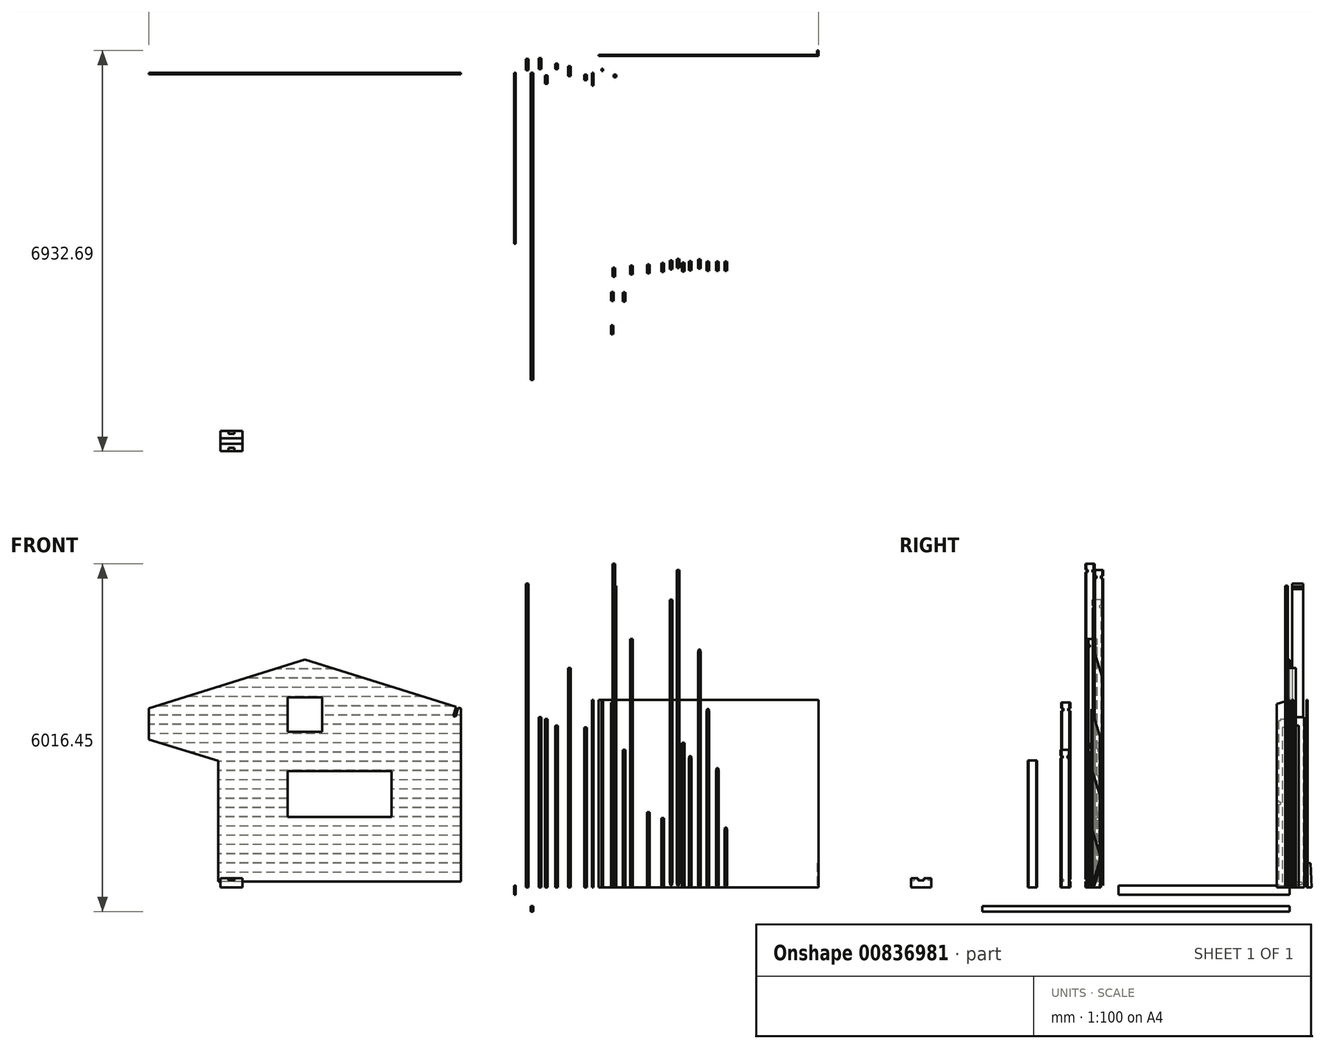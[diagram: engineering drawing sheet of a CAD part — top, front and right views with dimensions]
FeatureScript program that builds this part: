
annotation { "Feature Type Name" : "Feature", "Feature Type Description" : "" }
export const myFeature = defineFeature(function(context is Context, id is Id, definition is map)
    precondition{}
    {
        {
            var Q0;
            Q0=qCreatedBy(makeId("Top.planeOp"),FACE);
            var sketch = newSketch(context, id + "F0", { "sketchPlane" : qUnion([Q0])});
            skLineSegment(sketch, "E0.bottom", {"start": v(-174.56, 238.66) * mm, "end": v(-129.56, 238.66) * mm});
            skLineSegment(sketch, "E0.top", {"start": v(-174.56, 43.66) * mm, "end": v(-129.56, 43.66) * mm});
            skLineSegment(sketch, "E0.left", {"start": v(-174.56, 238.66) * mm, "end": v(-174.56, 43.66) * mm});
            skLineSegment(sketch, "E0.right", {"start": v(-129.56, 238.66) * mm, "end": v(-129.56, 43.66) * mm});
            skSolve(sketch);
        }
        {
            var Q0;
            Q0=makeQuery(id+"F0.imprint","IMPRINT",FACE,{"disambiguationData":[TD([[makeQuery(id+"F0.imprint","IMPRINT",EDGE,{"derivedFrom":sQuery(id+"F0.wireOp",EDGE,"E0.bottom")}),-1.0]])]});
            extrude(context, id + "F1", {"entities" : qUnion([Q0]), "depth" : 5255 * mm, "offsetDistance" : 25 * mm});
        }
        {
            var Q0;
            Q0=qCreatedBy(makeId("Top.planeOp"),FACE);
            var sketch = newSketch(context, id + "F2", { "sketchPlane" : qUnion([Q0])});
            skLineSegment(sketch, "E1.bottom", {"start": v(49.35, 255.3) * mm, "end": v(94.35, 255.3) * mm});
            skLineSegment(sketch, "E1.top", {"start": v(49.35, 60.3) * mm, "end": v(94.35, 60.3) * mm});
            skLineSegment(sketch, "E1.left", {"start": v(49.35, 255.3) * mm, "end": v(49.35, 60.3) * mm});
            skLineSegment(sketch, "E1.right", {"start": v(94.35, 255.3) * mm, "end": v(94.35, 60.3) * mm});
            skSolve(sketch);
        }
        {
            var Q0;
            Q0=makeQuery(id+"F2.imprint","IMPRINT",FACE,{"disambiguationData":[TD([[makeQuery(id+"F2.imprint","IMPRINT",EDGE,{"derivedFrom":sQuery(id+"F2.wireOp",EDGE,"E1.bottom")}),-1.0]])]});
            extrude(context, id + "F3", {"entities" : qUnion([Q0]), "depth" : 2945 * mm, "offsetDistance" : 25 * mm});
        }
        {
            var Q0;
            Q0=qCreatedBy(makeId("Top.planeOp"),FACE);
            var sketch = newSketch(context, id + "F4", { "sketchPlane" : qUnion([Q0])});
            skLineSegment(sketch, "E2.bottom", {"start": v(202.86, -191.83) * mm, "end": v(157.86, -191.83) * mm});
            skLineSegment(sketch, "E2.top", {"start": v(202.86, -46.83) * mm, "end": v(157.86, -46.83) * mm});
            skLineSegment(sketch, "E2.left", {"start": v(202.86, -191.83) * mm, "end": v(202.86, -46.83) * mm});
            skLineSegment(sketch, "E2.right", {"start": v(157.86, -191.83) * mm, "end": v(157.86, -46.83) * mm});
            skSolve(sketch);
        }
        {
            var Q0;
            Q0=makeQuery(id+"F4.imprint","IMPRINT",FACE,{"disambiguationData":[TD([[makeQuery(id+"F4.imprint","IMPRINT",EDGE,{"derivedFrom":sQuery(id+"F4.wireOp",EDGE,"E2.bottom")}),-1.0]])]});
            extrude(context, id + "F5", {"entities" : qUnion([Q0]), "depth" : 2914 * mm, "offsetDistance" : 25 * mm});
        }
        {
            var Q0;
            Q0=qCreatedBy(makeId("Front.planeOp"),FACE);
            var sketch = newSketch(context, id + "F6", { "sketchPlane" : qUnion([Q0])});
            skLineSegment(sketch, "E3", {"start": v(-1295, 99.93) * mm, "end": v(-6695, 99.93) * mm});
            skLineSegment(sketch, "E4", {"start": v(-6695, 99.93) * mm, "end": v(-6695, 3099.93) * mm});
            skLineSegment(sketch, "E5", {"start": v(-6695, 3099.93) * mm, "end": v(-3995, 3940.89) * mm});
            skLineSegment(sketch, "E6", {"start": v(-1295, 99.93) * mm, "end": v(-1295, 3099.93) * mm});
            skLineSegment(sketch, "E7", {"start": v(-1295, 3099.93) * mm, "end": v(-3995, 3940.89) * mm});
            skLineSegment(sketch, "E8.bottom", {"start": v(-1381.97, 3127.02) * mm, "end": v(-1339, 3113.63) * mm});
            skLineSegment(sketch, "E8.top", {"start": v(-1432.53, 2964.7) * mm, "end": v(-1389.56, 2951.33) * mm});
            skLineSegment(sketch, "E8.left", {"start": v(-1381.97, 3127.02) * mm, "end": v(-1432.53, 2964.7) * mm});
            skLineSegment(sketch, "E8.right", {"start": v(-1339, 3113.63) * mm, "end": v(-1389.56, 2951.33) * mm});
            skSolve(sketch);
        }
        {
            var Q0;
            Q0=makeQuery(id+"F6.imprint","IMPRINT",FACE,{"disambiguationData":[TD([[makeQuery(id+"F6.imprint","IMPRINT",EDGE,{"derivedFrom":sQuery(id+"F6.wireOp",EDGE,"E3")}),-1.0]])]});
            extrude(context, id + "F7", {"entities" : qUnion([Q0]), "depth" : 25 * mm, "offsetDistance" : 25 * mm});
        }
        {
            var Q0;
            Q0=makeQuery(id+"F7.opExtrude","SWEPT_FACE",FACE,{"disambiguationData":[OSD([sQuery(id+"F6.wireOp",EDGE,"E4")])]});
            var sketch = newSketch(context, id + "F8", { "sketchPlane" : qUnion([Q0])});
            skLineSegment(sketch, "E9.bottom", {"start": v(0, 262.93) * mm, "end": v(3, 262.93) * mm});
            skLineSegment(sketch, "E9.top", {"start": v(0, 259.93) * mm, "end": v(3, 259.93) * mm});
            skLineSegment(sketch, "E9.left", {"start": v(0, 262.93) * mm, "end": v(0, 259.93) * mm});
            skLineSegment(sketch, "E9.right", {"start": v(3, 262.93) * mm, "end": v(3, 259.93) * mm});
            skLineSegment(sketch, "E10.0.1.0", {"start": v(0, 419.93) * mm, "end": v(3, 419.93) * mm});
            skLineSegment(sketch, "E10.0.1.1", {"start": v(3, 422.93) * mm, "end": v(3, 419.93) * mm});
            skLineSegment(sketch, "E10.0.1.2", {"start": v(0, 422.93) * mm, "end": v(0, 419.93) * mm});
            skLineSegment(sketch, "E10.0.1.3", {"start": v(0, 422.93) * mm, "end": v(3, 422.93) * mm});
            skLineSegment(sketch, "E10.0.2.0", {"start": v(0, 579.93) * mm, "end": v(3, 579.93) * mm});
            skLineSegment(sketch, "E10.0.2.1", {"start": v(3, 582.93) * mm, "end": v(3, 579.93) * mm});
            skLineSegment(sketch, "E10.0.2.2", {"start": v(0, 582.93) * mm, "end": v(0, 579.93) * mm});
            skLineSegment(sketch, "E10.0.2.3", {"start": v(0, 582.93) * mm, "end": v(3, 582.93) * mm});
            skLineSegment(sketch, "E10.0.3.0", {"start": v(0, 739.93) * mm, "end": v(3, 739.93) * mm});
            skLineSegment(sketch, "E10.0.3.1", {"start": v(3, 742.93) * mm, "end": v(3, 739.93) * mm});
            skLineSegment(sketch, "E10.0.3.2", {"start": v(0, 742.93) * mm, "end": v(0, 739.93) * mm});
            skLineSegment(sketch, "E10.0.3.3", {"start": v(0, 742.93) * mm, "end": v(3, 742.93) * mm});
            skLineSegment(sketch, "E10.0.4.0", {"start": v(0, 899.93) * mm, "end": v(3, 899.93) * mm});
            skLineSegment(sketch, "E10.0.4.1", {"start": v(3, 902.93) * mm, "end": v(3, 899.93) * mm});
            skLineSegment(sketch, "E10.0.4.2", {"start": v(0, 902.93) * mm, "end": v(0, 899.93) * mm});
            skLineSegment(sketch, "E10.0.4.3", {"start": v(0, 902.93) * mm, "end": v(3, 902.93) * mm});
            skLineSegment(sketch, "E10.0.5.0", {"start": v(0, 1059.93) * mm, "end": v(3, 1059.93) * mm});
            skLineSegment(sketch, "E10.0.5.1", {"start": v(3, 1062.93) * mm, "end": v(3, 1059.93) * mm});
            skLineSegment(sketch, "E10.0.5.2", {"start": v(0, 1062.93) * mm, "end": v(0, 1059.93) * mm});
            skLineSegment(sketch, "E10.0.5.3", {"start": v(0, 1062.93) * mm, "end": v(3, 1062.93) * mm});
            skLineSegment(sketch, "E10.0.6.0", {"start": v(0, 1219.93) * mm, "end": v(3, 1219.93) * mm});
            skLineSegment(sketch, "E10.0.6.1", {"start": v(3, 1222.93) * mm, "end": v(3, 1219.93) * mm});
            skLineSegment(sketch, "E10.0.6.2", {"start": v(0, 1222.93) * mm, "end": v(0, 1219.93) * mm});
            skLineSegment(sketch, "E10.0.6.3", {"start": v(0, 1222.93) * mm, "end": v(3, 1222.93) * mm});
            skLineSegment(sketch, "E10.0.7.0", {"start": v(0, 1379.93) * mm, "end": v(3, 1379.93) * mm});
            skLineSegment(sketch, "E10.0.7.1", {"start": v(3, 1382.93) * mm, "end": v(3, 1379.93) * mm});
            skLineSegment(sketch, "E10.0.7.2", {"start": v(0, 1382.93) * mm, "end": v(0, 1379.93) * mm});
            skLineSegment(sketch, "E10.0.7.3", {"start": v(0, 1382.93) * mm, "end": v(3, 1382.93) * mm});
            skLineSegment(sketch, "E10.0.8.0", {"start": v(0, 1539.93) * mm, "end": v(3, 1539.93) * mm});
            skLineSegment(sketch, "E10.0.8.1", {"start": v(3, 1542.93) * mm, "end": v(3, 1539.93) * mm});
            skLineSegment(sketch, "E10.0.8.2", {"start": v(0, 1542.93) * mm, "end": v(0, 1539.93) * mm});
            skLineSegment(sketch, "E10.0.8.3", {"start": v(0, 1542.93) * mm, "end": v(3, 1542.93) * mm});
            skLineSegment(sketch, "E10.0.9.0", {"start": v(0, 1699.93) * mm, "end": v(3, 1699.93) * mm});
            skLineSegment(sketch, "E10.0.9.1", {"start": v(3, 1702.93) * mm, "end": v(3, 1699.93) * mm});
            skLineSegment(sketch, "E10.0.9.2", {"start": v(0, 1702.93) * mm, "end": v(0, 1699.93) * mm});
            skLineSegment(sketch, "E10.0.9.3", {"start": v(0, 1702.93) * mm, "end": v(3, 1702.93) * mm});
            skLineSegment(sketch, "E10.0.10.0", {"start": v(0, 1859.93) * mm, "end": v(3, 1859.93) * mm});
            skLineSegment(sketch, "E10.0.10.1", {"start": v(3, 1862.93) * mm, "end": v(3, 1859.93) * mm});
            skLineSegment(sketch, "E10.0.10.2", {"start": v(0, 1862.93) * mm, "end": v(0, 1859.93) * mm});
            skLineSegment(sketch, "E10.0.10.3", {"start": v(0, 1862.93) * mm, "end": v(3, 1862.93) * mm});
            skLineSegment(sketch, "E10.0.11.0", {"start": v(0, 2019.93) * mm, "end": v(3, 2019.93) * mm});
            skLineSegment(sketch, "E10.0.11.1", {"start": v(3, 2022.93) * mm, "end": v(3, 2019.93) * mm});
            skLineSegment(sketch, "E10.0.11.2", {"start": v(0, 2022.93) * mm, "end": v(0, 2019.93) * mm});
            skLineSegment(sketch, "E10.0.11.3", {"start": v(0, 2022.93) * mm, "end": v(3, 2022.93) * mm});
            skLineSegment(sketch, "E10.direction1", {"start": v(0, 259.93) * mm, "end": v(25, 259.93) * mm, "construction": true});
            skLineSegment(sketch, "E10.direction2", {"start": v(0, 259.93) * mm, "end": v(0, 419.93) * mm, "construction": true});
            skLineSegment(sketch, "E11.0.0.12", {"start": v(0, 2179.93) * mm, "end": v(3, 2179.93) * mm});
            skLineSegment(sketch, "E11.3.0.12", {"start": v(3, 2182.93) * mm, "end": v(3, 2179.93) * mm});
            skLineSegment(sketch, "E11.6.0.12", {"start": v(0, 2182.93) * mm, "end": v(0, 2179.93) * mm});
            skLineSegment(sketch, "E11.9.0.12", {"start": v(0, 2182.93) * mm, "end": v(3, 2182.93) * mm});
            skLineSegment(sketch, "E11.0.0.13", {"start": v(0, 2339.93) * mm, "end": v(3, 2339.93) * mm});
            skLineSegment(sketch, "E11.3.0.13", {"start": v(3, 2342.93) * mm, "end": v(3, 2339.93) * mm});
            skLineSegment(sketch, "E11.6.0.13", {"start": v(0, 2342.93) * mm, "end": v(0, 2339.93) * mm});
            skLineSegment(sketch, "E11.9.0.13", {"start": v(0, 2342.93) * mm, "end": v(3, 2342.93) * mm});
            skLineSegment(sketch, "E11.0.0.14", {"start": v(0, 2499.93) * mm, "end": v(3, 2499.93) * mm});
            skLineSegment(sketch, "E11.3.0.14", {"start": v(3, 2502.93) * mm, "end": v(3, 2499.93) * mm});
            skLineSegment(sketch, "E11.6.0.14", {"start": v(0, 2502.93) * mm, "end": v(0, 2499.93) * mm});
            skLineSegment(sketch, "E11.9.0.14", {"start": v(0, 2502.93) * mm, "end": v(3, 2502.93) * mm});
            skLineSegment(sketch, "E11.0.0.15", {"start": v(0, 2659.93) * mm, "end": v(3, 2659.93) * mm});
            skLineSegment(sketch, "E11.3.0.15", {"start": v(3, 2662.93) * mm, "end": v(3, 2659.93) * mm});
            skLineSegment(sketch, "E11.6.0.15", {"start": v(0, 2662.93) * mm, "end": v(0, 2659.93) * mm});
            skLineSegment(sketch, "E11.9.0.15", {"start": v(0, 2662.93) * mm, "end": v(3, 2662.93) * mm});
            skLineSegment(sketch, "E11.0.0.16", {"start": v(0, 2819.93) * mm, "end": v(3, 2819.93) * mm});
            skLineSegment(sketch, "E11.3.0.16", {"start": v(3, 2822.93) * mm, "end": v(3, 2819.93) * mm});
            skLineSegment(sketch, "E11.6.0.16", {"start": v(0, 2822.93) * mm, "end": v(0, 2819.93) * mm});
            skLineSegment(sketch, "E11.9.0.16", {"start": v(0, 2822.93) * mm, "end": v(3, 2822.93) * mm});
            skLineSegment(sketch, "E11.0.0.17", {"start": v(0, 2979.93) * mm, "end": v(3, 2979.93) * mm});
            skLineSegment(sketch, "E11.3.0.17", {"start": v(3, 2982.93) * mm, "end": v(3, 2979.93) * mm});
            skLineSegment(sketch, "E11.6.0.17", {"start": v(0, 2982.93) * mm, "end": v(0, 2979.93) * mm});
            skLineSegment(sketch, "E11.9.0.17", {"start": v(0, 2982.93) * mm, "end": v(3, 2982.93) * mm});
            skLineSegment(sketch, "E11.0.0.18", {"start": v(0, 3139.93) * mm, "end": v(3, 3139.93) * mm});
            skLineSegment(sketch, "E11.3.0.18", {"start": v(3, 3142.93) * mm, "end": v(3, 3139.93) * mm});
            skLineSegment(sketch, "E11.6.0.18", {"start": v(0, 3142.93) * mm, "end": v(0, 3139.93) * mm});
            skLineSegment(sketch, "E11.9.0.18", {"start": v(0, 3142.93) * mm, "end": v(3, 3142.93) * mm});
            skLineSegment(sketch, "E11.0.0.19", {"start": v(0, 3299.93) * mm, "end": v(3, 3299.93) * mm});
            skLineSegment(sketch, "E11.3.0.19", {"start": v(3, 3302.93) * mm, "end": v(3, 3299.93) * mm});
            skLineSegment(sketch, "E11.6.0.19", {"start": v(0, 3302.93) * mm, "end": v(0, 3299.93) * mm});
            skLineSegment(sketch, "E11.9.0.19", {"start": v(0, 3302.93) * mm, "end": v(3, 3302.93) * mm});
            skLineSegment(sketch, "E12.0.0.20", {"start": v(0, 3459.93) * mm, "end": v(3, 3459.93) * mm});
            skLineSegment(sketch, "E12.3.0.20", {"start": v(3, 3462.93) * mm, "end": v(3, 3459.93) * mm});
            skLineSegment(sketch, "E12.6.0.20", {"start": v(0, 3462.93) * mm, "end": v(0, 3459.93) * mm});
            skLineSegment(sketch, "E12.9.0.20", {"start": v(0, 3462.93) * mm, "end": v(3, 3462.93) * mm});
            skLineSegment(sketch, "E12.0.0.21", {"start": v(0, 3619.93) * mm, "end": v(3, 3619.93) * mm});
            skLineSegment(sketch, "E12.3.0.21", {"start": v(3, 3622.93) * mm, "end": v(3, 3619.93) * mm});
            skLineSegment(sketch, "E12.6.0.21", {"start": v(0, 3622.93) * mm, "end": v(0, 3619.93) * mm});
            skLineSegment(sketch, "E12.9.0.21", {"start": v(0, 3622.93) * mm, "end": v(3, 3622.93) * mm});
            skLineSegment(sketch, "E12.0.0.22", {"start": v(0, 3779.93) * mm, "end": v(3, 3779.93) * mm});
            skLineSegment(sketch, "E12.3.0.22", {"start": v(3, 3782.93) * mm, "end": v(3, 3779.93) * mm});
            skLineSegment(sketch, "E12.6.0.22", {"start": v(0, 3782.93) * mm, "end": v(0, 3779.93) * mm});
            skLineSegment(sketch, "E12.9.0.22", {"start": v(0, 3782.93) * mm, "end": v(3, 3782.93) * mm});
            skLineSegment(sketch, "E12.0.0.23", {"start": v(0, 3939.93) * mm, "end": v(3, 3939.93) * mm});
            skLineSegment(sketch, "E12.3.0.23", {"start": v(3, 3942.93) * mm, "end": v(3, 3939.93) * mm});
            skLineSegment(sketch, "E12.6.0.23", {"start": v(0, 3942.93) * mm, "end": v(0, 3939.93) * mm});
            skLineSegment(sketch, "E12.9.0.23", {"start": v(0, 3942.93) * mm, "end": v(3, 3942.93) * mm});
            skLineSegment(sketch, "E12.0.0.24", {"start": v(0, 4099.93) * mm, "end": v(3, 4099.93) * mm});
            skLineSegment(sketch, "E12.3.0.24", {"start": v(3, 4102.93) * mm, "end": v(3, 4099.93) * mm});
            skLineSegment(sketch, "E12.6.0.24", {"start": v(0, 4102.93) * mm, "end": v(0, 4099.93) * mm});
            skLineSegment(sketch, "E12.9.0.24", {"start": v(0, 4102.93) * mm, "end": v(3, 4102.93) * mm});
            skSolve(sketch);
        }
        {
            var Q0;
            Q0=makeQuery(id+"F8.imprint","IMPRINT",FACE,{"disambiguationData":[TD([[makeQuery(id+"F8.imprint","IMPRINT",EDGE,{"derivedFrom":sQuery(id+"F8.wireOp",EDGE,"E9.bottom")}),-1.0]])]});
            var Q1;
            Q1=makeQuery(id+"F8.imprint","IMPRINT",FACE,{"disambiguationData":[TD([[makeQuery(id+"F8.imprint","IMPRINT",EDGE,{"derivedFrom":sQuery(id+"F8.wireOp",EDGE,"E10.0.1.0")}),1.0]])]});
            var Q2;
            Q2=makeQuery(id+"F8.imprint","IMPRINT",FACE,{"disambiguationData":[TD([[makeQuery(id+"F8.imprint","IMPRINT",EDGE,{"derivedFrom":sQuery(id+"F8.wireOp",EDGE,"E10.0.3.0")}),1.0]])]});
            var Q3;
            Q3=makeQuery(id+"F8.imprint","IMPRINT",FACE,{"disambiguationData":[TD([[makeQuery(id+"F8.imprint","IMPRINT",EDGE,{"derivedFrom":sQuery(id+"F8.wireOp",EDGE,"E10.0.4.0")}),1.0]])]});
            var Q4;
            Q4=makeQuery(id+"F8.imprint","IMPRINT",FACE,{"disambiguationData":[TD([[makeQuery(id+"F8.imprint","IMPRINT",EDGE,{"derivedFrom":sQuery(id+"F8.wireOp",EDGE,"E10.0.5.0")}),1.0]])]});
            var Q5;
            Q5=makeQuery(id+"F8.imprint","IMPRINT",FACE,{"disambiguationData":[TD([[makeQuery(id+"F8.imprint","IMPRINT",EDGE,{"derivedFrom":sQuery(id+"F8.wireOp",EDGE,"E10.0.6.0")}),1.0]])]});
            var Q6;
            Q6=makeQuery(id+"F8.imprint","IMPRINT",FACE,{"disambiguationData":[TD([[makeQuery(id+"F8.imprint","IMPRINT",EDGE,{"derivedFrom":sQuery(id+"F8.wireOp",EDGE,"E10.0.7.0")}),1.0]])]});
            var Q7;
            Q7=makeQuery(id+"F8.imprint","IMPRINT",FACE,{"disambiguationData":[TD([[makeQuery(id+"F8.imprint","IMPRINT",EDGE,{"derivedFrom":sQuery(id+"F8.wireOp",EDGE,"E10.0.8.0")}),1.0]])]});
            var Q8;
            Q8=makeQuery(id+"F8.imprint","IMPRINT",FACE,{"disambiguationData":[TD([[makeQuery(id+"F8.imprint","IMPRINT",EDGE,{"derivedFrom":sQuery(id+"F8.wireOp",EDGE,"E10.0.9.0")}),1.0]])]});
            var Q9;
            Q9=makeQuery(id+"F8.imprint","IMPRINT",FACE,{"disambiguationData":[TD([[makeQuery(id+"F8.imprint","IMPRINT",EDGE,{"derivedFrom":sQuery(id+"F8.wireOp",EDGE,"E10.0.10.0")}),1.0]])]});
            var Q10;
            Q10=makeQuery(id+"F8.imprint","IMPRINT",FACE,{"disambiguationData":[TD([[makeQuery(id+"F8.imprint","IMPRINT",EDGE,{"derivedFrom":sQuery(id+"F8.wireOp",EDGE,"E10.0.11.0")}),1.0]])]});
            var Q11;
            Q11=makeQuery(id+"F8.imprint","IMPRINT",FACE,{"disambiguationData":[TD([[makeQuery(id+"F8.imprint","IMPRINT",EDGE,{"derivedFrom":sQuery(id+"F8.wireOp",EDGE,"E10.0.2.0")}),1.0]])]});
            var Q12;
            Q12=makeQuery(id+"F8.imprint","IMPRINT",FACE,{"disambiguationData":[TD([[makeQuery(id+"F8.imprint","IMPRINT",EDGE,{"derivedFrom":sQuery(id+"F8.wireOp",EDGE,"E11.0.0.12")}),1.0]])]});
            var Q13;
            Q13=makeQuery(id+"F8.imprint","IMPRINT",FACE,{"disambiguationData":[TD([[makeQuery(id+"F8.imprint","IMPRINT",EDGE,{"derivedFrom":sQuery(id+"F8.wireOp",EDGE,"E11.0.0.13")}),1.0]])]});
            var Q14;
            Q14=makeQuery(id+"F8.imprint","IMPRINT",FACE,{"disambiguationData":[TD([[makeQuery(id+"F8.imprint","IMPRINT",EDGE,{"derivedFrom":sQuery(id+"F8.wireOp",EDGE,"E11.0.0.14")}),1.0]])]});
            var Q15;
            Q15=makeQuery(id+"F8.imprint","IMPRINT",FACE,{"disambiguationData":[TD([[makeQuery(id+"F8.imprint","IMPRINT",EDGE,{"derivedFrom":sQuery(id+"F8.wireOp",EDGE,"E11.0.0.15")}),1.0]])]});
            var Q16;
            Q16=makeQuery(id+"F8.imprint","IMPRINT",FACE,{"disambiguationData":[TD([[makeQuery(id+"F8.imprint","IMPRINT",EDGE,{"derivedFrom":sQuery(id+"F8.wireOp",EDGE,"E11.0.0.16")}),1.0]])]});
            var Q17;
            Q17=makeQuery(id+"F8.imprint","IMPRINT",FACE,{"disambiguationData":[TD([[makeQuery(id+"F8.imprint","IMPRINT",EDGE,{"derivedFrom":sQuery(id+"F8.wireOp",EDGE,"E11.0.0.17")}),1.0]])]});
            var Q18;
            Q18=makeQuery(id+"F8.imprint","IMPRINT",FACE,{"disambiguationData":[TD([[makeQuery(id+"F8.imprint","IMPRINT",EDGE,{"derivedFrom":sQuery(id+"F8.wireOp",EDGE,"E11.0.0.18")}),1.0]])]});
            var Q19;
            Q19=makeQuery(id+"F8.imprint","IMPRINT",FACE,{"disambiguationData":[TD([[makeQuery(id+"F8.imprint","IMPRINT",EDGE,{"derivedFrom":sQuery(id+"F8.wireOp",EDGE,"E11.0.0.19")}),1.0]])]});
            var Q20;
            Q20=makeQuery(id+"F8.imprint","IMPRINT",FACE,{"disambiguationData":[TD([[makeQuery(id+"F8.imprint","IMPRINT",EDGE,{"derivedFrom":sQuery(id+"F8.wireOp",EDGE,"E12.0.0.20")}),1.0]])]});
            var Q21;
            Q21=makeQuery(id+"F8.imprint","IMPRINT",FACE,{"disambiguationData":[TD([[makeQuery(id+"F8.imprint","IMPRINT",EDGE,{"derivedFrom":sQuery(id+"F8.wireOp",EDGE,"E12.0.0.21")}),1.0]])]});
            var Q22;
            Q22=makeQuery(id+"F8.imprint","IMPRINT",FACE,{"disambiguationData":[TD([[makeQuery(id+"F8.imprint","IMPRINT",EDGE,{"derivedFrom":sQuery(id+"F8.wireOp",EDGE,"E12.0.0.22")}),1.0]])]});
            var Q23;
            Q23=makeQuery(id+"F8.imprint","IMPRINT",FACE,{"disambiguationData":[TD([[makeQuery(id+"F8.imprint","IMPRINT",EDGE,{"derivedFrom":sQuery(id+"F8.wireOp",EDGE,"E12.0.0.23")}),1.0]])]});
            var Q24;
            Q24=makeQuery(id+"F8.imprint","IMPRINT",FACE,{"disambiguationData":[TD([[makeQuery(id+"F8.imprint","IMPRINT",EDGE,{"derivedFrom":sQuery(id+"F8.wireOp",EDGE,"E12.0.0.24")}),1.0]])]});
            extrude(context, id + "F9", {"entities" : qUnion([Q0, Q1, Q2, Q3, Q4, Q5, Q6, Q7, Q8, Q9, Q10, Q11, Q12, Q13, Q14, Q15, Q16, Q17, Q18, Q19, Q20, Q21, Q22, Q23, Q24]), "operationType" : NewBodyOperationType.REMOVE, "oppositeDirection" : true, "depth" : 5555 * mm, "offsetDistance" : 25 * mm});
        }
        {
            var Q0;
            Q0=qCreatedBy(makeId("Top.planeOp"),FACE);
            var sketch = newSketch(context, id + "F10", { "sketchPlane" : qUnion([Q0])});
            skLineSegment(sketch, "E13.bottom", {"start": v(336.12, 157.04) * mm, "end": v(381.12, 157.04) * mm});
            skLineSegment(sketch, "E13.top", {"start": v(336.12, 62.04) * mm, "end": v(381.12, 62.04) * mm});
            skLineSegment(sketch, "E13.left", {"start": v(336.12, 157.04) * mm, "end": v(336.12, 62.04) * mm});
            skLineSegment(sketch, "E13.right", {"start": v(381.12, 157.04) * mm, "end": v(381.12, 62.04) * mm});
            skSolve(sketch);
        }
        {
            var Q0;
            Q0=makeQuery(id+"F10.imprint","IMPRINT",FACE,{"disambiguationData":[TD([[makeQuery(id+"F10.imprint","IMPRINT",EDGE,{"derivedFrom":sQuery(id+"F10.wireOp",EDGE,"E13.bottom")}),-1.0]])]});
            extrude(context, id + "F11", {"entities" : qUnion([Q0]), "depth" : 2800 * mm, "offsetDistance" : 25 * mm});
        }
        {
            var Q0;
            Q0=qCreatedBy(makeId("Top.planeOp"),FACE);
            var sketch = newSketch(context, id + "F12", { "sketchPlane" : qUnion([Q0])});
            skLineSegment(sketch, "E14.bottom", {"start": v(558.27, 111.52) * mm, "end": v(603.27, 111.52) * mm});
            skLineSegment(sketch, "E14.top", {"start": v(558.27, -58.48) * mm, "end": v(603.27, -58.48) * mm});
            skLineSegment(sketch, "E14.left", {"start": v(558.27, 111.52) * mm, "end": v(558.27, -58.48) * mm});
            skLineSegment(sketch, "E14.right", {"start": v(603.27, 111.52) * mm, "end": v(603.27, -58.48) * mm});
            skSolve(sketch);
        }
        {
            var Q0;
            Q0=makeQuery(id+"F12.imprint","IMPRINT",FACE,{"disambiguationData":[TD([[makeQuery(id+"F12.imprint","IMPRINT",EDGE,{"derivedFrom":sQuery(id+"F12.wireOp",EDGE,"E14.bottom")}),-1.0]])]});
            extrude(context, id + "F13", {"entities" : qUnion([Q0]), "depth" : 3800 * mm, "offsetDistance" : 25 * mm});
        }
        {
            var Q0;
            Q0=qCreatedBy(makeId("Top.planeOp"),FACE);
            var sketch = newSketch(context, id + "F14", { "sketchPlane" : qUnion([Q0])});
            skLineSegment(sketch, "E15.bottom", {"start": v(838.72, -32.1) * mm, "end": v(883.72, -32.1) * mm});
            skLineSegment(sketch, "E15.top", {"start": v(838.72, -127.1) * mm, "end": v(883.72, -127.1) * mm});
            skLineSegment(sketch, "E15.left", {"start": v(838.72, -32.1) * mm, "end": v(838.72, -127.1) * mm});
            skLineSegment(sketch, "E15.right", {"start": v(883.72, -32.1) * mm, "end": v(883.72, -127.1) * mm});
            skSolve(sketch);
        }
        {
            var Q0;
            Q0=makeQuery(id+"F14.imprint","IMPRINT",FACE,{"disambiguationData":[TD([[makeQuery(id+"F14.imprint","IMPRINT",EDGE,{"derivedFrom":sQuery(id+"F14.wireOp",EDGE,"E15.bottom")}),-1.0]])]});
            extrude(context, id + "F15", {"entities" : qUnion([Q0]), "depth" : 2768 * mm, "offsetDistance" : 25 * mm});
        }
        {
            var Q0;
            Q0=qCreatedBy(makeId("Top.planeOp"),FACE);
            var sketch = newSketch(context, id + "F16", { "sketchPlane" : qUnion([Q0])});
            skLineSegment(sketch, "E16.bottom", {"start": v(971.19, 0) * mm, "end": v(993.19, 0) * mm});
            skLineSegment(sketch, "E16.top", {"start": v(971.19, -220) * mm, "end": v(993.19, -220) * mm});
            skLineSegment(sketch, "E16.left", {"start": v(971.19, 0) * mm, "end": v(971.19, -220) * mm});
            skLineSegment(sketch, "E16.right", {"start": v(993.19, 0) * mm, "end": v(993.19, -220) * mm});
            skSolve(sketch);
        }
        {
            var Q0;
            Q0=makeQuery(id+"F16.imprint","IMPRINT",FACE,{"disambiguationData":[TD([[makeQuery(id+"F16.imprint","IMPRINT",EDGE,{"derivedFrom":sQuery(id+"F16.wireOp",EDGE,"E16.bottom")}),-1.0]])]});
            extrude(context, id + "F17", {"entities" : qUnion([Q0]), "depth" : 3333 * mm, "offsetDistance" : 25 * mm});
        }
        {
            var Q0;
            Q0=makeQuery(id+"F17.opExtrude","SWEPT_FACE",FACE,{"disambiguationData":[OSD([sQuery(id+"F16.wireOp",EDGE,"E16.right")])]});
            var sketch = newSketch(context, id + "F18", { "sketchPlane" : qUnion([Q0])});
            skLineSegment(sketch, "E17", {"start": v(0, 3333) * mm, "end": v(-220, 3333) * mm});
            skLineSegment(sketch, "E18", {"start": v(-220, 3333) * mm, "end": v(-220, 3264.48) * mm});
            skLineSegment(sketch, "E19", {"start": v(-220, 3264.48) * mm, "end": v(0, 3333) * mm});
            skLineSegment(sketch, "E20", {"start": v(0, 3333) * mm, "end": v(0, 3245.66) * mm});
            skLineSegment(sketch, "E21", {"start": v(0, 3245.66) * mm, "end": v(-220, 3177.14) * mm});
            skLineSegment(sketch, "E22", {"start": v(-220, 3177.14) * mm, "end": v(-220, 3264.48) * mm});
            skSolve(sketch);
        }
        {
            var Q0;
            Q0=makeQuery(id+"F18.imprint","IMPRINT",FACE,{"disambiguationData":[TD([[makeQuery(id+"F18.imprint","IMPRINT",EDGE,{"derivedFrom":sQuery(id+"F18.wireOp",EDGE,"E17")}),1.0]])]});
            var Q1;
            Q1=makeQuery(id+"F18.imprint","IMPRINT",FACE,{"disambiguationData":[TD([[makeQuery(id+"F18.imprint","IMPRINT",EDGE,{"derivedFrom":sQuery(id+"F18.wireOp",EDGE,"E19")}),-1.0]])]});
            extrude(context, id + "F19", {"entities" : qUnion([Q0, Q1]), "operationType" : NewBodyOperationType.REMOVE, "oppositeDirection" : true, "depth" : 25 * mm, "offsetDistance" : 25 * mm});
        }
        {
            var Q0;
            Q0=qCreatedBy(makeId("Top.planeOp"),FACE);
            var sketch = newSketch(context, id + "F20", { "sketchPlane" : qUnion([Q0])});
            skLineSegment(sketch, "E23.bottom", {"start": v(1086.41, 291.46) * mm, "end": v(4886.41, 291.46) * mm});
            skLineSegment(sketch, "E23.top", {"start": v(1086.41, 310.46) * mm, "end": v(4886.41, 310.46) * mm});
            skLineSegment(sketch, "E23.left", {"start": v(1086.41, 291.46) * mm, "end": v(1086.41, 310.46) * mm});
            skLineSegment(sketch, "E23.right", {"start": v(4886.41, 291.46) * mm, "end": v(4886.41, 310.46) * mm});
            skSolve(sketch);
        }
        {
            var Q0;
            Q0=makeQuery(id+"F20.imprint","IMPRINT",FACE,{"disambiguationData":[TD([[makeQuery(id+"F20.imprint","IMPRINT",EDGE,{"derivedFrom":sQuery(id+"F20.wireOp",EDGE,"E23.bottom")}),1.0]])]});
            extrude(context, id + "F21", {"entities" : qUnion([Q0]), "depth" : 3245 * mm, "offsetDistance" : 25 * mm});
        }
        {
            var Q0;
            Q0=qCreatedBy(makeId("Top.planeOp"),FACE);
            var sketch = newSketch(context, id + "F22", { "sketchPlane" : qUnion([Q0])});
            skLineSegment(sketch, "E24.bottom", {"start": v(1133.72, 68.45) * mm, "end": v(1158.72, 68.45) * mm});
            skLineSegment(sketch, "E24.top", {"start": v(1133.72, 32.45) * mm, "end": v(1158.72, 32.45) * mm});
            skLineSegment(sketch, "E24.left", {"start": v(1133.72, 68.45) * mm, "end": v(1133.72, 32.45) * mm});
            skLineSegment(sketch, "E24.right", {"start": v(1158.72, 68.45) * mm, "end": v(1158.72, 32.45) * mm});
            skSolve(sketch);
        }
        {
            var Q0;
            Q0=makeQuery(id+"F22.imprint","IMPRINT",FACE,{"disambiguationData":[TD([[makeQuery(id+"F22.imprint","IMPRINT",EDGE,{"derivedFrom":sQuery(id+"F22.wireOp",EDGE,"E24.bottom")}),-1.0]])]});
            extrude(context, id + "F23", {"entities" : qUnion([Q0]), "depth" : 3245 * mm, "offsetDistance" : 25 * mm});
        }
        {
            var Q0;
            Q0=makeQuery(id+"F21.opExtrude","SWEPT_FACE",FACE,{"disambiguationData":[OSD([sQuery(id+"F20.wireOp",EDGE,"E23.right")])]});
            var sketch = newSketch(context, id + "F24", { "sketchPlane" : qUnion([Q0])});
            skLineSegment(sketch, "E25", {"start": v(360.46, 419.26) * mm, "end": v(385.46, 0) * mm});
            skLineSegment(sketch, "E26", {"start": v(385.46, 0) * mm, "end": v(310.46, 0) * mm});
            skLineSegment(sketch, "E27", {"start": v(310.46, 0) * mm, "end": v(310.46, 419.26) * mm});
            skLineSegment(sketch, "E28", {"start": v(310.46, 419.26) * mm, "end": v(360.46, 419.26) * mm});
            skSolve(sketch);
        }
        {
            var Q0;
            Q0=makeQuery(id+"F24.imprint","IMPRINT",FACE,{"disambiguationData":[TD([[makeQuery(id+"F24.imprint","IMPRINT",EDGE,{"derivedFrom":sQuery(id+"F24.wireOp",EDGE,"E25")}),-1.0]])]});
            extrude(context, id + "F25", {"entities" : qUnion([Q0]), "oppositeDirection" : true, "depth" : 25 * mm, "offsetDistance" : 25 * mm});
        }
        {
            var Q0;
            Q0=qCreatedBy(makeId("Top.planeOp"),FACE);
            var sketch = newSketch(context, id + "F26", { "sketchPlane" : qUnion([Q0])});
            skLineSegment(sketch, "E29.bottom", {"start": v(1343.97, -31.78) * mm, "end": v(1388.97, -31.78) * mm});
            skLineSegment(sketch, "E29.top", {"start": v(1343.97, -76.78) * mm, "end": v(1388.97, -76.78) * mm});
            skLineSegment(sketch, "E29.left", {"start": v(1343.97, -31.78) * mm, "end": v(1343.97, -76.78) * mm});
            skLineSegment(sketch, "E29.right", {"start": v(1388.97, -31.78) * mm, "end": v(1388.97, -76.78) * mm});
            skSolve(sketch);
        }
        {
            var Q0;
            Q0=makeQuery(id+"F26.imprint","IMPRINT",FACE,{"disambiguationData":[TD([[makeQuery(id+"F26.imprint","IMPRINT",EDGE,{"derivedFrom":sQuery(id+"F26.wireOp",EDGE,"E29.bottom")}),-1.0]])]});
            extrude(context, id + "F27", {"entities" : qUnion([Q0]), "depth" : 5222 * mm, "offsetDistance" : 25 * mm});
        }
        {
            var Q0;
            Q0=qCreatedBy(makeId("Front.planeOp"),FACE);
            var sketch = newSketch(context, id + "F28", { "sketchPlane" : qUnion([Q0])});
            skLineSegment(sketch, "E30.bottom", {"start": v(-375.27, 33.01) * mm, "end": v(-358.27, 33.01) * mm});
            skLineSegment(sketch, "E30.top", {"start": v(-375.27, -126.99) * mm, "end": v(-358.27, -126.99) * mm});
            skLineSegment(sketch, "E30.left", {"start": v(-375.27, 33.01) * mm, "end": v(-375.27, -126.99) * mm});
            skLineSegment(sketch, "E30.right", {"start": v(-353.27, 28.01) * mm, "end": v(-353.27, -121.99) * mm});
            skPoint(sketch, "E31.visualSharp", {"position": v(-353.27, 33.01) * mm});
            skArc(sketch, "E31.filletArc", {"start": v(-353.27, 28.01) * mm, "mid": v(-354.73, 31.55) * mm, "end": v(-358.27, 33.01) * mm});
            skPoint(sketch, "E32.visualSharp", {"position": v(-353.27, -126.99) * mm});
            skArc(sketch, "E32.filletArc", {"start": v(-358.27, -126.99) * mm, "mid": v(-354.73, -125.52) * mm, "end": v(-353.27, -121.99) * mm});
            skSolve(sketch);
        }
        {
            var Q0;
            Q0=makeQuery(id+"F28.imprint","IMPRINT",FACE,{"disambiguationData":[TD([[makeQuery(id+"F28.imprint","IMPRINT",EDGE,{"derivedFrom":sQuery(id+"F28.wireOp",EDGE,"E30.bottom")}),-1.0]])]});
            extrude(context, id + "F29", {"entities" : qUnion([Q0]), "depth" : 2956 * mm, "offsetDistance" : 25 * mm});
        }
        {
            var Q0;
            {var subQ0=sQuery(id+"F6.wireOp",EDGE,"E7");var subQ1=sQuery(id+"F6.wireOp",EDGE,"E6");var subQ2=sQuery(id+"F6.wireOp",EDGE,"E8.right");var subQ4=sQuery(id+"F6.wireOp",EDGE,"E5");var subQ5=sQuery(id+"F6.wireOp",EDGE,"E4");var subQ6=sQuery(id+"F6.wireOp",EDGE,"E8.left");var subQ7=sQuery(id+"F6.wireOp",EDGE,"E8.top");Q0=makeQuery(id+"F9.boolean.opBoolean","SPLIT",FACE,{"disambiguationData":[TD([makeQuery(id+"F7.opExtrude","SWEPT_FACE",FACE,{"disambiguationData":[OSD([subQ4])]})])],"derivedFrom":makeQuery(id+"F7.opExtrude","CAP_FACE",FACE,{"disambiguationData":[OSD([sQuery(id+"F6.wireOp",EDGE,"E3"),subQ5,subQ4,subQ1,subQ0,subQ7,subQ6,subQ2])],"isStart":true})});}
            var sketch = newSketch(context, id + "F30", { "sketchPlane" : qUnion([Q0])});
            skLineSegment(sketch, "E33.bottom", {"start": v(4295, 2009.93) * mm, "end": v(2495, 2009.93) * mm});
            skLineSegment(sketch, "E33.top", {"start": v(4295, 1219.93) * mm, "end": v(2495, 1219.93) * mm});
            skLineSegment(sketch, "E33.left", {"start": v(4295, 2009.93) * mm, "end": v(4295, 1219.93) * mm});
            skLineSegment(sketch, "E33.right", {"start": v(2495, 2009.93) * mm, "end": v(2495, 1219.93) * mm});
            skLineSegment(sketch, "E34.bottom", {"start": v(3695, 3289.93) * mm, "end": v(4295, 3289.93) * mm});
            skLineSegment(sketch, "E34.top", {"start": v(3695, 2689.93) * mm, "end": v(4295, 2689.93) * mm});
            skLineSegment(sketch, "E34.left", {"start": v(3695, 3289.93) * mm, "end": v(3695, 2689.93) * mm});
            skLineSegment(sketch, "E34.right", {"start": v(4295, 3289.93) * mm, "end": v(4295, 2689.93) * mm});
            skLineSegment(sketch, "E35.bottom", {"start": v(3065, 2009.93) * mm, "end": v(3110, 2009.93) * mm});
            skLineSegment(sketch, "E35.top", {"start": v(3065, 1219.93) * mm, "end": v(3110, 1219.93) * mm});
            skLineSegment(sketch, "E35.left", {"start": v(3065, 2009.93) * mm, "end": v(3065, 1219.93) * mm});
            skLineSegment(sketch, "E35.right", {"start": v(3110, 2009.93) * mm, "end": v(3110, 1219.93) * mm});
            skLineSegment(sketch, "E36.bottom", {"start": v(3680, 2009.93) * mm, "end": v(3725, 2009.93) * mm});
            skLineSegment(sketch, "E36.top", {"start": v(3680, 1219.93) * mm, "end": v(3725, 1219.93) * mm});
            skLineSegment(sketch, "E36.left", {"start": v(3680, 2009.93) * mm, "end": v(3680, 1219.93) * mm});
            skLineSegment(sketch, "E36.right", {"start": v(3725, 2009.93) * mm, "end": v(3725, 1219.93) * mm});
            skLineSegment(sketch, "E37", {"start": v(5495, 99.93) * mm, "end": v(5495, 2187.93) * mm});
            skLineSegment(sketch, "E38", {"start": v(5495, 2187.93) * mm, "end": v(6695, 2561.69) * mm});
            skLineSegment(sketch, "E39", {"start": v(6695, 2561.69) * mm, "end": v(6695, 99.93) * mm});
            skLineSegment(sketch, "E40", {"start": v(6695, 99.93) * mm, "end": v(5495, 99.93) * mm});
            skSolve(sketch);
        }
        {
            var Q0;
            Q0=makeQuery(id+"F30.imprint","IMPRINT",FACE,{"disambiguationData":[TD([[makeQuery(id+"F30.imprint","IMPRINT",EDGE,{"derivedFrom":sQuery(id+"F30.wireOp",EDGE,"E33.bottom")}),1.0]])]});
            var Q1;
            Q1=makeQuery(id+"F30.imprint","IMPRINT",FACE,{"disambiguationData":[TD([[makeQuery(id+"F30.imprint","IMPRINT",EDGE,{"derivedFrom":sQuery(id+"F30.wireOp",EDGE,"E34.bottom")}),-1.0]])]});
            var Q2;
            {var subQ0=sQuery(id+"F30.wireOp",EDGE,"E38");Q2=makeQuery(id+"F30.imprint","IMPRINT",FACE,{"disambiguationData":[TD([[makeQuery(id+"F30.imprint","IMPRINT",EDGE,{"derivedFrom":subQ0}),-1.0]])]});}
            var Q3;
            {var subQ0=sQuery(id+"F30.wireOp",EDGE,"E40");Q3=makeQuery(id+"F30.imprint","IMPRINT",FACE,{"disambiguationData":[TD([[makeQuery(id+"F30.imprint","IMPRINT",EDGE,{"derivedFrom":subQ0}),-1.0]])]});}
            var Q4;
            {var subQ0=sQuery(id+"F30.wireOp",EDGE,"E34.top");Q4=makeQuery(id+"F30.imprint","IMPRINT",FACE,{"disambiguationData":[TD([[makeQuery(id+"F30.imprint","IMPRINT",EDGE,{"derivedFrom":subQ0}),1.0]])]});}
            extrude(context, id + "F31", {"entities" : qUnion([Q0, Q1, Q2, Q3, Q4]), "operationType" : NewBodyOperationType.REMOVE, "oppositeDirection" : true, "depth" : 25 * mm, "offsetDistance" : 25 * mm});
        }
        {
            var Q0;
            Q0=qCreatedBy(makeId("Front.planeOp"),FACE);
            var sketch = newSketch(context, id + "F32", { "sketchPlane" : qUnion([Q0])});
            skLineSegment(sketch, "E41.bottom", {"start": v(-92.86, -321.45) * mm, "end": v(-47.86, -321.45) * mm});
            skLineSegment(sketch, "E41.top", {"start": v(-92.86, -416.45) * mm, "end": v(-47.86, -416.45) * mm});
            skLineSegment(sketch, "E41.left", {"start": v(-92.86, -321.45) * mm, "end": v(-92.86, -416.45) * mm});
            skLineSegment(sketch, "E41.right", {"start": v(-47.86, -321.45) * mm, "end": v(-47.86, -416.45) * mm});
            skSolve(sketch);
        }
        {
            var Q0;
            Q0=makeQuery(id+"F32.imprint","IMPRINT",FACE,{"disambiguationData":[TD([[makeQuery(id+"F32.imprint","IMPRINT",EDGE,{"derivedFrom":sQuery(id+"F32.wireOp",EDGE,"E41.bottom")}),-1.0]])]});
            extrude(context, id + "F33", {"entities" : qUnion([Q0]), "depth" : 5312 * mm, "offsetDistance" : 25 * mm});
        }
        {
            var Q0;
            Q0=qCreatedBy(makeId("Top.planeOp"),FACE);
            var sketch = newSketch(context, id + "F34", { "sketchPlane" : qUnion([Q0])});
            skLineSegment(sketch, "E42.bottom", {"start": v(-8675.04, -814.37) * mm, "end": v(-3275.04, -814.37) * mm});
            skLineSegment(sketch, "E42.top", {"start": v(-8675.04, -3814.37) * mm, "end": v(-4475.04, -3814.37) * mm});
            skLineSegment(sketch, "E42.left", {"start": v(-8675.04, -814.37) * mm, "end": v(-8675.04, -3814.37) * mm});
            skLineSegment(sketch, "E42.right", {"start": v(-3275.04, -814.37) * mm, "end": v(-3275.04, -2961.37) * mm});
            skLineSegment(sketch, "E43.0", {"start": v(-8528.04, -961.37) * mm, "end": v(-8528.04, -3667.37) * mm});
            skLineSegment(sketch, "E43.1", {"start": v(-8528.04, -961.37) * mm, "end": v(-3422.04, -961.37) * mm});
            skLineSegment(sketch, "E43.2", {"start": v(-3422.04, -961.37) * mm, "end": v(-3422.04, -2961.37) * mm});
            skLineSegment(sketch, "E43.3", {"start": v(-8528.04, -3667.37) * mm, "end": v(-4475.04, -3667.37) * mm});
            skLineSegment(sketch, "E44.bottom", {"start": v(-4475.04, -961.37) * mm, "end": v(-4410.04, -961.37) * mm});
            skLineSegment(sketch, "E44.top", {"start": v(-4475.04, -2961.37) * mm, "end": v(-4410.04, -2961.37) * mm});
            skLineSegment(sketch, "E44.left", {"start": v(-4475.04, -961.37) * mm, "end": v(-4475.04, -2961.37) * mm});
            skLineSegment(sketch, "E44.right", {"start": v(-4410.04, -961.37) * mm, "end": v(-4410.04, -2961.37) * mm});
            skLineSegment(sketch, "E45.bottom", {"start": v(-7310.52, -961.37) * mm, "end": v(-6510.52, -961.37) * mm});
            skLineSegment(sketch, "E45.top", {"start": v(-7310.52, -2961.37) * mm, "end": v(-6510.52, -2961.37) * mm});
            skLineSegment(sketch, "E45.left", {"start": v(-7310.52, -961.37) * mm, "end": v(-7310.52, -2961.37) * mm});
            skLineSegment(sketch, "E45.right", {"start": v(-6510.52, -961.37) * mm, "end": v(-6510.52, -2961.37) * mm});
            skLineSegment(sketch, "E46.bottom", {"start": v(-6510.52, -961.37) * mm, "end": v(-5710.52, -961.37) * mm});
            skLineSegment(sketch, "E46.top", {"start": v(-6510.52, -2961.37) * mm, "end": v(-5710.52, -2961.37) * mm});
            skLineSegment(sketch, "E46.right", {"start": v(-5710.52, -961.37) * mm, "end": v(-5710.52, -2961.37) * mm});
            skLineSegment(sketch, "E47.bottom", {"start": v(-4475.04, -961.37) * mm, "end": v(-5075.04, -961.37) * mm});
            skLineSegment(sketch, "E47.top", {"start": v(-4475.04, -2161.37) * mm, "end": v(-5075.04, -2161.37) * mm});
            skLineSegment(sketch, "E47.left", {"start": v(-4475.04, -961.37) * mm, "end": v(-4475.04, -2161.37) * mm});
            skLineSegment(sketch, "E47.right", {"start": v(-5075.04, -961.37) * mm, "end": v(-5075.04, -2161.37) * mm});
            skLineSegment(sketch, "E48.bottom", {"start": v(-4850.11, -3016.34) * mm, "end": v(-4437.46, -3642.61) * mm});
            skLineSegment(sketch, "E48.top", {"start": v(-4887.7, -3041.1) * mm, "end": v(-4475.04, -3667.37) * mm});
            skLineSegment(sketch, "E48.left", {"start": v(-4850.11, -3016.34) * mm, "end": v(-4887.7, -3041.1) * mm});
            skLineSegment(sketch, "E48.right", {"start": v(-4437.46, -3642.61) * mm, "end": v(-4475.04, -3667.37) * mm});
            skLineSegment(sketch, "E49.bottom", {"start": v(-4208.6, -3107.36) * mm, "end": v(-4216.82, -3063.11) * mm});
            skLineSegment(sketch, "E49.top", {"start": v(-3422.04, -2961.37) * mm, "end": v(-3430.25, -2917.13) * mm});
            skLineSegment(sketch, "E49.left", {"start": v(-4208.6, -3107.36) * mm, "end": v(-3422.04, -2961.37) * mm});
            skLineSegment(sketch, "E49.right", {"start": v(-4216.82, -3063.11) * mm, "end": v(-3430.25, -2917.13) * mm});
            skLineSegment(sketch, "E50", {"start": v(-3422.04, -2961.37) * mm, "end": v(-3275.04, -2961.37) * mm});
            skLineSegment(sketch, "E51", {"start": v(-4475.04, -3667.37) * mm, "end": v(-4475.04, -3814.37) * mm});
            skLineSegment(sketch, "E52", {"start": v(-3275.04, -2961.37) * mm, "end": v(-575.04, -2961.37) * mm});
            skLineSegment(sketch, "E53", {"start": v(-4475.04, -3814.37) * mm, "end": v(-4475.04, -5414.37) * mm});
            skLineSegment(sketch, "E54", {"start": v(-575.04, -2961.37) * mm, "end": v(-575.04, -5414.37) * mm});
            skLineSegment(sketch, "E55", {"start": v(-4475.04, -5414.37) * mm, "end": v(-575.04, -5414.37) * mm});
            skLineSegment(sketch, "E56.bottom", {"start": v(-4127.44, -5414.37) * mm, "end": v(-3395.08, -5576.08) * mm});
            skLineSegment(sketch, "E56.top", {"start": v(-4137.14, -5458.31) * mm, "end": v(-3404.78, -5620.02) * mm});
            skLineSegment(sketch, "E56.left", {"start": v(-4127.44, -5414.37) * mm, "end": v(-4137.14, -5458.31) * mm});
            skLineSegment(sketch, "E56.right", {"start": v(-3395.08, -5576.08) * mm, "end": v(-3404.78, -5620.02) * mm});
            skLineSegment(sketch, "E57.bottom", {"start": v(-1521.76, -5414.37) * mm, "end": v(-971.76, -5414.37) * mm});
            skLineSegment(sketch, "E57.top", {"start": v(-1521.76, -5458.37) * mm, "end": v(-971.76, -5458.37) * mm});
            skLineSegment(sketch, "E57.left", {"start": v(-1521.76, -5414.37) * mm, "end": v(-1521.76, -5458.37) * mm});
            skLineSegment(sketch, "E57.right", {"start": v(-971.76, -5414.37) * mm, "end": v(-971.76, -5458.37) * mm});
            skLineSegment(sketch, "E58.bottom", {"start": v(-1686.57, -5414.37) * mm, "end": v(-2236.57, -5414.37) * mm});
            skLineSegment(sketch, "E58.top", {"start": v(-1686.57, -5458.37) * mm, "end": v(-2236.57, -5458.37) * mm});
            skLineSegment(sketch, "E58.left", {"start": v(-1686.57, -5414.37) * mm, "end": v(-1686.57, -5458.37) * mm});
            skLineSegment(sketch, "E58.right", {"start": v(-2236.57, -5414.37) * mm, "end": v(-2236.57, -5458.37) * mm});
            skLineSegment(sketch, "E59.bottom", {"start": v(-637.78, -3041.1) * mm, "end": v(-2637.78, -3041.1) * mm});
            skLineSegment(sketch, "E59.top", {"start": v(-637.78, -3841.1) * mm, "end": v(-2637.78, -3841.1) * mm});
            skLineSegment(sketch, "E59.left", {"start": v(-637.78, -3041.1) * mm, "end": v(-637.78, -3841.1) * mm});
            skLineSegment(sketch, "E59.right", {"start": v(-2637.78, -3041.1) * mm, "end": v(-2637.78, -3841.1) * mm});
            skLineSegment(sketch, "E60.bottom", {"start": v(-4064.91, -1092.75) * mm, "end": v(-3723.93, -1092.75) * mm});
            skLineSegment(sketch, "E60.top", {"start": v(-4064.91, -1580.48) * mm, "end": v(-3723.93, -1580.48) * mm});
            skLineSegment(sketch, "E60.left", {"start": v(-4119.91, -1147.75) * mm, "end": v(-4119.91, -1525.48) * mm});
            skLineSegment(sketch, "E60.right", {"start": v(-3668.93, -1147.75) * mm, "end": v(-3668.93, -1525.48) * mm});
            skLineSegment(sketch, "E61.bottom", {"start": v(-4334.92, -1969.22) * mm, "end": v(-4088.16, -1969.22) * mm});
            skLineSegment(sketch, "E61.top", {"start": v(-4334.92, -2436.43) * mm, "end": v(-4088.16, -2436.43) * mm});
            skLineSegment(sketch, "E61.left", {"start": v(-4334.92, -1969.22) * mm, "end": v(-4334.92, -2436.43) * mm});
            skLineSegment(sketch, "E61.right", {"start": v(-4000.16, -2057.22) * mm, "end": v(-4000.16, -2348.43) * mm});
            skPoint(sketch, "E62.visualSharp", {"position": v(-3668.93, -1092.75) * mm});
            skArc(sketch, "E62.filletArc", {"start": v(-3668.93, -1147.75) * mm, "mid": v(-3685.04, -1108.86) * mm, "end": v(-3723.93, -1092.75) * mm});
            skPoint(sketch, "E63.visualSharp", {"position": v(-3668.93, -1580.48) * mm});
            skArc(sketch, "E63.filletArc", {"start": v(-3723.93, -1580.48) * mm, "mid": v(-3685.04, -1564.37) * mm, "end": v(-3668.93, -1525.48) * mm});
            skPoint(sketch, "E64.visualSharp", {"position": v(-4119.91, -1580.48) * mm});
            skArc(sketch, "E64.filletArc", {"start": v(-4119.91, -1525.48) * mm, "mid": v(-4103.8, -1564.37) * mm, "end": v(-4064.91, -1580.48) * mm});
            skPoint(sketch, "E65.visualSharp", {"position": v(-4119.91, -1092.75) * mm});
            skArc(sketch, "E65.filletArc", {"start": v(-4064.91, -1092.75) * mm, "mid": v(-4103.8, -1108.86) * mm, "end": v(-4119.91, -1147.75) * mm});
            skPoint(sketch, "E66.visualSharp", {"position": v(-4000.16, -1969.22) * mm});
            skArc(sketch, "E66.filletArc", {"start": v(-4000.16, -2057.22) * mm, "mid": v(-4025.94, -1995) * mm, "end": v(-4088.16, -1969.22) * mm});
            skPoint(sketch, "E67.visualSharp", {"position": v(-4000.16, -2436.43) * mm});
            skArc(sketch, "E67.filletArc", {"start": v(-4088.16, -2436.43) * mm, "mid": v(-4025.94, -2410.66) * mm, "end": v(-4000.16, -2348.43) * mm});
            skCircle(sketch, "E68", {"center": v(-3889.65, -1382.96) * mm, "radius": 128.9 * mm});
            skLineSegment(sketch, "E69.bottom", {"start": v(-7366.12, -4505.07) * mm, "end": v(-6255.12, -4505.07) * mm});
            skLineSegment(sketch, "E69.top", {"start": v(-7366.12, -4548.07) * mm, "end": v(-6255.12, -4548.07) * mm});
            skLineSegment(sketch, "E69.left", {"start": v(-7366.12, -4505.07) * mm, "end": v(-7366.12, -4548.07) * mm});
            skLineSegment(sketch, "E69.right", {"start": v(-6255.12, -4505.07) * mm, "end": v(-6255.12, -4548.07) * mm});
            skLineSegment(sketch, "E70.bottom", {"start": v(-7266.12, -4405.07) * mm, "end": v(-7223.12, -4405.07) * mm});
            skLineSegment(sketch, "E70.top", {"start": v(-7266.12, -5516.07) * mm, "end": v(-7223.12, -5516.07) * mm});
            skLineSegment(sketch, "E70.left", {"start": v(-7266.12, -4405.07) * mm, "end": v(-7266.12, -5516.07) * mm});
            skLineSegment(sketch, "E70.right", {"start": v(-7223.12, -4405.07) * mm, "end": v(-7223.12, -5516.07) * mm});
            skLineSegment(sketch, "E71", {"start": v(-7223.12, -4505.07) * mm, "end": v(-7230.12, -4512.07) * mm});
            skLineSegment(sketch, "E72", {"start": v(-7266.12, -4505.07) * mm, "end": v(-7259.12, -4512.07) * mm});
            skLineSegment(sketch, "E73.bottom", {"start": v(-7259.12, -4512.07) * mm, "end": v(-7230.12, -4512.07) * mm, "construction": true});
            skLineSegment(sketch, "E73.top", {"start": v(-7259.12, -4541.07) * mm, "end": v(-7230.12, -4541.07) * mm, "construction": true});
            skLineSegment(sketch, "E73.left", {"start": v(-7259.12, -4512.07) * mm, "end": v(-7259.12, -4541.07) * mm});
            skLineSegment(sketch, "E73.right", {"start": v(-7230.12, -4512.07) * mm, "end": v(-7230.12, -4541.07) * mm});
            skLineSegment(sketch, "E74.trimOffspring", {"start": v(-7230.12, -4541.07) * mm, "end": v(-7223.12, -4548.07) * mm});
            skLineSegment(sketch, "E75.trimOffspring", {"start": v(-7259.12, -4541.07) * mm, "end": v(-7266.12, -4548.07) * mm});
            skSolve(sketch);
        }
        {
            var Q0;
            {var subQ8=sQuery(id+"F34.wireOp",EDGE,"E43.0");Q0=makeQuery(id+"F34.imprint","IMPRINT",FACE,{"disambiguationData":[TD([[makeQuery(id+"F34.imprint","IMPRINT",EDGE,{"derivedFrom":subQ8}),1.0]])]});}
            var sketch = newSketch(context, id + "F35", { "sketchPlane" : qUnion([Q0])});
            skLineSegment(sketch, "E76.bottom", {"start": v(1332.47, -3371.57) * mm, "end": v(1363.47, -3371.57) * mm});
            skLineSegment(sketch, "E76.top", {"start": v(1332.47, -3531.57) * mm, "end": v(1340.55, -3531.57) * mm});
            skLineSegment(sketch, "E76.left", {"start": v(1326.47, -3387.57) * mm, "end": v(1326.47, -3515.57) * mm});
            skLineSegment(sketch, "E76.right", {"start": v(1369.47, -3387.57) * mm, "end": v(1369.47, -3515.57) * mm});
            skLineSegment(sketch, "E77.bottom", {"start": v(1341.72, -3371.57) * mm, "end": v(1354.22, -3371.57) * mm});
            skLineSegment(sketch, "E77.top", {"start": v(1343.63, -3361.07) * mm, "end": v(1352.31, -3361.07) * mm});
            skLineSegment(sketch, "E77.left", {"start": v(1341.72, -3371.57) * mm, "end": v(1342.64, -3361.98) * mm});
            skLineSegment(sketch, "E77.right", {"start": v(1354.22, -3371.57) * mm, "end": v(1353.31, -3361.98) * mm});
            skLineSegment(sketch, "E78.top", {"start": v(1343.4, -3519.57) * mm, "end": v(1352.55, -3519.57) * mm});
            skLineSegment(sketch, "E78.left", {"start": v(1341.55, -3530.66) * mm, "end": v(1342.4, -3520.5) * mm});
            skLineSegment(sketch, "E78.right", {"start": v(1354.4, -3530.66) * mm, "end": v(1353.55, -3520.5) * mm});
            skLineSegment(sketch, "E79", {"start": v(1332.47, -3371.57) * mm, "end": v(1326.47, -3387.57) * mm});
            skLineSegment(sketch, "E80", {"start": v(1363.47, -3371.57) * mm, "end": v(1369.47, -3387.57) * mm});
            skLineSegment(sketch, "E81.trimOffspring", {"start": v(1355.4, -3531.57) * mm, "end": v(1363.47, -3531.57) * mm});
            skLineSegment(sketch, "E82", {"start": v(1326.47, -3515.57) * mm, "end": v(1332.47, -3531.57) * mm});
            skLineSegment(sketch, "E83", {"start": v(1369.47, -3515.57) * mm, "end": v(1363.47, -3531.57) * mm});
            skPoint(sketch, "E84.visualSharp", {"position": v(1342.72, -3361.07) * mm});
            skArc(sketch, "E84.filletArc", {"start": v(1343.63, -3361.07) * mm, "mid": v(1342.96, -3361.33) * mm, "end": v(1342.64, -3361.98) * mm});
            skPoint(sketch, "E85.visualSharp", {"position": v(1353.22, -3361.07) * mm});
            skArc(sketch, "E85.filletArc", {"start": v(1353.31, -3361.98) * mm, "mid": v(1352.99, -3361.33) * mm, "end": v(1352.31, -3361.07) * mm});
            skPoint(sketch, "E86.visualSharp", {"position": v(1342.47, -3519.57) * mm});
            skArc(sketch, "E86.filletArc", {"start": v(1343.4, -3519.57) * mm, "mid": v(1342.72, -3519.84) * mm, "end": v(1342.4, -3520.5) * mm});
            skPoint(sketch, "E87.visualSharp", {"position": v(1353.47, -3519.57) * mm});
            skArc(sketch, "E87.filletArc", {"start": v(1353.55, -3520.5) * mm, "mid": v(1353.23, -3519.84) * mm, "end": v(1352.55, -3519.57) * mm});
            skPoint(sketch, "E88.visualSharp", {"position": v(1341.47, -3531.57) * mm});
            skArc(sketch, "E88.filletArc", {"start": v(1340.55, -3531.57) * mm, "mid": v(1341.23, -3531.3) * mm, "end": v(1341.55, -3530.66) * mm});
            skPoint(sketch, "E89.visualSharp", {"position": v(1354.47, -3531.57) * mm});
            skArc(sketch, "E89.filletArc", {"start": v(1354.4, -3530.66) * mm, "mid": v(1354.72, -3531.3) * mm, "end": v(1355.4, -3531.57) * mm});
            skSolve(sketch);
        }
        {
            var Q0;
            Q0=makeQuery(id+"F35.imprint","IMPRINT",FACE,{"disambiguationData":[TD([[makeQuery(id+"F35.imprint","IMPRINT",EDGE,{"derivedFrom":sQuery(id+"F35.wireOp",EDGE,"E76.top")}),1.0]])]});
            var Q1;
            Q1=makeQuery(id+"F35.imprint","IMPRINT",FACE,{"disambiguationData":[TD([[makeQuery(id+"F35.imprint","IMPRINT",EDGE,{"derivedFrom":sQuery(id+"F35.wireOp",EDGE,"E77.bottom")}),1.0]])]});
            extrude(context, id + "F36", {"entities" : qUnion([Q0, Q1]), "depth" : 5600 * mm, "offsetDistance" : 25 * mm});
        }
        {
            var Q0;
            Q0=makeQuery(id+"F36.opExtrude","SWEPT_FACE",FACE,{"disambiguationData":[OSD([sQuery(id+"F35.wireOp",EDGE,"E76.right")])]});
            var sketch = newSketch(context, id + "F37", { "sketchPlane" : qUnion([Q0])});
            skLineSegment(sketch, "E90.bottom", {"start": v(-3356.57, 5500) * mm, "end": v(-3411.57, 5500) * mm});
            skLineSegment(sketch, "E90.top", {"start": v(-3356.57, 5457) * mm, "end": v(-3411.57, 5457) * mm});
            skLineSegment(sketch, "E90.left", {"start": v(-3356.57, 5500) * mm, "end": v(-3356.57, 5457) * mm});
            skLineSegment(sketch, "E90.right", {"start": v(-3411.57, 5500) * mm, "end": v(-3411.57, 5457) * mm});
            skLineSegment(sketch, "E91.bottom", {"start": v(-3491.57, 5500) * mm, "end": v(-3541.57, 5500) * mm});
            skLineSegment(sketch, "E91.top", {"start": v(-3491.57, 5457) * mm, "end": v(-3541.57, 5457) * mm});
            skLineSegment(sketch, "E91.left", {"start": v(-3491.57, 5500) * mm, "end": v(-3491.57, 5457) * mm});
            skLineSegment(sketch, "E91.right", {"start": v(-3541.57, 5500) * mm, "end": v(-3541.57, 5457) * mm});
            skLineSegment(sketch, "E92.0.1.0", {"start": v(-3356.57, 143) * mm, "end": v(-3411.57, 143) * mm});
            skLineSegment(sketch, "E92.0.1.1", {"start": v(-3491.57, 143) * mm, "end": v(-3541.57, 143) * mm});
            skLineSegment(sketch, "E92.0.1.2", {"start": v(-3356.57, 143) * mm, "end": v(-3356.57, 100) * mm});
            skLineSegment(sketch, "E92.0.1.3", {"start": v(-3491.57, 100) * mm, "end": v(-3541.57, 100) * mm});
            skLineSegment(sketch, "E92.0.1.4", {"start": v(-3491.57, 143) * mm, "end": v(-3491.57, 100) * mm});
            skLineSegment(sketch, "E92.0.1.5", {"start": v(-3356.57, 100) * mm, "end": v(-3411.57, 100) * mm});
            skLineSegment(sketch, "E92.0.1.6", {"start": v(-3541.57, 143) * mm, "end": v(-3541.57, 100) * mm});
            skLineSegment(sketch, "E92.0.1.7", {"start": v(-3411.57, 143) * mm, "end": v(-3411.57, 100) * mm});
            skLineSegment(sketch, "E92.direction1", {"start": v(-3541.57, 5457) * mm, "end": v(-3516.57, 5457) * mm, "construction": true});
            skLineSegment(sketch, "E92.direction2", {"start": v(-3541.57, 5457) * mm, "end": v(-3541.57, 100) * mm, "construction": true});
            skSolve(sketch);
        }
        {
            var Q0;
            {var subQ0=sQuery(id+"F37.wireOp",EDGE,"E91.right");Q0=makeQuery(id+"F37.imprint","IMPRINT",FACE,{"disambiguationData":[TD([[makeQuery(id+"F37.imprint","IMPRINT",EDGE,{"derivedFrom":subQ0}),1.0]])]});}
            var Q1;
            {var subQ0=sQuery(id+"F37.wireOp",EDGE,"E91.left");Q1=makeQuery(id+"F37.imprint","IMPRINT",FACE,{"disambiguationData":[TD([[makeQuery(id+"F37.imprint","IMPRINT",EDGE,{"derivedFrom":subQ0}),-1.0]])]});}
            var Q2;
            {var subQ0=sQuery(id+"F37.wireOp",EDGE,"E90.right");Q2=makeQuery(id+"F37.imprint","IMPRINT",FACE,{"disambiguationData":[TD([[makeQuery(id+"F37.imprint","IMPRINT",EDGE,{"derivedFrom":subQ0}),1.0]])]});}
            var Q3;
            {var subQ0=sQuery(id+"F37.wireOp",EDGE,"E90.left");Q3=makeQuery(id+"F37.imprint","IMPRINT",FACE,{"disambiguationData":[TD([[makeQuery(id+"F37.imprint","IMPRINT",EDGE,{"derivedFrom":subQ0}),-1.0]])]});}
            var Q4;
            {var subQ0=sQuery(id+"F37.wireOp",EDGE,"E92.0.1.4");Q4=makeQuery(id+"F37.imprint","IMPRINT",FACE,{"disambiguationData":[TD([[makeQuery(id+"F37.imprint","IMPRINT",EDGE,{"derivedFrom":subQ0}),-1.0]])]});}
            var Q5;
            {var subQ0=sQuery(id+"F37.wireOp",EDGE,"E92.0.1.6");Q5=makeQuery(id+"F37.imprint","IMPRINT",FACE,{"disambiguationData":[TD([[makeQuery(id+"F37.imprint","IMPRINT",EDGE,{"derivedFrom":subQ0}),1.0]])]});}
            var Q6;
            {var subQ0=sQuery(id+"F37.wireOp",EDGE,"E92.0.1.7");Q6=makeQuery(id+"F37.imprint","IMPRINT",FACE,{"disambiguationData":[TD([[makeQuery(id+"F37.imprint","IMPRINT",EDGE,{"derivedFrom":subQ0}),1.0]])]});}
            var Q7;
            {var subQ0=sQuery(id+"F37.wireOp",EDGE,"E92.0.1.2");Q7=makeQuery(id+"F37.imprint","IMPRINT",FACE,{"disambiguationData":[TD([[makeQuery(id+"F37.imprint","IMPRINT",EDGE,{"derivedFrom":subQ0}),-1.0]])]});}
            extrude(context, id + "F38", {"entities" : qUnion([Q0, Q1, Q2, Q3, Q4, Q5, Q6, Q7]), "operationType" : NewBodyOperationType.REMOVE, "oppositeDirection" : true, "depth" : 55 * mm, "offsetDistance" : 25 * mm});
        }
        {
            var Q0;
            {var subQ8=sQuery(id+"F34.wireOp",EDGE,"E43.0");Q0=makeQuery(id+"F34.imprint","IMPRINT",FACE,{"disambiguationData":[TD([[makeQuery(id+"F34.imprint","IMPRINT",EDGE,{"derivedFrom":subQ8}),1.0]])]});}
            var sketch = newSketch(context, id + "F39", { "sketchPlane" : qUnion([Q0])});
            skLineSegment(sketch, "E93.bottom", {"start": v(1305.13, -3790.55) * mm, "end": v(1336.13, -3790.55) * mm});
            skLineSegment(sketch, "E93.top", {"start": v(1305.13, -3950.55) * mm, "end": v(1313.2, -3950.55) * mm});
            skLineSegment(sketch, "E93.left", {"start": v(1299.13, -3806.55) * mm, "end": v(1299.13, -3934.55) * mm});
            skLineSegment(sketch, "E93.right", {"start": v(1342.13, -3806.55) * mm, "end": v(1342.13, -3934.55) * mm});
            skLineSegment(sketch, "E94.bottom", {"start": v(1314.38, -3790.55) * mm, "end": v(1326.88, -3790.55) * mm});
            skLineSegment(sketch, "E94.top", {"start": v(1316.29, -3780.05) * mm, "end": v(1324.97, -3780.05) * mm});
            skLineSegment(sketch, "E94.left", {"start": v(1314.38, -3790.55) * mm, "end": v(1315.3, -3780.95) * mm});
            skLineSegment(sketch, "E94.right", {"start": v(1326.88, -3790.55) * mm, "end": v(1325.96, -3780.95) * mm});
            skLineSegment(sketch, "E95.top", {"start": v(1316.05, -3938.55) * mm, "end": v(1325.2, -3938.55) * mm});
            skLineSegment(sketch, "E95.left", {"start": v(1314.2, -3949.63) * mm, "end": v(1315.05, -3939.47) * mm});
            skLineSegment(sketch, "E95.right", {"start": v(1327.05, -3949.63) * mm, "end": v(1326.2, -3939.47) * mm});
            skLineSegment(sketch, "E96", {"start": v(1305.13, -3790.55) * mm, "end": v(1299.13, -3806.55) * mm});
            skLineSegment(sketch, "E97", {"start": v(1336.13, -3790.55) * mm, "end": v(1342.13, -3806.55) * mm});
            skLineSegment(sketch, "E98.trimOffspring", {"start": v(1328.05, -3950.55) * mm, "end": v(1336.13, -3950.55) * mm});
            skLineSegment(sketch, "E99", {"start": v(1299.13, -3934.55) * mm, "end": v(1305.13, -3950.55) * mm});
            skLineSegment(sketch, "E100", {"start": v(1342.13, -3934.55) * mm, "end": v(1336.13, -3950.55) * mm});
            skPoint(sketch, "E101.visualSharp", {"position": v(1315.38, -3780.05) * mm});
            skArc(sketch, "E101.filletArc", {"start": v(1316.29, -3780.05) * mm, "mid": v(1315.62, -3780.3) * mm, "end": v(1315.3, -3780.95) * mm});
            skPoint(sketch, "E102.visualSharp", {"position": v(1325.88, -3780.05) * mm});
            skArc(sketch, "E102.filletArc", {"start": v(1325.96, -3780.95) * mm, "mid": v(1325.64, -3780.3) * mm, "end": v(1324.97, -3780.05) * mm});
            skPoint(sketch, "E103.visualSharp", {"position": v(1315.13, -3938.55) * mm});
            skArc(sketch, "E103.filletArc", {"start": v(1316.05, -3938.55) * mm, "mid": v(1315.37, -3938.81) * mm, "end": v(1315.05, -3939.47) * mm});
            skPoint(sketch, "E104.visualSharp", {"position": v(1326.13, -3938.55) * mm});
            skArc(sketch, "E104.filletArc", {"start": v(1326.2, -3939.47) * mm, "mid": v(1325.89, -3938.81) * mm, "end": v(1325.2, -3938.55) * mm});
            skPoint(sketch, "E105.visualSharp", {"position": v(1314.13, -3950.55) * mm});
            skArc(sketch, "E105.filletArc", {"start": v(1313.2, -3950.55) * mm, "mid": v(1313.89, -3950.28) * mm, "end": v(1314.2, -3949.63) * mm});
            skPoint(sketch, "E106.visualSharp", {"position": v(1327.13, -3950.55) * mm});
            skArc(sketch, "E106.filletArc", {"start": v(1327.05, -3949.63) * mm, "mid": v(1327.37, -3950.28) * mm, "end": v(1328.05, -3950.55) * mm});
            skSolve(sketch);
        }
        {
            var Q0;
            Q0=makeQuery(id+"F39.imprint","IMPRINT",FACE,{"disambiguationData":[TD([[makeQuery(id+"F39.imprint","IMPRINT",EDGE,{"derivedFrom":sQuery(id+"F39.wireOp",EDGE,"E93.top")}),1.0]])]});
            var Q1;
            Q1=makeQuery(id+"F39.imprint","IMPRINT",FACE,{"disambiguationData":[TD([[makeQuery(id+"F39.imprint","IMPRINT",EDGE,{"derivedFrom":sQuery(id+"F39.wireOp",EDGE,"E94.bottom")}),1.0]])]});
            extrude(context, id + "F40", {"entities" : qUnion([Q0, Q1]), "depth" : 3200 * mm, "offsetDistance" : 25 * mm});
        }
        {
            var Q0;
            Q0=makeQuery(id+"F40.opExtrude","SWEPT_FACE",FACE,{"disambiguationData":[OSD([sQuery(id+"F39.wireOp",EDGE,"E93.right")])]});
            var sketch = newSketch(context, id + "F41", { "sketchPlane" : qUnion([Q0])});
            skLineSegment(sketch, "E107.bottom", {"start": v(-3775.55, 3100) * mm, "end": v(-3830.55, 3100) * mm});
            skLineSegment(sketch, "E107.top", {"start": v(-3775.55, 3057) * mm, "end": v(-3830.55, 3057) * mm});
            skLineSegment(sketch, "E107.left", {"start": v(-3775.55, 3100) * mm, "end": v(-3775.55, 3057) * mm});
            skLineSegment(sketch, "E107.right", {"start": v(-3830.55, 3100) * mm, "end": v(-3830.55, 3057) * mm});
            skLineSegment(sketch, "E108.bottom", {"start": v(-3910.55, 3100) * mm, "end": v(-3965.55, 3100) * mm});
            skLineSegment(sketch, "E108.top", {"start": v(-3910.55, 3057) * mm, "end": v(-3965.55, 3057) * mm});
            skLineSegment(sketch, "E108.left", {"start": v(-3910.55, 3100) * mm, "end": v(-3910.55, 3057) * mm});
            skLineSegment(sketch, "E108.right", {"start": v(-3965.55, 3100) * mm, "end": v(-3965.55, 3057) * mm});
            skLineSegment(sketch, "E109.0.1.0", {"start": v(-3910.55, 143) * mm, "end": v(-3965.55, 143) * mm});
            skLineSegment(sketch, "E109.0.1.1", {"start": v(-3775.55, 100) * mm, "end": v(-3830.55, 100) * mm});
            skLineSegment(sketch, "E109.0.1.2", {"start": v(-3775.55, 143) * mm, "end": v(-3830.55, 143) * mm});
            skLineSegment(sketch, "E109.0.1.3", {"start": v(-3910.55, 100) * mm, "end": v(-3965.55, 100) * mm});
            skLineSegment(sketch, "E109.0.1.4", {"start": v(-3775.55, 143) * mm, "end": v(-3775.55, 100) * mm});
            skLineSegment(sketch, "E109.0.1.5", {"start": v(-3965.55, 143) * mm, "end": v(-3965.55, 100) * mm});
            skLineSegment(sketch, "E109.0.1.6", {"start": v(-3910.55, 143) * mm, "end": v(-3910.55, 100) * mm});
            skLineSegment(sketch, "E109.0.1.7", {"start": v(-3830.55, 143) * mm, "end": v(-3830.55, 100) * mm});
            skLineSegment(sketch, "E109.direction1", {"start": v(-3965.55, 3057) * mm, "end": v(-3940.55, 3057) * mm, "construction": true});
            skLineSegment(sketch, "E109.direction2", {"start": v(-3965.55, 3057) * mm, "end": v(-3965.55, 100) * mm, "construction": true});
            skSolve(sketch);
        }
        {
            var Q0;
            {var subQ0=sQuery(id+"F41.wireOp",EDGE,"E107.left");Q0=makeQuery(id+"F41.imprint","IMPRINT",FACE,{"disambiguationData":[TD([[makeQuery(id+"F41.imprint","IMPRINT",EDGE,{"derivedFrom":subQ0}),-1.0]])]});}
            var Q1;
            {var subQ0=sQuery(id+"F41.wireOp",EDGE,"E107.right");Q1=makeQuery(id+"F41.imprint","IMPRINT",FACE,{"disambiguationData":[TD([[makeQuery(id+"F41.imprint","IMPRINT",EDGE,{"derivedFrom":subQ0}),1.0]])]});}
            var Q2;
            {var subQ0=sQuery(id+"F41.wireOp",EDGE,"E108.left");Q2=makeQuery(id+"F41.imprint","IMPRINT",FACE,{"disambiguationData":[TD([[makeQuery(id+"F41.imprint","IMPRINT",EDGE,{"derivedFrom":subQ0}),-1.0]])]});}
            var Q3;
            {var subQ0=sQuery(id+"F41.wireOp",EDGE,"E108.right");Q3=makeQuery(id+"F41.imprint","IMPRINT",FACE,{"disambiguationData":[TD([[makeQuery(id+"F41.imprint","IMPRINT",EDGE,{"derivedFrom":subQ0}),1.0]])]});}
            var Q4;
            {var subQ0=sQuery(id+"F41.wireOp",EDGE,"E109.0.1.4");Q4=makeQuery(id+"F41.imprint","IMPRINT",FACE,{"disambiguationData":[TD([[makeQuery(id+"F41.imprint","IMPRINT",EDGE,{"derivedFrom":subQ0}),-1.0]])]});}
            var Q5;
            {var subQ0=sQuery(id+"F41.wireOp",EDGE,"E109.0.1.7");Q5=makeQuery(id+"F41.imprint","IMPRINT",FACE,{"disambiguationData":[TD([[makeQuery(id+"F41.imprint","IMPRINT",EDGE,{"derivedFrom":subQ0}),1.0]])]});}
            var Q6;
            {var subQ0=sQuery(id+"F41.wireOp",EDGE,"E109.0.1.5");Q6=makeQuery(id+"F41.imprint","IMPRINT",FACE,{"disambiguationData":[TD([[makeQuery(id+"F41.imprint","IMPRINT",EDGE,{"derivedFrom":subQ0}),1.0]])]});}
            var Q7;
            {var subQ0=sQuery(id+"F41.wireOp",EDGE,"E109.0.1.6");Q7=makeQuery(id+"F41.imprint","IMPRINT",FACE,{"disambiguationData":[TD([[makeQuery(id+"F41.imprint","IMPRINT",EDGE,{"derivedFrom":subQ0}),-1.0]])]});}
            extrude(context, id + "F42", {"entities" : qUnion([Q0, Q1, Q2, Q3, Q4, Q5, Q6, Q7]), "operationType" : NewBodyOperationType.REMOVE, "oppositeDirection" : true, "depth" : 55 * mm, "offsetDistance" : 25 * mm});
        }
        {
            var Q0;
            {var subQ8=sQuery(id+"F34.wireOp",EDGE,"E43.0");Q0=makeQuery(id+"F34.imprint","IMPRINT",FACE,{"disambiguationData":[TD([[makeQuery(id+"F34.imprint","IMPRINT",EDGE,{"derivedFrom":subQ8}),1.0]])]});}
            var sketch = newSketch(context, id + "F43", { "sketchPlane" : qUnion([Q0])});
            skLineSegment(sketch, "E110.bottom", {"start": v(1638.86, -3331.42) * mm, "end": v(1669.86, -3331.42) * mm});
            skLineSegment(sketch, "E110.top", {"start": v(1638.86, -3491.42) * mm, "end": v(1646.94, -3491.42) * mm});
            skLineSegment(sketch, "E110.left", {"start": v(1632.86, -3347.42) * mm, "end": v(1632.86, -3475.42) * mm});
            skLineSegment(sketch, "E110.right", {"start": v(1675.86, -3347.42) * mm, "end": v(1675.86, -3475.42) * mm});
            skLineSegment(sketch, "E111.bottom", {"start": v(1648.11, -3331.42) * mm, "end": v(1660.61, -3331.42) * mm});
            skLineSegment(sketch, "E111.top", {"start": v(1650.02, -3320.92) * mm, "end": v(1658.7, -3320.92) * mm});
            skLineSegment(sketch, "E111.left", {"start": v(1648.11, -3331.42) * mm, "end": v(1649.03, -3321.82) * mm});
            skLineSegment(sketch, "E111.right", {"start": v(1660.61, -3331.42) * mm, "end": v(1659.7, -3321.82) * mm});
            skLineSegment(sketch, "E112.top", {"start": v(1649.78, -3479.42) * mm, "end": v(1658.94, -3479.42) * mm});
            skLineSegment(sketch, "E112.left", {"start": v(1647.94, -3490.5) * mm, "end": v(1648.79, -3480.33) * mm});
            skLineSegment(sketch, "E112.right", {"start": v(1660.79, -3490.5) * mm, "end": v(1659.94, -3480.33) * mm});
            skLineSegment(sketch, "E113", {"start": v(1638.86, -3331.42) * mm, "end": v(1632.86, -3347.42) * mm});
            skLineSegment(sketch, "E114", {"start": v(1669.86, -3331.42) * mm, "end": v(1675.86, -3347.42) * mm});
            skLineSegment(sketch, "E115.trimOffspring", {"start": v(1661.78, -3491.42) * mm, "end": v(1669.86, -3491.42) * mm});
            skLineSegment(sketch, "E116", {"start": v(1632.86, -3475.42) * mm, "end": v(1638.86, -3491.42) * mm});
            skLineSegment(sketch, "E117", {"start": v(1675.86, -3475.42) * mm, "end": v(1669.86, -3491.42) * mm});
            skPoint(sketch, "E118.visualSharp", {"position": v(1649.11, -3320.92) * mm});
            skArc(sketch, "E118.filletArc", {"start": v(1650.02, -3320.92) * mm, "mid": v(1649.35, -3321.18) * mm, "end": v(1649.03, -3321.82) * mm});
            skPoint(sketch, "E119.visualSharp", {"position": v(1659.61, -3320.92) * mm});
            skArc(sketch, "E119.filletArc", {"start": v(1659.7, -3321.82) * mm, "mid": v(1659.38, -3321.18) * mm, "end": v(1658.7, -3320.92) * mm});
            skPoint(sketch, "E120.visualSharp", {"position": v(1648.86, -3479.42) * mm});
            skArc(sketch, "E120.filletArc", {"start": v(1649.78, -3479.42) * mm, "mid": v(1649.1, -3479.68) * mm, "end": v(1648.79, -3480.33) * mm});
            skPoint(sketch, "E121.visualSharp", {"position": v(1659.86, -3479.42) * mm});
            skArc(sketch, "E121.filletArc", {"start": v(1659.94, -3480.33) * mm, "mid": v(1659.62, -3479.68) * mm, "end": v(1658.94, -3479.42) * mm});
            skPoint(sketch, "E122.visualSharp", {"position": v(1647.86, -3491.42) * mm});
            skArc(sketch, "E122.filletArc", {"start": v(1646.94, -3491.42) * mm, "mid": v(1647.62, -3491.15) * mm, "end": v(1647.94, -3490.5) * mm});
            skPoint(sketch, "E123.visualSharp", {"position": v(1660.86, -3491.42) * mm});
            skArc(sketch, "E123.filletArc", {"start": v(1660.79, -3490.5) * mm, "mid": v(1661.1, -3491.15) * mm, "end": v(1661.78, -3491.42) * mm});
            skSolve(sketch);
        }
        {
            var Q0;
            Q0=makeQuery(id+"F43.imprint","IMPRINT",FACE,{"disambiguationData":[TD([[makeQuery(id+"F43.imprint","IMPRINT",EDGE,{"derivedFrom":sQuery(id+"F43.wireOp",EDGE,"E110.top")}),1.0]])]});
            var Q1;
            Q1=makeQuery(id+"F43.imprint","IMPRINT",FACE,{"disambiguationData":[TD([[makeQuery(id+"F43.imprint","IMPRINT",EDGE,{"derivedFrom":sQuery(id+"F43.wireOp",EDGE,"E111.bottom")}),1.0]])]});
            extrude(context, id + "F44", {"entities" : qUnion([Q0, Q1]), "depth" : 4300 * mm, "offsetDistance" : 25 * mm});
        }
        {
            var Q0;
            Q0=makeQuery(id+"F44.opExtrude","SWEPT_FACE",FACE,{"disambiguationData":[OSD([sQuery(id+"F43.wireOp",EDGE,"E110.right")])]});
            var sketch = newSketch(context, id + "F45", { "sketchPlane" : qUnion([Q0])});
            skLineSegment(sketch, "E124.bottom", {"start": v(-3316.42, 4200) * mm, "end": v(-3371.42, 4200) * mm});
            skLineSegment(sketch, "E124.top", {"start": v(-3316.42, 4157) * mm, "end": v(-3371.42, 4157) * mm});
            skLineSegment(sketch, "E124.left", {"start": v(-3316.42, 4200) * mm, "end": v(-3316.42, 4157) * mm});
            skLineSegment(sketch, "E124.right", {"start": v(-3371.42, 4200) * mm, "end": v(-3371.42, 4157) * mm});
            skLineSegment(sketch, "E125.bottom", {"start": v(-3451.42, 4200) * mm, "end": v(-3506.42, 4200) * mm});
            skLineSegment(sketch, "E125.top", {"start": v(-3451.42, 4157) * mm, "end": v(-3506.42, 4157) * mm});
            skLineSegment(sketch, "E125.left", {"start": v(-3451.42, 4200) * mm, "end": v(-3451.42, 4157) * mm});
            skLineSegment(sketch, "E125.right", {"start": v(-3506.42, 4200) * mm, "end": v(-3506.42, 4157) * mm});
            skSolve(sketch);
        }
        {
            var Q0;
            {var subQ0=sQuery(id+"F45.wireOp",EDGE,"E124.left");Q0=makeQuery(id+"F45.imprint","IMPRINT",FACE,{"disambiguationData":[TD([[makeQuery(id+"F45.imprint","IMPRINT",EDGE,{"derivedFrom":subQ0}),-1.0]])]});}
            var Q1;
            {var subQ0=sQuery(id+"F45.wireOp",EDGE,"E124.right");Q1=makeQuery(id+"F45.imprint","IMPRINT",FACE,{"disambiguationData":[TD([[makeQuery(id+"F45.imprint","IMPRINT",EDGE,{"derivedFrom":subQ0}),1.0]])]});}
            var Q2;
            {var subQ0=sQuery(id+"F45.wireOp",EDGE,"E125.left");Q2=makeQuery(id+"F45.imprint","IMPRINT",FACE,{"disambiguationData":[TD([[makeQuery(id+"F45.imprint","IMPRINT",EDGE,{"derivedFrom":subQ0}),-1.0]])]});}
            var Q3;
            {var subQ0=sQuery(id+"F45.wireOp",EDGE,"E125.right");Q3=makeQuery(id+"F45.imprint","IMPRINT",FACE,{"disambiguationData":[TD([[makeQuery(id+"F45.imprint","IMPRINT",EDGE,{"derivedFrom":subQ0}),1.0]])]});}
            extrude(context, id + "F46", {"entities" : qUnion([Q0, Q1, Q2, Q3]), "operationType" : NewBodyOperationType.REMOVE, "oppositeDirection" : true, "depth" : 55 * mm, "offsetDistance" : 25 * mm});
        }
        {
            var Q0;
            {var subQ8=sQuery(id+"F34.wireOp",EDGE,"E43.0");Q0=makeQuery(id+"F34.imprint","IMPRINT",FACE,{"disambiguationData":[TD([[makeQuery(id+"F34.imprint","IMPRINT",EDGE,{"derivedFrom":subQ8}),1.0]])]});}
            var Q1;
            {var subQ8=sQuery(id+"F34.wireOp",EDGE,"E43.0");Q1=makeQuery(id+"F34.imprint","IMPRINT",FACE,{"disambiguationData":[TD([[makeQuery(id+"F34.imprint","IMPRINT",EDGE,{"derivedFrom":subQ8}),1.0]])]});}
            var sketch = newSketch(context, id + "F47", { "sketchPlane" : qUnion([Q0, Q1])});
            skLineSegment(sketch, "E126.bottom", {"start": v(1928.31, -3313.54) * mm, "end": v(1959.31, -3313.54) * mm});
            skLineSegment(sketch, "E126.top", {"start": v(1928.31, -3473.54) * mm, "end": v(1936.4, -3473.54) * mm});
            skLineSegment(sketch, "E126.left", {"start": v(1922.31, -3329.54) * mm, "end": v(1922.31, -3457.54) * mm});
            skLineSegment(sketch, "E126.right", {"start": v(1965.31, -3329.54) * mm, "end": v(1965.31, -3457.54) * mm});
            skLineSegment(sketch, "E127.bottom", {"start": v(1937.56, -3313.54) * mm, "end": v(1950.06, -3313.54) * mm});
            skLineSegment(sketch, "E127.top", {"start": v(1939.47, -3303.04) * mm, "end": v(1948.15, -3303.04) * mm});
            skLineSegment(sketch, "E127.left", {"start": v(1937.56, -3313.54) * mm, "end": v(1938.47, -3303.94) * mm});
            skLineSegment(sketch, "E127.right", {"start": v(1950.06, -3313.54) * mm, "end": v(1949.15, -3303.94) * mm});
            skLineSegment(sketch, "E128.top", {"start": v(1939.23, -3461.54) * mm, "end": v(1948.4, -3461.54) * mm});
            skLineSegment(sketch, "E128.left", {"start": v(1937.39, -3472.62) * mm, "end": v(1938.23, -3462.45) * mm});
            skLineSegment(sketch, "E128.right", {"start": v(1950.23, -3472.62) * mm, "end": v(1949.39, -3462.45) * mm});
            skLineSegment(sketch, "E129", {"start": v(1928.31, -3313.54) * mm, "end": v(1922.31, -3329.54) * mm});
            skLineSegment(sketch, "E130", {"start": v(1959.31, -3313.54) * mm, "end": v(1965.31, -3329.54) * mm});
            skLineSegment(sketch, "E131.trimOffspring", {"start": v(1951.23, -3473.54) * mm, "end": v(1959.31, -3473.54) * mm});
            skLineSegment(sketch, "E132", {"start": v(1922.31, -3457.54) * mm, "end": v(1928.31, -3473.54) * mm});
            skLineSegment(sketch, "E133", {"start": v(1965.31, -3457.54) * mm, "end": v(1959.31, -3473.54) * mm});
            skPoint(sketch, "E134.visualSharp", {"position": v(1938.56, -3303.04) * mm});
            skArc(sketch, "E134.filletArc", {"start": v(1939.47, -3303.04) * mm, "mid": v(1938.8, -3303.3) * mm, "end": v(1938.47, -3303.94) * mm});
            skPoint(sketch, "E135.visualSharp", {"position": v(1949.06, -3303.04) * mm});
            skArc(sketch, "E135.filletArc", {"start": v(1949.15, -3303.94) * mm, "mid": v(1948.82, -3303.3) * mm, "end": v(1948.15, -3303.04) * mm});
            skPoint(sketch, "E136.visualSharp", {"position": v(1938.31, -3461.54) * mm});
            skArc(sketch, "E136.filletArc", {"start": v(1939.23, -3461.54) * mm, "mid": v(1938.55, -3461.8) * mm, "end": v(1938.23, -3462.45) * mm});
            skPoint(sketch, "E137.visualSharp", {"position": v(1949.31, -3461.54) * mm});
            skArc(sketch, "E137.filletArc", {"start": v(1949.39, -3462.45) * mm, "mid": v(1949.07, -3461.8) * mm, "end": v(1948.4, -3461.54) * mm});
            skPoint(sketch, "E138.visualSharp", {"position": v(1937.31, -3473.54) * mm});
            skArc(sketch, "E138.filletArc", {"start": v(1936.4, -3473.54) * mm, "mid": v(1937.07, -3473.27) * mm, "end": v(1937.39, -3472.62) * mm});
            skPoint(sketch, "E139.visualSharp", {"position": v(1950.31, -3473.54) * mm});
            skArc(sketch, "E139.filletArc", {"start": v(1950.23, -3472.62) * mm, "mid": v(1950.55, -3473.27) * mm, "end": v(1951.23, -3473.54) * mm});
            skSolve(sketch);
        }
        {
            var Q0;
            Q0=makeQuery(id+"F47.imprint","IMPRINT",FACE,{"disambiguationData":[TD([[makeQuery(id+"F47.imprint","IMPRINT",EDGE,{"derivedFrom":sQuery(id+"F47.wireOp",EDGE,"E126.top")}),1.0]])]});
            var Q1;
            Q1=makeQuery(id+"F47.imprint","IMPRINT",FACE,{"disambiguationData":[TD([[makeQuery(id+"F47.imprint","IMPRINT",EDGE,{"derivedFrom":sQuery(id+"F47.wireOp",EDGE,"E127.bottom")}),1.0]])]});
            extrude(context, id + "F48", {"entities" : qUnion([Q0, Q1]), "depth" : 1300 * mm, "offsetDistance" : 25 * mm});
        }
        {
            var Q0;
            Q0=makeQuery(id+"F48.opExtrude","SWEPT_FACE",FACE,{"disambiguationData":[OSD([sQuery(id+"F47.wireOp",EDGE,"E126.right")])]});
            var sketch = newSketch(context, id + "F49", { "sketchPlane" : qUnion([Q0])});
            skLineSegment(sketch, "E140.bottom", {"start": v(-3298.54, 1200) * mm, "end": v(-3353.54, 1200) * mm});
            skLineSegment(sketch, "E140.top", {"start": v(-3298.54, 1157) * mm, "end": v(-3353.54, 1157) * mm});
            skLineSegment(sketch, "E140.left", {"start": v(-3298.54, 1200) * mm, "end": v(-3298.54, 1157) * mm});
            skLineSegment(sketch, "E140.right", {"start": v(-3353.54, 1200) * mm, "end": v(-3353.54, 1157) * mm});
            skLineSegment(sketch, "E141.bottom", {"start": v(-3433.54, 1200) * mm, "end": v(-3488.54, 1200) * mm});
            skLineSegment(sketch, "E141.top", {"start": v(-3433.54, 1157) * mm, "end": v(-3488.54, 1157) * mm});
            skLineSegment(sketch, "E141.left", {"start": v(-3433.54, 1200) * mm, "end": v(-3433.54, 1157) * mm});
            skLineSegment(sketch, "E141.right", {"start": v(-3488.54, 1200) * mm, "end": v(-3488.54, 1157) * mm});
            skSolve(sketch);
        }
        {
            var Q0;
            {var subQ0=sQuery(id+"F49.wireOp",EDGE,"E140.left");Q0=makeQuery(id+"F49.imprint","IMPRINT",FACE,{"disambiguationData":[TD([[makeQuery(id+"F49.imprint","IMPRINT",EDGE,{"derivedFrom":subQ0}),-1.0]])]});}
            var Q1;
            {var subQ0=sQuery(id+"F49.wireOp",EDGE,"E140.right");Q1=makeQuery(id+"F49.imprint","IMPRINT",FACE,{"disambiguationData":[TD([[makeQuery(id+"F49.imprint","IMPRINT",EDGE,{"derivedFrom":subQ0}),1.0]])]});}
            var Q2;
            {var subQ0=sQuery(id+"F49.wireOp",EDGE,"E141.left");Q2=makeQuery(id+"F49.imprint","IMPRINT",FACE,{"disambiguationData":[TD([[makeQuery(id+"F49.imprint","IMPRINT",EDGE,{"derivedFrom":subQ0}),-1.0]])]});}
            var Q3;
            {var subQ0=sQuery(id+"F49.wireOp",EDGE,"E141.right");Q3=makeQuery(id+"F49.imprint","IMPRINT",FACE,{"disambiguationData":[TD([[makeQuery(id+"F49.imprint","IMPRINT",EDGE,{"derivedFrom":subQ0}),1.0]])]});}
            extrude(context, id + "F50", {"entities" : qUnion([Q0, Q1, Q2, Q3]), "operationType" : NewBodyOperationType.REMOVE, "oppositeDirection" : true, "depth" : 55 * mm, "offsetDistance" : 25 * mm});
        }
        {
            var Q0;
            {var subQ8=sQuery(id+"F34.wireOp",EDGE,"E43.0");Q0=makeQuery(id+"F34.imprint","IMPRINT",FACE,{"disambiguationData":[TD([[makeQuery(id+"F34.imprint","IMPRINT",EDGE,{"derivedFrom":subQ8}),1.0]])]});}
            var sketch = newSketch(context, id + "F51", { "sketchPlane" : qUnion([Q0])});
            skLineSegment(sketch, "E142.bottom", {"start": v(2178.28, -3287.77) * mm, "end": v(2209.28, -3287.77) * mm});
            skLineSegment(sketch, "E142.top", {"start": v(2178.28, -3447.77) * mm, "end": v(2186.36, -3447.77) * mm});
            skLineSegment(sketch, "E142.left", {"start": v(2172.28, -3303.77) * mm, "end": v(2172.28, -3431.77) * mm});
            skLineSegment(sketch, "E142.right", {"start": v(2215.28, -3303.77) * mm, "end": v(2215.28, -3431.77) * mm});
            skLineSegment(sketch, "E143.bottom", {"start": v(2187.53, -3287.77) * mm, "end": v(2200.03, -3287.77) * mm});
            skLineSegment(sketch, "E143.top", {"start": v(2189.44, -3277.27) * mm, "end": v(2198.12, -3277.27) * mm});
            skLineSegment(sketch, "E143.left", {"start": v(2187.53, -3287.77) * mm, "end": v(2188.44, -3278.17) * mm});
            skLineSegment(sketch, "E143.right", {"start": v(2200.03, -3287.77) * mm, "end": v(2199.11, -3278.17) * mm});
            skLineSegment(sketch, "E144.top", {"start": v(2189.2, -3435.77) * mm, "end": v(2198.36, -3435.77) * mm});
            skLineSegment(sketch, "E144.left", {"start": v(2187.35, -3446.85) * mm, "end": v(2188.2, -3436.69) * mm});
            skLineSegment(sketch, "E144.right", {"start": v(2200.2, -3446.85) * mm, "end": v(2199.35, -3436.69) * mm});
            skLineSegment(sketch, "E145", {"start": v(2178.28, -3287.77) * mm, "end": v(2172.28, -3303.77) * mm});
            skLineSegment(sketch, "E146", {"start": v(2209.28, -3287.77) * mm, "end": v(2215.28, -3303.77) * mm});
            skLineSegment(sketch, "E147.trimOffspring", {"start": v(2201.2, -3447.77) * mm, "end": v(2209.28, -3447.77) * mm});
            skLineSegment(sketch, "E148", {"start": v(2172.28, -3431.77) * mm, "end": v(2178.28, -3447.77) * mm});
            skLineSegment(sketch, "E149", {"start": v(2215.28, -3431.77) * mm, "end": v(2209.28, -3447.77) * mm});
            skPoint(sketch, "E150.visualSharp", {"position": v(2188.53, -3277.27) * mm});
            skArc(sketch, "E150.filletArc", {"start": v(2189.44, -3277.27) * mm, "mid": v(2188.76, -3277.53) * mm, "end": v(2188.44, -3278.17) * mm});
            skPoint(sketch, "E151.visualSharp", {"position": v(2199.03, -3277.27) * mm});
            skArc(sketch, "E151.filletArc", {"start": v(2199.11, -3278.17) * mm, "mid": v(2198.8, -3277.53) * mm, "end": v(2198.12, -3277.27) * mm});
            skPoint(sketch, "E152.visualSharp", {"position": v(2188.28, -3435.77) * mm});
            skArc(sketch, "E152.filletArc", {"start": v(2189.2, -3435.77) * mm, "mid": v(2188.52, -3436.03) * mm, "end": v(2188.2, -3436.69) * mm});
            skPoint(sketch, "E153.visualSharp", {"position": v(2199.28, -3435.77) * mm});
            skArc(sketch, "E153.filletArc", {"start": v(2199.35, -3436.69) * mm, "mid": v(2199.03, -3436.03) * mm, "end": v(2198.36, -3435.77) * mm});
            skPoint(sketch, "E154.visualSharp", {"position": v(2187.28, -3447.77) * mm});
            skArc(sketch, "E154.filletArc", {"start": v(2186.36, -3447.77) * mm, "mid": v(2187.03, -3447.5) * mm, "end": v(2187.35, -3446.85) * mm});
            skPoint(sketch, "E155.visualSharp", {"position": v(2200.28, -3447.77) * mm});
            skArc(sketch, "E155.filletArc", {"start": v(2200.2, -3446.85) * mm, "mid": v(2200.52, -3447.5) * mm, "end": v(2201.2, -3447.77) * mm});
            skSolve(sketch);
        }
        {
            var Q0;
            Q0=makeQuery(id+"F51.imprint","IMPRINT",FACE,{"disambiguationData":[TD([[makeQuery(id+"F51.imprint","IMPRINT",EDGE,{"derivedFrom":sQuery(id+"F51.wireOp",EDGE,"E142.top")}),1.0]])]});
            var Q1;
            Q1=makeQuery(id+"F51.imprint","IMPRINT",FACE,{"disambiguationData":[TD([[makeQuery(id+"F51.imprint","IMPRINT",EDGE,{"derivedFrom":sQuery(id+"F51.wireOp",EDGE,"E143.bottom")}),1.0]])]});
            extrude(context, id + "F52", {"entities" : qUnion([Q0, Q1]), "depth" : 1200 * mm, "offsetDistance" : 25 * mm});
        }
        {
            var Q0;
            {var subQ8=sQuery(id+"F34.wireOp",EDGE,"E43.0");Q0=makeQuery(id+"F34.imprint","IMPRINT",FACE,{"disambiguationData":[TD([[makeQuery(id+"F34.imprint","IMPRINT",EDGE,{"derivedFrom":subQ8}),1.0]])]});}
            var sketch = newSketch(context, id + "F53", { "sketchPlane" : qUnion([Q0])});
            skLineSegment(sketch, "E156.bottom", {"start": v(2320.67, -3244.57) * mm, "end": v(2351.67, -3244.57) * mm});
            skLineSegment(sketch, "E156.top", {"start": v(2320.67, -3404.57) * mm, "end": v(2328.75, -3404.57) * mm});
            skLineSegment(sketch, "E156.left", {"start": v(2314.67, -3260.57) * mm, "end": v(2314.67, -3388.57) * mm});
            skLineSegment(sketch, "E156.right", {"start": v(2357.67, -3260.57) * mm, "end": v(2357.67, -3388.57) * mm});
            skLineSegment(sketch, "E157.bottom", {"start": v(2329.92, -3244.57) * mm, "end": v(2342.42, -3244.57) * mm});
            skLineSegment(sketch, "E157.top", {"start": v(2331.82, -3234.07) * mm, "end": v(2340.5, -3234.07) * mm});
            skLineSegment(sketch, "E157.left", {"start": v(2329.92, -3244.57) * mm, "end": v(2330.83, -3234.97) * mm});
            skLineSegment(sketch, "E157.right", {"start": v(2342.42, -3244.57) * mm, "end": v(2341.5, -3234.97) * mm});
            skLineSegment(sketch, "E158.top", {"start": v(2331.59, -3392.57) * mm, "end": v(2340.75, -3392.57) * mm});
            skLineSegment(sketch, "E158.left", {"start": v(2329.74, -3403.65) * mm, "end": v(2330.59, -3393.48) * mm});
            skLineSegment(sketch, "E158.right", {"start": v(2342.59, -3403.65) * mm, "end": v(2341.74, -3393.48) * mm});
            skLineSegment(sketch, "E159", {"start": v(2320.67, -3244.57) * mm, "end": v(2314.67, -3260.57) * mm});
            skLineSegment(sketch, "E160", {"start": v(2351.67, -3244.57) * mm, "end": v(2357.67, -3260.57) * mm});
            skLineSegment(sketch, "E161.trimOffspring", {"start": v(2343.59, -3404.57) * mm, "end": v(2351.67, -3404.57) * mm});
            skLineSegment(sketch, "E162", {"start": v(2314.67, -3388.57) * mm, "end": v(2320.67, -3404.57) * mm});
            skLineSegment(sketch, "E163", {"start": v(2357.67, -3388.57) * mm, "end": v(2351.67, -3404.57) * mm});
            skPoint(sketch, "E164.visualSharp", {"position": v(2330.92, -3234.07) * mm});
            skArc(sketch, "E164.filletArc", {"start": v(2331.82, -3234.07) * mm, "mid": v(2331.15, -3234.33) * mm, "end": v(2330.83, -3234.97) * mm});
            skPoint(sketch, "E165.visualSharp", {"position": v(2341.42, -3234.07) * mm});
            skArc(sketch, "E165.filletArc", {"start": v(2341.5, -3234.97) * mm, "mid": v(2341.18, -3234.33) * mm, "end": v(2340.5, -3234.07) * mm});
            skPoint(sketch, "E166.visualSharp", {"position": v(2330.67, -3392.57) * mm});
            skArc(sketch, "E166.filletArc", {"start": v(2331.59, -3392.57) * mm, "mid": v(2330.9, -3392.83) * mm, "end": v(2330.59, -3393.48) * mm});
            skPoint(sketch, "E167.visualSharp", {"position": v(2341.67, -3392.57) * mm});
            skArc(sketch, "E167.filletArc", {"start": v(2341.74, -3393.48) * mm, "mid": v(2341.42, -3392.83) * mm, "end": v(2340.75, -3392.57) * mm});
            skPoint(sketch, "E168.visualSharp", {"position": v(2329.67, -3404.57) * mm});
            skArc(sketch, "E168.filletArc", {"start": v(2328.75, -3404.57) * mm, "mid": v(2329.42, -3404.3) * mm, "end": v(2329.74, -3403.65) * mm});
            skPoint(sketch, "E169.visualSharp", {"position": v(2342.67, -3404.57) * mm});
            skArc(sketch, "E169.filletArc", {"start": v(2342.59, -3403.65) * mm, "mid": v(2342.9, -3404.3) * mm, "end": v(2343.59, -3404.57) * mm});
            skSolve(sketch);
        }
        {
            var Q0;
            Q0=makeQuery(id+"F53.imprint","IMPRINT",FACE,{"disambiguationData":[TD([[makeQuery(id+"F53.imprint","IMPRINT",EDGE,{"derivedFrom":sQuery(id+"F53.wireOp",EDGE,"E156.top")}),1.0]])]});
            var Q1;
            Q1=makeQuery(id+"F53.imprint","IMPRINT",FACE,{"disambiguationData":[TD([[makeQuery(id+"F53.imprint","IMPRINT",EDGE,{"derivedFrom":sQuery(id+"F53.wireOp",EDGE,"E157.bottom")}),1.0]])]});
            extrude(context, id + "F54", {"entities" : qUnion([Q0, Q1]), "depth" : 4980 * mm, "offsetDistance" : 25 * mm});
        }
        {
            var Q0;
            Q0=makeQuery(id+"F54.opExtrude","SWEPT_FACE",FACE,{"disambiguationData":[OSD([sQuery(id+"F53.wireOp",EDGE,"E156.right")])]});
            var sketch = newSketch(context, id + "F55", { "sketchPlane" : qUnion([Q0])});
            skLineSegment(sketch, "E170.bottom", {"start": v(-3229.57, 4880) * mm, "end": v(-3284.57, 4880) * mm});
            skLineSegment(sketch, "E170.top", {"start": v(-3229.57, 4837) * mm, "end": v(-3284.57, 4837) * mm});
            skLineSegment(sketch, "E170.left", {"start": v(-3229.57, 4880) * mm, "end": v(-3229.57, 4837) * mm});
            skLineSegment(sketch, "E170.right", {"start": v(-3284.57, 4880) * mm, "end": v(-3284.57, 4837) * mm});
            skLineSegment(sketch, "E171.bottom", {"start": v(-3364.57, 4880) * mm, "end": v(-3419.57, 4880) * mm});
            skLineSegment(sketch, "E171.top", {"start": v(-3364.57, 4837) * mm, "end": v(-3419.57, 4837) * mm});
            skLineSegment(sketch, "E171.left", {"start": v(-3364.57, 4880) * mm, "end": v(-3364.57, 4837) * mm});
            skLineSegment(sketch, "E171.right", {"start": v(-3419.57, 4880) * mm, "end": v(-3419.57, 4837) * mm});
            skLineSegment(sketch, "E172", {"start": v(-3443.86, -302.3) * mm, "end": v(-3443.86, 837.82) * mm});
            skLineSegment(sketch, "E173", {"start": v(-3443.86, 837.82) * mm, "end": v(-3175.09, -240.18) * mm});
            skLineSegment(sketch, "E174", {"start": v(-3175.09, -240.18) * mm, "end": v(-3443.86, -302.3) * mm});
            skSolve(sketch);
        }
        {
            var Q0;
            {var subQ0=sQuery(id+"F55.wireOp",EDGE,"E170.left");Q0=makeQuery(id+"F55.imprint","IMPRINT",FACE,{"disambiguationData":[TD([[makeQuery(id+"F55.imprint","IMPRINT",EDGE,{"derivedFrom":subQ0}),-1.0]])]});}
            var Q1;
            {var subQ0=sQuery(id+"F55.wireOp",EDGE,"E171.left");Q1=makeQuery(id+"F55.imprint","IMPRINT",FACE,{"disambiguationData":[TD([[makeQuery(id+"F55.imprint","IMPRINT",EDGE,{"derivedFrom":subQ0}),-1.0]])]});}
            var Q2;
            {var subQ0=sQuery(id+"F55.wireOp",EDGE,"E171.right");Q2=makeQuery(id+"F55.imprint","IMPRINT",FACE,{"disambiguationData":[TD([[makeQuery(id+"F55.imprint","IMPRINT",EDGE,{"derivedFrom":subQ0}),1.0]])]});}
            var Q3;
            {var subQ0=sQuery(id+"F55.wireOp",EDGE,"E170.right");Q3=makeQuery(id+"F55.imprint","IMPRINT",FACE,{"disambiguationData":[TD([[makeQuery(id+"F55.imprint","IMPRINT",EDGE,{"derivedFrom":subQ0}),1.0]])]});}
            var Q4;
            {var subQ1=sQuery(id+"F53.wireOp",EDGE,"E156.right");var subQ6=makeQuery(id+"F54.opExtrude","CAP_EDGE",EDGE,{"disambiguationData":[OSD([subQ1])],"isStart":true});Q4=makeQuery(id+"F55.imprint","IMPRINT",FACE,{"disambiguationData":[TD([[makeQuery(id+"F55.imprint","IMPRINT",EDGE,{"derivedFrom":subQ6}),-1.0]])]});}
            var Q5;
            {var subQ5=sQuery(id+"F55.wireOp",EDGE,"E172");Q5=makeQuery(id+"F55.imprint","IMPRINT",FACE,{"disambiguationData":[TD([[makeQuery(id+"F55.imprint","IMPRINT",EDGE,{"derivedFrom":subQ5}),-1.0]])]});}
            extrude(context, id + "F56", {"entities" : qUnion([Q0, Q1, Q2, Q3, Q4, Q5]), "operationType" : NewBodyOperationType.REMOVE, "oppositeDirection" : true, "depth" : 55 * mm, "offsetDistance" : 25 * mm});
        }
        {
            var Q0;
            {var subQ8=sQuery(id+"F34.wireOp",EDGE,"E43.0");Q0=makeQuery(id+"F34.imprint","IMPRINT",FACE,{"disambiguationData":[TD([[makeQuery(id+"F34.imprint","IMPRINT",EDGE,{"derivedFrom":subQ8}),1.0]])]});}
            var sketch = newSketch(context, id + "F57", { "sketchPlane" : qUnion([Q0])});
            skLineSegment(sketch, "E175.bottom", {"start": v(2445.65, -3221.33) * mm, "end": v(2476.65, -3221.33) * mm});
            skLineSegment(sketch, "E175.top", {"start": v(2445.65, -3381.33) * mm, "end": v(2453.73, -3381.33) * mm});
            skLineSegment(sketch, "E175.left", {"start": v(2439.65, -3237.33) * mm, "end": v(2439.65, -3365.33) * mm});
            skLineSegment(sketch, "E175.right", {"start": v(2482.65, -3237.33) * mm, "end": v(2482.65, -3365.33) * mm});
            skLineSegment(sketch, "E176.bottom", {"start": v(2454.9, -3221.33) * mm, "end": v(2467.4, -3221.33) * mm});
            skLineSegment(sketch, "E176.top", {"start": v(2456.8, -3210.83) * mm, "end": v(2465.49, -3210.83) * mm});
            skLineSegment(sketch, "E176.left", {"start": v(2454.9, -3221.33) * mm, "end": v(2455.81, -3211.74) * mm});
            skLineSegment(sketch, "E176.right", {"start": v(2467.4, -3221.33) * mm, "end": v(2466.48, -3211.74) * mm});
            skLineSegment(sketch, "E177.top", {"start": v(2456.57, -3369.33) * mm, "end": v(2465.73, -3369.33) * mm});
            skLineSegment(sketch, "E177.left", {"start": v(2454.73, -3380.42) * mm, "end": v(2455.57, -3370.25) * mm});
            skLineSegment(sketch, "E177.right", {"start": v(2467.57, -3380.42) * mm, "end": v(2466.73, -3370.25) * mm});
            skLineSegment(sketch, "E178", {"start": v(2445.65, -3221.33) * mm, "end": v(2439.65, -3237.33) * mm});
            skLineSegment(sketch, "E179", {"start": v(2476.65, -3221.33) * mm, "end": v(2482.65, -3237.33) * mm});
            skLineSegment(sketch, "E180.trimOffspring", {"start": v(2468.57, -3381.33) * mm, "end": v(2476.65, -3381.33) * mm});
            skLineSegment(sketch, "E181", {"start": v(2439.65, -3365.33) * mm, "end": v(2445.65, -3381.33) * mm});
            skLineSegment(sketch, "E182", {"start": v(2482.65, -3365.33) * mm, "end": v(2476.65, -3381.33) * mm});
            skPoint(sketch, "E183.visualSharp", {"position": v(2455.9, -3210.83) * mm});
            skArc(sketch, "E183.filletArc", {"start": v(2456.8, -3210.83) * mm, "mid": v(2456.14, -3211.1) * mm, "end": v(2455.81, -3211.74) * mm});
            skPoint(sketch, "E184.visualSharp", {"position": v(2466.4, -3210.83) * mm});
            skArc(sketch, "E184.filletArc", {"start": v(2466.48, -3211.74) * mm, "mid": v(2466.16, -3211.1) * mm, "end": v(2465.49, -3210.83) * mm});
            skPoint(sketch, "E185.visualSharp", {"position": v(2455.65, -3369.33) * mm});
            skArc(sketch, "E185.filletArc", {"start": v(2456.57, -3369.33) * mm, "mid": v(2455.9, -3369.6) * mm, "end": v(2455.57, -3370.25) * mm});
            skPoint(sketch, "E186.visualSharp", {"position": v(2466.65, -3369.33) * mm});
            skArc(sketch, "E186.filletArc", {"start": v(2466.73, -3370.25) * mm, "mid": v(2466.4, -3369.6) * mm, "end": v(2465.73, -3369.33) * mm});
            skPoint(sketch, "E187.visualSharp", {"position": v(2454.65, -3381.33) * mm});
            skArc(sketch, "E187.filletArc", {"start": v(2453.73, -3381.33) * mm, "mid": v(2454.4, -3381.07) * mm, "end": v(2454.73, -3380.42) * mm});
            skPoint(sketch, "E188.visualSharp", {"position": v(2467.65, -3381.33) * mm});
            skArc(sketch, "E188.filletArc", {"start": v(2467.57, -3380.42) * mm, "mid": v(2467.9, -3381.07) * mm, "end": v(2468.57, -3381.33) * mm});
            skSolve(sketch);
        }
        {
            var Q0;
            Q0=makeQuery(id+"F57.imprint","IMPRINT",FACE,{"disambiguationData":[TD([[makeQuery(id+"F57.imprint","IMPRINT",EDGE,{"derivedFrom":sQuery(id+"F57.wireOp",EDGE,"E175.top")}),1.0]])]});
            var Q1;
            Q1=makeQuery(id+"F57.imprint","IMPRINT",FACE,{"disambiguationData":[TD([[makeQuery(id+"F57.imprint","IMPRINT",EDGE,{"derivedFrom":sQuery(id+"F57.wireOp",EDGE,"E176.bottom")}),1.0]])]});
            extrude(context, id + "F58", {"entities" : qUnion([Q0, Q1]), "depth" : 5493 * mm, "offsetDistance" : 25 * mm});
        }
        {
            var Q0;
            Q0=makeQuery(id+"F58.opExtrude","SWEPT_FACE",FACE,{"disambiguationData":[OSD([sQuery(id+"F57.wireOp",EDGE,"E175.right")])]});
            var sketch = newSketch(context, id + "F59", { "sketchPlane" : qUnion([Q0])});
            skLineSegment(sketch, "E189.bottom", {"start": v(-3206.33, 5393) * mm, "end": v(-3261.33, 5393) * mm});
            skLineSegment(sketch, "E189.top", {"start": v(-3206.33, 5350) * mm, "end": v(-3261.33, 5350) * mm});
            skLineSegment(sketch, "E189.left", {"start": v(-3206.33, 5393) * mm, "end": v(-3206.33, 5350) * mm});
            skLineSegment(sketch, "E189.right", {"start": v(-3261.33, 5393) * mm, "end": v(-3261.33, 5350) * mm});
            skLineSegment(sketch, "E190.bottom", {"start": v(-3341.33, 5393) * mm, "end": v(-3396.33, 5393) * mm});
            skLineSegment(sketch, "E190.top", {"start": v(-3341.33, 5350) * mm, "end": v(-3396.33, 5350) * mm});
            skLineSegment(sketch, "E190.left", {"start": v(-3341.33, 5393) * mm, "end": v(-3341.33, 5350) * mm});
            skLineSegment(sketch, "E190.right", {"start": v(-3396.33, 5393) * mm, "end": v(-3396.33, 5350) * mm});
            skLineSegment(sketch, "E191", {"start": v(-3523.93, -321.6) * mm, "end": v(-3523.93, 1002.33) * mm});
            skLineSegment(sketch, "E192", {"start": v(-3523.93, 1002.33) * mm, "end": v(-3127.82, -269.45) * mm});
            skLineSegment(sketch, "E193", {"start": v(-3127.82, -269.45) * mm, "end": v(-3523.93, -321.6) * mm});
            skSolve(sketch);
        }
        {
            var Q0;
            {var subQ1=sQuery(id+"F57.wireOp",EDGE,"E175.right");var subQ6=makeQuery(id+"F58.opExtrude","CAP_EDGE",EDGE,{"disambiguationData":[OSD([subQ1])],"isStart":true});Q0=makeQuery(id+"F59.imprint","IMPRINT",FACE,{"disambiguationData":[TD([[makeQuery(id+"F59.imprint","IMPRINT",EDGE,{"derivedFrom":subQ6}),-1.0]])]});}
            var Q1;
            {var subQ5=sQuery(id+"F59.wireOp",EDGE,"E191");Q1=makeQuery(id+"F59.imprint","IMPRINT",FACE,{"disambiguationData":[TD([[makeQuery(id+"F59.imprint","IMPRINT",EDGE,{"derivedFrom":subQ5}),-1.0]])]});}
            var Q2;
            {var subQ0=sQuery(id+"F59.wireOp",EDGE,"E189.right");Q2=makeQuery(id+"F59.imprint","IMPRINT",FACE,{"disambiguationData":[TD([[makeQuery(id+"F59.imprint","IMPRINT",EDGE,{"derivedFrom":subQ0}),1.0]])]});}
            var Q3;
            {var subQ0=sQuery(id+"F59.wireOp",EDGE,"E189.left");Q3=makeQuery(id+"F59.imprint","IMPRINT",FACE,{"disambiguationData":[TD([[makeQuery(id+"F59.imprint","IMPRINT",EDGE,{"derivedFrom":subQ0}),-1.0]])]});}
            var Q4;
            {var subQ0=sQuery(id+"F59.wireOp",EDGE,"E190.right");Q4=makeQuery(id+"F59.imprint","IMPRINT",FACE,{"disambiguationData":[TD([[makeQuery(id+"F59.imprint","IMPRINT",EDGE,{"derivedFrom":subQ0}),1.0]])]});}
            var Q5;
            {var subQ0=sQuery(id+"F59.wireOp",EDGE,"E190.left");Q5=makeQuery(id+"F59.imprint","IMPRINT",FACE,{"disambiguationData":[TD([[makeQuery(id+"F59.imprint","IMPRINT",EDGE,{"derivedFrom":subQ0}),-1.0]])]});}
            extrude(context, id + "F60", {"entities" : qUnion([Q0, Q1, Q2, Q3, Q4, Q5]), "operationType" : NewBodyOperationType.REMOVE, "oppositeDirection" : true, "depth" : 55 * mm, "offsetDistance" : 25 * mm});
        }
        {
            var Q0;
            {var subQ8=sQuery(id+"F34.wireOp",EDGE,"E43.0");Q0=makeQuery(id+"F34.imprint","IMPRINT",FACE,{"disambiguationData":[TD([[makeQuery(id+"F34.imprint","IMPRINT",EDGE,{"derivedFrom":subQ8}),1.0]])]});}
            var sketch = newSketch(context, id + "F61", { "sketchPlane" : qUnion([Q0])});
            skLineSegment(sketch, "E194.bottom", {"start": v(2532.61, -3282.05) * mm, "end": v(2563.61, -3282.05) * mm});
            skLineSegment(sketch, "E194.top", {"start": v(2532.61, -3442.05) * mm, "end": v(2540.7, -3442.05) * mm});
            skLineSegment(sketch, "E194.left", {"start": v(2526.61, -3298.05) * mm, "end": v(2526.61, -3426.05) * mm});
            skLineSegment(sketch, "E194.right", {"start": v(2569.61, -3298.05) * mm, "end": v(2569.61, -3426.05) * mm});
            skLineSegment(sketch, "E195.bottom", {"start": v(2541.86, -3282.05) * mm, "end": v(2554.36, -3282.05) * mm});
            skLineSegment(sketch, "E195.top", {"start": v(2543.77, -3271.55) * mm, "end": v(2552.46, -3271.55) * mm});
            skLineSegment(sketch, "E195.left", {"start": v(2541.86, -3282.05) * mm, "end": v(2542.78, -3272.45) * mm});
            skLineSegment(sketch, "E195.right", {"start": v(2554.36, -3282.05) * mm, "end": v(2553.45, -3272.45) * mm});
            skLineSegment(sketch, "E196.top", {"start": v(2543.53, -3430.05) * mm, "end": v(2552.7, -3430.05) * mm});
            skLineSegment(sketch, "E196.left", {"start": v(2541.7, -3441.13) * mm, "end": v(2542.54, -3430.96) * mm});
            skLineSegment(sketch, "E196.right", {"start": v(2554.54, -3441.13) * mm, "end": v(2553.7, -3430.96) * mm});
            skLineSegment(sketch, "E197", {"start": v(2532.61, -3282.05) * mm, "end": v(2526.61, -3298.05) * mm});
            skLineSegment(sketch, "E198", {"start": v(2563.61, -3282.05) * mm, "end": v(2569.61, -3298.05) * mm});
            skLineSegment(sketch, "E199.trimOffspring", {"start": v(2555.53, -3442.05) * mm, "end": v(2563.61, -3442.05) * mm});
            skLineSegment(sketch, "E200", {"start": v(2526.61, -3426.05) * mm, "end": v(2532.61, -3442.05) * mm});
            skLineSegment(sketch, "E201", {"start": v(2569.61, -3426.05) * mm, "end": v(2563.61, -3442.05) * mm});
            skPoint(sketch, "E202.visualSharp", {"position": v(2542.86, -3271.55) * mm});
            skArc(sketch, "E202.filletArc", {"start": v(2543.77, -3271.55) * mm, "mid": v(2543.1, -3271.8) * mm, "end": v(2542.78, -3272.45) * mm});
            skPoint(sketch, "E203.visualSharp", {"position": v(2553.36, -3271.55) * mm});
            skArc(sketch, "E203.filletArc", {"start": v(2553.45, -3272.45) * mm, "mid": v(2553.13, -3271.8) * mm, "end": v(2552.46, -3271.55) * mm});
            skPoint(sketch, "E204.visualSharp", {"position": v(2542.61, -3430.05) * mm});
            skArc(sketch, "E204.filletArc", {"start": v(2543.53, -3430.05) * mm, "mid": v(2542.86, -3430.31) * mm, "end": v(2542.54, -3430.96) * mm});
            skPoint(sketch, "E205.visualSharp", {"position": v(2553.61, -3430.05) * mm});
            skArc(sketch, "E205.filletArc", {"start": v(2553.7, -3430.96) * mm, "mid": v(2553.37, -3430.31) * mm, "end": v(2552.7, -3430.05) * mm});
            skPoint(sketch, "E206.visualSharp", {"position": v(2541.61, -3442.05) * mm});
            skArc(sketch, "E206.filletArc", {"start": v(2540.7, -3442.05) * mm, "mid": v(2541.37, -3441.78) * mm, "end": v(2541.7, -3441.13) * mm});
            skPoint(sketch, "E207.visualSharp", {"position": v(2554.61, -3442.05) * mm});
            skArc(sketch, "E207.filletArc", {"start": v(2554.54, -3441.13) * mm, "mid": v(2554.86, -3441.78) * mm, "end": v(2555.53, -3442.05) * mm});
            skSolve(sketch);
        }
        {
            var Q0;
            Q0=makeQuery(id+"F61.imprint","IMPRINT",FACE,{"disambiguationData":[TD([[makeQuery(id+"F61.imprint","IMPRINT",EDGE,{"derivedFrom":sQuery(id+"F61.wireOp",EDGE,"E194.top")}),1.0]])]});
            var Q1;
            Q1=makeQuery(id+"F61.imprint","IMPRINT",FACE,{"disambiguationData":[TD([[makeQuery(id+"F61.imprint","IMPRINT",EDGE,{"derivedFrom":sQuery(id+"F61.wireOp",EDGE,"E195.bottom")}),1.0]])]});
            extrude(context, id + "F62", {"entities" : qUnion([Q0, Q1]), "depth" : 2500 * mm, "offsetDistance" : 25 * mm});
        }
        {
            var Q0;
            Q0=makeQuery(id+"F62.opExtrude","SWEPT_FACE",FACE,{"disambiguationData":[OSD([sQuery(id+"F61.wireOp",EDGE,"E194.right")])]});
            var sketch = newSketch(context, id + "F63", { "sketchPlane" : qUnion([Q0])});
            skLineSegment(sketch, "E208.bottom", {"start": v(-3267.05, 2400) * mm, "end": v(-3322.05, 2400) * mm});
            skLineSegment(sketch, "E208.top", {"start": v(-3267.05, 2357) * mm, "end": v(-3322.05, 2357) * mm});
            skLineSegment(sketch, "E208.left", {"start": v(-3267.05, 2400) * mm, "end": v(-3267.05, 2357) * mm});
            skLineSegment(sketch, "E208.right", {"start": v(-3322.05, 2400) * mm, "end": v(-3322.05, 2357) * mm});
            skLineSegment(sketch, "E209.bottom", {"start": v(-3402.05, 2400) * mm, "end": v(-3457.05, 2400) * mm});
            skLineSegment(sketch, "E209.top", {"start": v(-3402.05, 2357) * mm, "end": v(-3457.05, 2357) * mm});
            skLineSegment(sketch, "E209.left", {"start": v(-3402.05, 2400) * mm, "end": v(-3402.05, 2357) * mm});
            skLineSegment(sketch, "E209.right", {"start": v(-3457.05, 2400) * mm, "end": v(-3457.05, 2357) * mm});
            skSolve(sketch);
        }
        {
            var Q0;
            {var subQ0=sQuery(id+"F63.wireOp",EDGE,"E208.left");Q0=makeQuery(id+"F63.imprint","IMPRINT",FACE,{"disambiguationData":[TD([[makeQuery(id+"F63.imprint","IMPRINT",EDGE,{"derivedFrom":subQ0}),-1.0]])]});}
            var Q1;
            {var subQ0=sQuery(id+"F63.wireOp",EDGE,"E208.right");Q1=makeQuery(id+"F63.imprint","IMPRINT",FACE,{"disambiguationData":[TD([[makeQuery(id+"F63.imprint","IMPRINT",EDGE,{"derivedFrom":subQ0}),1.0]])]});}
            var Q2;
            {var subQ0=sQuery(id+"F63.wireOp",EDGE,"E209.left");Q2=makeQuery(id+"F63.imprint","IMPRINT",FACE,{"disambiguationData":[TD([[makeQuery(id+"F63.imprint","IMPRINT",EDGE,{"derivedFrom":subQ0}),-1.0]])]});}
            var Q3;
            {var subQ0=sQuery(id+"F63.wireOp",EDGE,"E209.right");Q3=makeQuery(id+"F63.imprint","IMPRINT",FACE,{"disambiguationData":[TD([[makeQuery(id+"F63.imprint","IMPRINT",EDGE,{"derivedFrom":subQ0}),1.0]])]});}
            extrude(context, id + "F64", {"entities" : qUnion([Q0, Q1, Q2, Q3]), "operationType" : NewBodyOperationType.REMOVE, "oppositeDirection" : true, "depth" : 55 * mm, "offsetDistance" : 25 * mm});
        }
        {
            var Q0;
            {var subQ8=sQuery(id+"F34.wireOp",EDGE,"E43.0");Q0=makeQuery(id+"F34.imprint","IMPRINT",FACE,{"disambiguationData":[TD([[makeQuery(id+"F34.imprint","IMPRINT",EDGE,{"derivedFrom":subQ8}),1.0]])]});}
            var sketch = newSketch(context, id + "F65", { "sketchPlane" : qUnion([Q0])});
            skLineSegment(sketch, "E210.bottom", {"start": v(2652.65, -3260.7) * mm, "end": v(2683.65, -3260.7) * mm});
            skLineSegment(sketch, "E210.top", {"start": v(2652.65, -3420.7) * mm, "end": v(2660.73, -3420.7) * mm});
            skLineSegment(sketch, "E210.left", {"start": v(2646.65, -3276.7) * mm, "end": v(2646.65, -3404.7) * mm});
            skLineSegment(sketch, "E210.right", {"start": v(2689.65, -3276.7) * mm, "end": v(2689.65, -3404.7) * mm});
            skLineSegment(sketch, "E211.bottom", {"start": v(2661.9, -3260.7) * mm, "end": v(2674.4, -3260.7) * mm});
            skLineSegment(sketch, "E211.top", {"start": v(2663.81, -3250.2) * mm, "end": v(2672.5, -3250.2) * mm});
            skLineSegment(sketch, "E211.left", {"start": v(2661.9, -3260.7) * mm, "end": v(2662.82, -3251.1) * mm});
            skLineSegment(sketch, "E211.right", {"start": v(2674.4, -3260.7) * mm, "end": v(2673.49, -3251.1) * mm});
            skLineSegment(sketch, "E212.top", {"start": v(2663.57, -3408.7) * mm, "end": v(2672.73, -3408.7) * mm});
            skLineSegment(sketch, "E212.left", {"start": v(2661.73, -3419.78) * mm, "end": v(2662.57, -3409.6) * mm});
            skLineSegment(sketch, "E212.right", {"start": v(2674.57, -3419.78) * mm, "end": v(2673.73, -3409.6) * mm});
            skLineSegment(sketch, "E213", {"start": v(2652.65, -3260.7) * mm, "end": v(2646.65, -3276.7) * mm});
            skLineSegment(sketch, "E214", {"start": v(2683.65, -3260.7) * mm, "end": v(2689.65, -3276.7) * mm});
            skLineSegment(sketch, "E215.trimOffspring", {"start": v(2675.57, -3420.7) * mm, "end": v(2683.65, -3420.7) * mm});
            skLineSegment(sketch, "E216", {"start": v(2646.65, -3404.7) * mm, "end": v(2652.65, -3420.7) * mm});
            skLineSegment(sketch, "E217", {"start": v(2689.65, -3404.7) * mm, "end": v(2683.65, -3420.7) * mm});
            skPoint(sketch, "E218.visualSharp", {"position": v(2662.9, -3250.2) * mm});
            skArc(sketch, "E218.filletArc", {"start": v(2663.81, -3250.2) * mm, "mid": v(2663.14, -3250.45) * mm, "end": v(2662.82, -3251.1) * mm});
            skPoint(sketch, "E219.visualSharp", {"position": v(2673.4, -3250.2) * mm});
            skArc(sketch, "E219.filletArc", {"start": v(2673.49, -3251.1) * mm, "mid": v(2673.16, -3250.45) * mm, "end": v(2672.5, -3250.2) * mm});
            skPoint(sketch, "E220.visualSharp", {"position": v(2662.65, -3408.7) * mm});
            skArc(sketch, "E220.filletArc", {"start": v(2663.57, -3408.7) * mm, "mid": v(2662.9, -3408.96) * mm, "end": v(2662.57, -3409.6) * mm});
            skPoint(sketch, "E221.visualSharp", {"position": v(2673.65, -3408.7) * mm});
            skArc(sketch, "E221.filletArc", {"start": v(2673.73, -3409.6) * mm, "mid": v(2673.4, -3408.96) * mm, "end": v(2672.73, -3408.7) * mm});
            skPoint(sketch, "E222.visualSharp", {"position": v(2661.65, -3420.7) * mm});
            skArc(sketch, "E222.filletArc", {"start": v(2660.73, -3420.7) * mm, "mid": v(2661.4, -3420.43) * mm, "end": v(2661.73, -3419.78) * mm});
            skPoint(sketch, "E223.visualSharp", {"position": v(2674.65, -3420.7) * mm});
            skArc(sketch, "E223.filletArc", {"start": v(2674.57, -3419.78) * mm, "mid": v(2674.9, -3420.43) * mm, "end": v(2675.57, -3420.7) * mm});
            skSolve(sketch);
        }
        {
            var Q0;
            Q0=makeQuery(id+"F65.imprint","IMPRINT",FACE,{"disambiguationData":[TD([[makeQuery(id+"F65.imprint","IMPRINT",EDGE,{"derivedFrom":sQuery(id+"F65.wireOp",EDGE,"E210.top")}),1.0]])]});
            var Q1;
            Q1=makeQuery(id+"F65.imprint","IMPRINT",FACE,{"disambiguationData":[TD([[makeQuery(id+"F65.imprint","IMPRINT",EDGE,{"derivedFrom":sQuery(id+"F65.wireOp",EDGE,"E211.bottom")}),1.0]])]});
            extrude(context, id + "F66", {"entities" : qUnion([Q0, Q1]), "depth" : 2271 * mm, "offsetDistance" : 25 * mm});
        }
        {
            var Q0;
            Q0=makeQuery(id+"F66.opExtrude","SWEPT_FACE",FACE,{"disambiguationData":[OSD([sQuery(id+"F65.wireOp",EDGE,"E210.right")])]});
            var sketch = newSketch(context, id + "F67", { "sketchPlane" : qUnion([Q0])});
            skLineSegment(sketch, "E224", {"start": v(-3474.03, 2442.25) * mm, "end": v(-3184.02, 1511.14) * mm});
            skLineSegment(sketch, "E225", {"start": v(-3184.02, 1511.14) * mm, "end": v(-3184.02, 2457.01) * mm});
            skLineSegment(sketch, "E226", {"start": v(-3184.02, 2457.01) * mm, "end": v(-3474.03, 2442.25) * mm});
            skSolve(sketch);
        }
        {
            var Q0;
            {var subQ1=sQuery(id+"F67.wireOp",EDGE,"E225");Q0=makeQuery(id+"F67.imprint","IMPRINT",FACE,{"disambiguationData":[TD([[makeQuery(id+"F67.imprint","IMPRINT",EDGE,{"derivedFrom":subQ1}),1.0]])]});}
            var Q1;
            {var subQ1=sQuery(id+"F65.wireOp",EDGE,"E210.right");var subQ6=makeQuery(id+"F66.opExtrude","CAP_EDGE",EDGE,{"disambiguationData":[OSD([subQ1])],"isStart":false});Q1=makeQuery(id+"F67.imprint","IMPRINT",FACE,{"disambiguationData":[TD([[makeQuery(id+"F67.imprint","IMPRINT",EDGE,{"derivedFrom":subQ6}),1.0]])]});}
            extrude(context, id + "F68", {"entities" : qUnion([Q0, Q1]), "operationType" : NewBodyOperationType.REMOVE, "oppositeDirection" : true, "depth" : 55 * mm, "offsetDistance" : 25 * mm});
        }
        {
            var Q0;
            {var subQ8=sQuery(id+"F34.wireOp",EDGE,"E43.0");Q0=makeQuery(id+"F34.imprint","IMPRINT",FACE,{"disambiguationData":[TD([[makeQuery(id+"F34.imprint","IMPRINT",EDGE,{"derivedFrom":subQ8}),1.0]])]});}
            var sketch = newSketch(context, id + "F69", { "sketchPlane" : qUnion([Q0])});
            skLineSegment(sketch, "E227.bottom", {"start": v(2812.66, -3228.85) * mm, "end": v(2843.66, -3228.85) * mm});
            skLineSegment(sketch, "E227.top", {"start": v(2812.66, -3388.85) * mm, "end": v(2820.74, -3388.85) * mm});
            skLineSegment(sketch, "E227.left", {"start": v(2806.66, -3244.85) * mm, "end": v(2806.66, -3372.85) * mm});
            skLineSegment(sketch, "E227.right", {"start": v(2849.66, -3244.85) * mm, "end": v(2849.66, -3372.85) * mm});
            skLineSegment(sketch, "E228.bottom", {"start": v(2821.9, -3228.85) * mm, "end": v(2834.4, -3228.85) * mm});
            skLineSegment(sketch, "E228.top", {"start": v(2823.82, -3218.35) * mm, "end": v(2832.5, -3218.35) * mm});
            skLineSegment(sketch, "E228.left", {"start": v(2821.9, -3228.85) * mm, "end": v(2822.82, -3219.26) * mm});
            skLineSegment(sketch, "E228.right", {"start": v(2834.4, -3228.85) * mm, "end": v(2833.5, -3219.26) * mm});
            skLineSegment(sketch, "E229.top", {"start": v(2823.58, -3376.85) * mm, "end": v(2832.74, -3376.85) * mm});
            skLineSegment(sketch, "E229.left", {"start": v(2821.74, -3387.94) * mm, "end": v(2822.58, -3377.77) * mm});
            skLineSegment(sketch, "E229.right", {"start": v(2834.58, -3387.94) * mm, "end": v(2833.74, -3377.77) * mm});
            skLineSegment(sketch, "E230", {"start": v(2812.66, -3228.85) * mm, "end": v(2806.66, -3244.85) * mm});
            skLineSegment(sketch, "E231", {"start": v(2843.66, -3228.85) * mm, "end": v(2849.66, -3244.85) * mm});
            skLineSegment(sketch, "E232.trimOffspring", {"start": v(2835.58, -3388.85) * mm, "end": v(2843.66, -3388.85) * mm});
            skLineSegment(sketch, "E233", {"start": v(2806.66, -3372.85) * mm, "end": v(2812.66, -3388.85) * mm});
            skLineSegment(sketch, "E234", {"start": v(2849.66, -3372.85) * mm, "end": v(2843.66, -3388.85) * mm});
            skPoint(sketch, "E235.visualSharp", {"position": v(2822.9, -3218.35) * mm});
            skArc(sketch, "E235.filletArc", {"start": v(2823.82, -3218.35) * mm, "mid": v(2823.15, -3218.61) * mm, "end": v(2822.82, -3219.26) * mm});
            skPoint(sketch, "E236.visualSharp", {"position": v(2833.4, -3218.35) * mm});
            skArc(sketch, "E236.filletArc", {"start": v(2833.5, -3219.26) * mm, "mid": v(2833.17, -3218.61) * mm, "end": v(2832.5, -3218.35) * mm});
            skPoint(sketch, "E237.visualSharp", {"position": v(2822.66, -3376.85) * mm});
            skArc(sketch, "E237.filletArc", {"start": v(2823.58, -3376.85) * mm, "mid": v(2822.9, -3377.12) * mm, "end": v(2822.58, -3377.77) * mm});
            skPoint(sketch, "E238.visualSharp", {"position": v(2833.66, -3376.85) * mm});
            skArc(sketch, "E238.filletArc", {"start": v(2833.74, -3377.77) * mm, "mid": v(2833.42, -3377.12) * mm, "end": v(2832.74, -3376.85) * mm});
            skPoint(sketch, "E239.visualSharp", {"position": v(2821.66, -3388.85) * mm});
            skArc(sketch, "E239.filletArc", {"start": v(2820.74, -3388.85) * mm, "mid": v(2821.42, -3388.59) * mm, "end": v(2821.74, -3387.94) * mm});
            skPoint(sketch, "E240.visualSharp", {"position": v(2834.66, -3388.85) * mm});
            skArc(sketch, "E240.filletArc", {"start": v(2834.58, -3387.94) * mm, "mid": v(2834.9, -3388.59) * mm, "end": v(2835.58, -3388.85) * mm});
            skSolve(sketch);
        }
        {
            var Q0;
            Q0=makeQuery(id+"F69.imprint","IMPRINT",FACE,{"disambiguationData":[TD([[makeQuery(id+"F69.imprint","IMPRINT",EDGE,{"derivedFrom":sQuery(id+"F69.wireOp",EDGE,"E227.top")}),1.0]])]});
            var Q1;
            Q1=makeQuery(id+"F69.imprint","IMPRINT",FACE,{"disambiguationData":[TD([[makeQuery(id+"F69.imprint","IMPRINT",EDGE,{"derivedFrom":sQuery(id+"F69.wireOp",EDGE,"E228.bottom")}),1.0]])]});
            extrude(context, id + "F70", {"entities" : qUnion([Q0, Q1]), "depth" : 4116 * mm, "offsetDistance" : 25 * mm});
        }
        {
            var Q0;
            Q0=makeQuery(id+"F70.opExtrude","SWEPT_FACE",FACE,{"disambiguationData":[OSD([sQuery(id+"F69.wireOp",EDGE,"E227.right")])]});
            var sketch = newSketch(context, id + "F71", { "sketchPlane" : qUnion([Q0])});
            skLineSegment(sketch, "E241", {"start": v(-3452, 4318.76) * mm, "end": v(-3100.82, 3191.25) * mm});
            skLineSegment(sketch, "E242", {"start": v(-3100.82, 3191.25) * mm, "end": v(-3100.82, 4335.49) * mm});
            skLineSegment(sketch, "E243", {"start": v(-3100.82, 4335.49) * mm, "end": v(-3452, 4318.76) * mm});
            skLineSegment(sketch, "E244", {"start": v(-3448.27, -190.77) * mm, "end": v(-3150.64, 764.82) * mm});
            skLineSegment(sketch, "E245", {"start": v(-3150.64, 764.82) * mm, "end": v(-3150.64, -229.42) * mm});
            skLineSegment(sketch, "E246", {"start": v(-3150.64, -229.42) * mm, "end": v(-3448.27, -190.77) * mm});
            skSolve(sketch);
        }
        {
            var Q0;
            {var subQ1=sQuery(id+"F71.wireOp",EDGE,"E242");Q0=makeQuery(id+"F71.imprint","IMPRINT",FACE,{"disambiguationData":[TD([[makeQuery(id+"F71.imprint","IMPRINT",EDGE,{"derivedFrom":subQ1}),1.0]])]});}
            var Q1;
            {var subQ1=sQuery(id+"F69.wireOp",EDGE,"E227.right");var subQ6=makeQuery(id+"F70.opExtrude","CAP_EDGE",EDGE,{"disambiguationData":[OSD([subQ1])],"isStart":false});Q1=makeQuery(id+"F71.imprint","IMPRINT",FACE,{"disambiguationData":[TD([[makeQuery(id+"F71.imprint","IMPRINT",EDGE,{"derivedFrom":subQ6}),1.0]])]});}
            var Q2;
            {var subQ1=sQuery(id+"F71.wireOp",EDGE,"E245");Q2=makeQuery(id+"F71.imprint","IMPRINT",FACE,{"disambiguationData":[TD([[makeQuery(id+"F71.imprint","IMPRINT",EDGE,{"derivedFrom":subQ1}),-1.0]])]});}
            var Q3;
            {var subQ1=sQuery(id+"F69.wireOp",EDGE,"E227.right");var subQ6=makeQuery(id+"F70.opExtrude","CAP_EDGE",EDGE,{"disambiguationData":[OSD([subQ1])],"isStart":true});Q3=makeQuery(id+"F71.imprint","IMPRINT",FACE,{"disambiguationData":[TD([[makeQuery(id+"F71.imprint","IMPRINT",EDGE,{"derivedFrom":subQ6}),-1.0]])]});}
            extrude(context, id + "F72", {"entities" : qUnion([Q0, Q1, Q2, Q3]), "operationType" : NewBodyOperationType.REMOVE, "oppositeDirection" : true, "depth" : 55 * mm, "offsetDistance" : 25 * mm});
        }
        {
            var Q0;
            {var subQ8=sQuery(id+"F34.wireOp",EDGE,"E43.0");Q0=makeQuery(id+"F34.imprint","IMPRINT",FACE,{"disambiguationData":[TD([[makeQuery(id+"F34.imprint","IMPRINT",EDGE,{"derivedFrom":subQ8}),1.0]])]});}
            var sketch = newSketch(context, id + "F73", { "sketchPlane" : qUnion([Q0])});
            skLineSegment(sketch, "E247.bottom", {"start": v(2956.05, -3266.47) * mm, "end": v(2987.05, -3266.47) * mm});
            skLineSegment(sketch, "E247.top", {"start": v(2956.05, -3426.47) * mm, "end": v(2964.13, -3426.47) * mm});
            skLineSegment(sketch, "E247.left", {"start": v(2950.05, -3282.47) * mm, "end": v(2950.05, -3410.47) * mm});
            skLineSegment(sketch, "E247.right", {"start": v(2993.05, -3282.47) * mm, "end": v(2993.05, -3410.47) * mm});
            skLineSegment(sketch, "E248.bottom", {"start": v(2965.3, -3266.47) * mm, "end": v(2977.8, -3266.47) * mm});
            skLineSegment(sketch, "E248.top", {"start": v(2967.21, -3255.97) * mm, "end": v(2975.9, -3255.97) * mm});
            skLineSegment(sketch, "E248.left", {"start": v(2965.3, -3266.47) * mm, "end": v(2966.22, -3256.88) * mm});
            skLineSegment(sketch, "E248.right", {"start": v(2977.8, -3266.47) * mm, "end": v(2976.9, -3256.88) * mm});
            skLineSegment(sketch, "E249.top", {"start": v(2966.97, -3414.47) * mm, "end": v(2976.13, -3414.47) * mm});
            skLineSegment(sketch, "E249.left", {"start": v(2965.13, -3425.55) * mm, "end": v(2965.98, -3415.39) * mm});
            skLineSegment(sketch, "E249.right", {"start": v(2977.98, -3425.55) * mm, "end": v(2977.13, -3415.39) * mm});
            skLineSegment(sketch, "E250", {"start": v(2956.05, -3266.47) * mm, "end": v(2950.05, -3282.47) * mm});
            skLineSegment(sketch, "E251", {"start": v(2987.05, -3266.47) * mm, "end": v(2993.05, -3282.47) * mm});
            skLineSegment(sketch, "E252.trimOffspring", {"start": v(2978.97, -3426.47) * mm, "end": v(2987.05, -3426.47) * mm});
            skLineSegment(sketch, "E253", {"start": v(2950.05, -3410.47) * mm, "end": v(2956.05, -3426.47) * mm});
            skLineSegment(sketch, "E254", {"start": v(2993.05, -3410.47) * mm, "end": v(2987.05, -3426.47) * mm});
            skPoint(sketch, "E255.visualSharp", {"position": v(2966.3, -3255.97) * mm});
            skArc(sketch, "E255.filletArc", {"start": v(2967.21, -3255.97) * mm, "mid": v(2966.54, -3256.23) * mm, "end": v(2966.22, -3256.88) * mm});
            skPoint(sketch, "E256.visualSharp", {"position": v(2976.8, -3255.97) * mm});
            skArc(sketch, "E256.filletArc", {"start": v(2976.9, -3256.88) * mm, "mid": v(2976.57, -3256.23) * mm, "end": v(2975.9, -3255.97) * mm});
            skPoint(sketch, "E257.visualSharp", {"position": v(2966.05, -3414.47) * mm});
            skArc(sketch, "E257.filletArc", {"start": v(2966.97, -3414.47) * mm, "mid": v(2966.3, -3414.73) * mm, "end": v(2965.98, -3415.39) * mm});
            skPoint(sketch, "E258.visualSharp", {"position": v(2977.05, -3414.47) * mm});
            skArc(sketch, "E258.filletArc", {"start": v(2977.13, -3415.39) * mm, "mid": v(2976.81, -3414.73) * mm, "end": v(2976.13, -3414.47) * mm});
            skPoint(sketch, "E259.visualSharp", {"position": v(2965.05, -3426.47) * mm});
            skArc(sketch, "E259.filletArc", {"start": v(2964.13, -3426.47) * mm, "mid": v(2964.81, -3426.2) * mm, "end": v(2965.13, -3425.55) * mm});
            skPoint(sketch, "E260.visualSharp", {"position": v(2978.05, -3426.47) * mm});
            skArc(sketch, "E260.filletArc", {"start": v(2977.98, -3425.55) * mm, "mid": v(2978.3, -3426.2) * mm, "end": v(2978.97, -3426.47) * mm});
            skSolve(sketch);
        }
        {
            var Q0;
            Q0=makeQuery(id+"F73.imprint","IMPRINT",FACE,{"disambiguationData":[TD([[makeQuery(id+"F73.imprint","IMPRINT",EDGE,{"derivedFrom":sQuery(id+"F73.wireOp",EDGE,"E247.top")}),1.0]])]});
            var Q1;
            Q1=makeQuery(id+"F73.imprint","IMPRINT",FACE,{"disambiguationData":[TD([[makeQuery(id+"F73.imprint","IMPRINT",EDGE,{"derivedFrom":sQuery(id+"F73.wireOp",EDGE,"E248.bottom")}),1.0]])]});
            extrude(context, id + "F74", {"entities" : qUnion([Q0, Q1]), "depth" : 3088 * mm, "offsetDistance" : 25 * mm});
        }
        {
            var Q0;
            Q0=makeQuery(id+"F74.opExtrude","SWEPT_FACE",FACE,{"disambiguationData":[OSD([sQuery(id+"F73.wireOp",EDGE,"E247.right")])]});
            var sketch = newSketch(context, id + "F75", { "sketchPlane" : qUnion([Q0])});
            skLineSegment(sketch, "E261", {"start": v(-3485.66, 3278.04) * mm, "end": v(-3181.1, 2300.22) * mm});
            skLineSegment(sketch, "E262", {"start": v(-3181.1, 2300.22) * mm, "end": v(-3181.1, 3340.12) * mm});
            skLineSegment(sketch, "E263", {"start": v(-3181.1, 3340.12) * mm, "end": v(-3485.66, 3278.04) * mm});
            skLineSegment(sketch, "E264", {"start": v(-3476.02, -159.08) * mm, "end": v(-3213.52, 683.72) * mm});
            skLineSegment(sketch, "E265", {"start": v(-3213.52, 683.72) * mm, "end": v(-3213.52, -163.24) * mm});
            skLineSegment(sketch, "E266", {"start": v(-3213.52, -163.24) * mm, "end": v(-3476.02, -159.08) * mm});
            skSolve(sketch);
        }
        {
            var Q0;
            {var subQ1=sQuery(id+"F75.wireOp",EDGE,"E265");Q0=makeQuery(id+"F75.imprint","IMPRINT",FACE,{"disambiguationData":[TD([[makeQuery(id+"F75.imprint","IMPRINT",EDGE,{"derivedFrom":subQ1}),-1.0]])]});}
            var Q1;
            {var subQ1=sQuery(id+"F73.wireOp",EDGE,"E247.right");var subQ6=makeQuery(id+"F74.opExtrude","CAP_EDGE",EDGE,{"disambiguationData":[OSD([subQ1])],"isStart":true});Q1=makeQuery(id+"F75.imprint","IMPRINT",FACE,{"disambiguationData":[TD([[makeQuery(id+"F75.imprint","IMPRINT",EDGE,{"derivedFrom":subQ6}),-1.0]])]});}
            var Q2;
            {var subQ1=sQuery(id+"F73.wireOp",EDGE,"E247.right");var subQ6=makeQuery(id+"F74.opExtrude","CAP_EDGE",EDGE,{"disambiguationData":[OSD([subQ1])],"isStart":false});Q2=makeQuery(id+"F75.imprint","IMPRINT",FACE,{"disambiguationData":[TD([[makeQuery(id+"F75.imprint","IMPRINT",EDGE,{"derivedFrom":subQ6}),1.0]])]});}
            var Q3;
            {var subQ1=sQuery(id+"F75.wireOp",EDGE,"E262");Q3=makeQuery(id+"F75.imprint","IMPRINT",FACE,{"disambiguationData":[TD([[makeQuery(id+"F75.imprint","IMPRINT",EDGE,{"derivedFrom":subQ1}),1.0]])]});}
            extrude(context, id + "F76", {"entities" : qUnion([Q0, Q1, Q2, Q3]), "operationType" : NewBodyOperationType.REMOVE, "oppositeDirection" : true, "depth" : 55 * mm, "offsetDistance" : 25 * mm});
        }
        {
            var Q0;
            {var subQ8=sQuery(id+"F34.wireOp",EDGE,"E43.0");Q0=makeQuery(id+"F34.imprint","IMPRINT",FACE,{"disambiguationData":[TD([[makeQuery(id+"F34.imprint","IMPRINT",EDGE,{"derivedFrom":subQ8}),1.0]])]});}
            var sketch = newSketch(context, id + "F77", { "sketchPlane" : qUnion([Q0])});
            skLineSegment(sketch, "E267.bottom", {"start": v(3124.27, -3265.87) * mm, "end": v(3155.27, -3265.87) * mm});
            skLineSegment(sketch, "E267.top", {"start": v(3124.27, -3425.87) * mm, "end": v(3132.35, -3425.87) * mm});
            skLineSegment(sketch, "E267.left", {"start": v(3118.27, -3281.87) * mm, "end": v(3118.27, -3409.87) * mm});
            skLineSegment(sketch, "E267.right", {"start": v(3161.27, -3281.87) * mm, "end": v(3161.27, -3409.87) * mm});
            skLineSegment(sketch, "E268.bottom", {"start": v(3133.52, -3265.87) * mm, "end": v(3146.02, -3265.87) * mm});
            skLineSegment(sketch, "E268.top", {"start": v(3135.43, -3255.37) * mm, "end": v(3144.1, -3255.37) * mm});
            skLineSegment(sketch, "E268.left", {"start": v(3133.52, -3265.87) * mm, "end": v(3134.43, -3256.28) * mm});
            skLineSegment(sketch, "E268.right", {"start": v(3146.02, -3265.87) * mm, "end": v(3145.1, -3256.28) * mm});
            skLineSegment(sketch, "E269.top", {"start": v(3135.19, -3413.87) * mm, "end": v(3144.35, -3413.87) * mm});
            skLineSegment(sketch, "E269.left", {"start": v(3133.34, -3424.96) * mm, "end": v(3134.2, -3414.8) * mm});
            skLineSegment(sketch, "E269.right", {"start": v(3146.2, -3424.96) * mm, "end": v(3145.34, -3414.8) * mm});
            skLineSegment(sketch, "E270", {"start": v(3124.27, -3265.87) * mm, "end": v(3118.27, -3281.87) * mm});
            skLineSegment(sketch, "E271", {"start": v(3155.27, -3265.87) * mm, "end": v(3161.27, -3281.87) * mm});
            skLineSegment(sketch, "E272.trimOffspring", {"start": v(3147.19, -3425.87) * mm, "end": v(3155.27, -3425.87) * mm});
            skLineSegment(sketch, "E273", {"start": v(3118.27, -3409.87) * mm, "end": v(3124.27, -3425.87) * mm});
            skLineSegment(sketch, "E274", {"start": v(3161.27, -3409.87) * mm, "end": v(3155.27, -3425.87) * mm});
            skPoint(sketch, "E275.visualSharp", {"position": v(3134.52, -3255.37) * mm});
            skArc(sketch, "E275.filletArc", {"start": v(3135.43, -3255.37) * mm, "mid": v(3134.75, -3255.63) * mm, "end": v(3134.43, -3256.28) * mm});
            skPoint(sketch, "E276.visualSharp", {"position": v(3145.02, -3255.37) * mm});
            skArc(sketch, "E276.filletArc", {"start": v(3145.1, -3256.28) * mm, "mid": v(3144.78, -3255.63) * mm, "end": v(3144.1, -3255.37) * mm});
            skPoint(sketch, "E277.visualSharp", {"position": v(3134.27, -3413.87) * mm});
            skArc(sketch, "E277.filletArc", {"start": v(3135.19, -3413.87) * mm, "mid": v(3134.51, -3414.14) * mm, "end": v(3134.2, -3414.8) * mm});
            skPoint(sketch, "E278.visualSharp", {"position": v(3145.27, -3413.87) * mm});
            skArc(sketch, "E278.filletArc", {"start": v(3145.34, -3414.8) * mm, "mid": v(3145.03, -3414.14) * mm, "end": v(3144.35, -3413.87) * mm});
            skPoint(sketch, "E279.visualSharp", {"position": v(3133.27, -3425.87) * mm});
            skArc(sketch, "E279.filletArc", {"start": v(3132.35, -3425.87) * mm, "mid": v(3133.03, -3425.6) * mm, "end": v(3133.34, -3424.96) * mm});
            skPoint(sketch, "E280.visualSharp", {"position": v(3146.27, -3425.87) * mm});
            skArc(sketch, "E280.filletArc", {"start": v(3146.2, -3424.96) * mm, "mid": v(3146.51, -3425.6) * mm, "end": v(3147.19, -3425.87) * mm});
            skSolve(sketch);
        }
        {
            var Q0;
            Q0=makeQuery(id+"F77.imprint","IMPRINT",FACE,{"disambiguationData":[TD([[makeQuery(id+"F77.imprint","IMPRINT",EDGE,{"derivedFrom":sQuery(id+"F77.wireOp",EDGE,"E267.top")}),1.0]])]});
            var Q1;
            Q1=makeQuery(id+"F77.imprint","IMPRINT",FACE,{"disambiguationData":[TD([[makeQuery(id+"F77.imprint","IMPRINT",EDGE,{"derivedFrom":sQuery(id+"F77.wireOp",EDGE,"E268.bottom")}),1.0]])]});
            extrude(context, id + "F78", {"entities" : qUnion([Q0, Q1]), "depth" : 2061 * mm, "offsetDistance" : 25 * mm});
        }
        {
            var Q0;
            Q0=makeQuery(id+"F78.opExtrude","SWEPT_FACE",FACE,{"disambiguationData":[OSD([sQuery(id+"F77.wireOp",EDGE,"E267.right")])]});
            var sketch = newSketch(context, id + "F79", { "sketchPlane" : qUnion([Q0])});
            skLineSegment(sketch, "E281", {"start": v(-3476.86, 2224.7) * mm, "end": v(-3195.35, 1320.86) * mm});
            skLineSegment(sketch, "E282", {"start": v(-3195.35, 1320.86) * mm, "end": v(-3195.35, 2190.44) * mm});
            skLineSegment(sketch, "E283", {"start": v(-3195.35, 2190.44) * mm, "end": v(-3476.86, 2224.7) * mm});
            skLineSegment(sketch, "E284", {"start": v(-3463.21, -119.88) * mm, "end": v(-3204.08, 712.1) * mm});
            skLineSegment(sketch, "E285", {"start": v(-3204.08, 712.1) * mm, "end": v(-3204.08, -135.3) * mm});
            skLineSegment(sketch, "E286", {"start": v(-3204.08, -135.3) * mm, "end": v(-3463.21, -119.88) * mm});
            skSolve(sketch);
        }
        {
            var Q0;
            {var subQ1=sQuery(id+"F79.wireOp",EDGE,"E285");Q0=makeQuery(id+"F79.imprint","IMPRINT",FACE,{"disambiguationData":[TD([[makeQuery(id+"F79.imprint","IMPRINT",EDGE,{"derivedFrom":subQ1}),-1.0]])]});}
            var Q1;
            {var subQ1=sQuery(id+"F77.wireOp",EDGE,"E267.right");var subQ6=makeQuery(id+"F78.opExtrude","CAP_EDGE",EDGE,{"disambiguationData":[OSD([subQ1])],"isStart":true});Q1=makeQuery(id+"F79.imprint","IMPRINT",FACE,{"disambiguationData":[TD([[makeQuery(id+"F79.imprint","IMPRINT",EDGE,{"derivedFrom":subQ6}),-1.0]])]});}
            var Q2;
            {var subQ1=sQuery(id+"F79.wireOp",EDGE,"E282");Q2=makeQuery(id+"F79.imprint","IMPRINT",FACE,{"disambiguationData":[TD([[makeQuery(id+"F79.imprint","IMPRINT",EDGE,{"derivedFrom":subQ1}),1.0]])]});}
            var Q3;
            {var subQ1=sQuery(id+"F77.wireOp",EDGE,"E267.right");var subQ6=makeQuery(id+"F78.opExtrude","CAP_EDGE",EDGE,{"disambiguationData":[OSD([subQ1])],"isStart":false});Q3=makeQuery(id+"F79.imprint","IMPRINT",FACE,{"disambiguationData":[TD([[makeQuery(id+"F79.imprint","IMPRINT",EDGE,{"derivedFrom":subQ6}),1.0]])]});}
            extrude(context, id + "F80", {"entities" : qUnion([Q0, Q1, Q2, Q3]), "operationType" : NewBodyOperationType.REMOVE, "oppositeDirection" : true, "depth" : 55 * mm, "offsetDistance" : 25 * mm});
        }
        {
            var Q0;
            {var subQ8=sQuery(id+"F34.wireOp",EDGE,"E43.0");Q0=makeQuery(id+"F34.imprint","IMPRINT",FACE,{"disambiguationData":[TD([[makeQuery(id+"F34.imprint","IMPRINT",EDGE,{"derivedFrom":subQ8}),1.0]])]});}
            var sketch = newSketch(context, id + "F81", { "sketchPlane" : qUnion([Q0])});
            skLineSegment(sketch, "E287.bottom", {"start": v(3270.91, -3266.25) * mm, "end": v(3301.91, -3266.25) * mm});
            skLineSegment(sketch, "E287.top", {"start": v(3270.91, -3426.25) * mm, "end": v(3279, -3426.25) * mm});
            skLineSegment(sketch, "E287.left", {"start": v(3264.91, -3282.25) * mm, "end": v(3264.91, -3410.25) * mm});
            skLineSegment(sketch, "E287.right", {"start": v(3307.91, -3282.25) * mm, "end": v(3307.91, -3410.25) * mm});
            skLineSegment(sketch, "E288.bottom", {"start": v(3280.16, -3266.25) * mm, "end": v(3292.66, -3266.25) * mm});
            skLineSegment(sketch, "E288.top", {"start": v(3282.07, -3255.75) * mm, "end": v(3290.75, -3255.75) * mm});
            skLineSegment(sketch, "E288.left", {"start": v(3280.16, -3266.25) * mm, "end": v(3281.08, -3256.65) * mm});
            skLineSegment(sketch, "E288.right", {"start": v(3292.66, -3266.25) * mm, "end": v(3291.75, -3256.65) * mm});
            skLineSegment(sketch, "E289.top", {"start": v(3281.83, -3414.25) * mm, "end": v(3291, -3414.25) * mm});
            skLineSegment(sketch, "E289.left", {"start": v(3279.99, -3425.33) * mm, "end": v(3280.84, -3415.17) * mm});
            skLineSegment(sketch, "E289.right", {"start": v(3292.84, -3425.33) * mm, "end": v(3291.99, -3415.17) * mm});
            skLineSegment(sketch, "E290", {"start": v(3270.91, -3266.25) * mm, "end": v(3264.91, -3282.25) * mm});
            skLineSegment(sketch, "E291", {"start": v(3301.91, -3266.25) * mm, "end": v(3307.91, -3282.25) * mm});
            skLineSegment(sketch, "E292.trimOffspring", {"start": v(3293.83, -3426.25) * mm, "end": v(3301.91, -3426.25) * mm});
            skLineSegment(sketch, "E293", {"start": v(3264.91, -3410.25) * mm, "end": v(3270.91, -3426.25) * mm});
            skLineSegment(sketch, "E294", {"start": v(3307.91, -3410.25) * mm, "end": v(3301.91, -3426.25) * mm});
            skPoint(sketch, "E295.visualSharp", {"position": v(3281.16, -3255.75) * mm});
            skArc(sketch, "E295.filletArc", {"start": v(3282.07, -3255.75) * mm, "mid": v(3281.4, -3256) * mm, "end": v(3281.08, -3256.65) * mm});
            skPoint(sketch, "E296.visualSharp", {"position": v(3291.66, -3255.75) * mm});
            skArc(sketch, "E296.filletArc", {"start": v(3291.75, -3256.65) * mm, "mid": v(3291.43, -3256) * mm, "end": v(3290.75, -3255.75) * mm});
            skPoint(sketch, "E297.visualSharp", {"position": v(3280.91, -3414.25) * mm});
            skArc(sketch, "E297.filletArc", {"start": v(3281.83, -3414.25) * mm, "mid": v(3281.16, -3414.51) * mm, "end": v(3280.84, -3415.17) * mm});
            skPoint(sketch, "E298.visualSharp", {"position": v(3291.91, -3414.25) * mm});
            skArc(sketch, "E298.filletArc", {"start": v(3291.99, -3415.17) * mm, "mid": v(3291.67, -3414.51) * mm, "end": v(3291, -3414.25) * mm});
            skPoint(sketch, "E299.visualSharp", {"position": v(3279.91, -3426.25) * mm});
            skArc(sketch, "E299.filletArc", {"start": v(3279, -3426.25) * mm, "mid": v(3279.67, -3425.99) * mm, "end": v(3279.99, -3425.33) * mm});
            skPoint(sketch, "E300.visualSharp", {"position": v(3292.91, -3426.25) * mm});
            skArc(sketch, "E300.filletArc", {"start": v(3292.84, -3425.33) * mm, "mid": v(3293.16, -3425.99) * mm, "end": v(3293.83, -3426.25) * mm});
            skSolve(sketch);
        }
        {
            var Q0;
            Q0=makeQuery(id+"F81.imprint","IMPRINT",FACE,{"disambiguationData":[TD([[makeQuery(id+"F81.imprint","IMPRINT",EDGE,{"derivedFrom":sQuery(id+"F81.wireOp",EDGE,"E287.top")}),1.0]])]});
            var Q1;
            Q1=makeQuery(id+"F81.imprint","IMPRINT",FACE,{"disambiguationData":[TD([[makeQuery(id+"F81.imprint","IMPRINT",EDGE,{"derivedFrom":sQuery(id+"F81.wireOp",EDGE,"E288.bottom")}),1.0]])]});
            extrude(context, id + "F82", {"entities" : qUnion([Q0, Q1]), "depth" : 1034 * mm, "offsetDistance" : 25 * mm});
        }
        {
            var Q0;
            Q0=makeQuery(id+"F82.opExtrude","SWEPT_FACE",FACE,{"disambiguationData":[OSD([sQuery(id+"F81.wireOp",EDGE,"E287.right")])]});
            var sketch = newSketch(context, id + "F83", { "sketchPlane" : qUnion([Q0])});
            skLineSegment(sketch, "E301", {"start": v(-3461.1, 1145.87) * mm, "end": v(-3265.22, 517) * mm});
            skLineSegment(sketch, "E302", {"start": v(-3265.22, 517) * mm, "end": v(-3265.22, 1192.39) * mm});
            skLineSegment(sketch, "E303", {"start": v(-3265.22, 1192.39) * mm, "end": v(-3461.1, 1145.87) * mm});
            skLineSegment(sketch, "E304", {"start": v(-3265.22, 517) * mm, "end": v(-3472.56, -148.67) * mm});
            skLineSegment(sketch, "E305", {"start": v(-3472.56, -148.67) * mm, "end": v(-3265.22, -148.67) * mm});
            skLineSegment(sketch, "E306", {"start": v(-3265.22, -148.67) * mm, "end": v(-3265.22, 517) * mm});
            skLineSegment(sketch, "E307", {"start": v(-3265.22, 1192.39) * mm, "end": v(-3044.21, 1192.39) * mm});
            skLineSegment(sketch, "E308", {"start": v(-3044.21, 1192.39) * mm, "end": v(-3044.21, -165.35) * mm});
            skLineSegment(sketch, "E309", {"start": v(-3044.21, -165.35) * mm, "end": v(-3265.22, -148.67) * mm});
            skSolve(sketch);
        }
        {
            var Q0;
            {var subQ1=sQuery(id+"F81.wireOp",EDGE,"E287.right");var subQ6=makeQuery(id+"F82.opExtrude","CAP_EDGE",EDGE,{"disambiguationData":[OSD([subQ1])],"isStart":false});Q0=makeQuery(id+"F83.imprint","IMPRINT",FACE,{"disambiguationData":[TD([[makeQuery(id+"F83.imprint","IMPRINT",EDGE,{"derivedFrom":subQ6}),1.0]])]});}
            var Q1;
            {var subQ1=sQuery(id+"F81.wireOp",EDGE,"E287.right");var subQ6=makeQuery(id+"F82.opExtrude","CAP_EDGE",EDGE,{"disambiguationData":[OSD([subQ1])],"isStart":true});Q1=makeQuery(id+"F83.imprint","IMPRINT",FACE,{"disambiguationData":[TD([[makeQuery(id+"F83.imprint","IMPRINT",EDGE,{"derivedFrom":subQ6}),-1.0]])]});}
            var Q2;
            {var subQ1=sQuery(id+"F83.wireOp",EDGE,"E302");Q2=makeQuery(id+"F83.imprint","IMPRINT",FACE,{"disambiguationData":[TD([[makeQuery(id+"F83.imprint","IMPRINT",EDGE,{"derivedFrom":subQ1}),1.0]])]});}
            var Q3;
            {var subQ1=sQuery(id+"F83.wireOp",EDGE,"E305");Q3=makeQuery(id+"F83.imprint","IMPRINT",FACE,{"disambiguationData":[TD([[makeQuery(id+"F83.imprint","IMPRINT",EDGE,{"derivedFrom":subQ1}),1.0]])]});}
            var Q4;
            Q4=makeQuery(id+"F83.imprint","IMPRINT",FACE,{"disambiguationData":[TD([[makeQuery(id+"F83.imprint","IMPRINT",EDGE,{"derivedFrom":sQuery(id+"F83.wireOp",EDGE,"E302")}),-1.0]])]});
            extrude(context, id + "F84", {"entities" : qUnion([Q0, Q1, Q2, Q3, Q4]), "operationType" : NewBodyOperationType.REMOVE, "oppositeDirection" : true, "depth" : 55 * mm, "offsetDistance" : 25 * mm});
        }
        {
            var Q0;
            {var subQ8=sQuery(id+"F34.wireOp",EDGE,"E43.0");Q0=makeQuery(id+"F34.imprint","IMPRINT",FACE,{"disambiguationData":[TD([[makeQuery(id+"F34.imprint","IMPRINT",EDGE,{"derivedFrom":subQ8}),1.0]])]});}
            var sketch = newSketch(context, id + "F85", { "sketchPlane" : qUnion([Q0])});
            skLineSegment(sketch, "E310.bottom", {"start": v(1509.63, -3800.28) * mm, "end": v(1540.63, -3800.28) * mm});
            skLineSegment(sketch, "E310.top", {"start": v(1509.63, -3960.28) * mm, "end": v(1517.7, -3960.28) * mm});
            skLineSegment(sketch, "E310.left", {"start": v(1503.63, -3816.28) * mm, "end": v(1503.63, -3944.28) * mm});
            skLineSegment(sketch, "E310.right", {"start": v(1546.63, -3816.28) * mm, "end": v(1546.63, -3944.28) * mm});
            skLineSegment(sketch, "E311.bottom", {"start": v(1518.88, -3800.28) * mm, "end": v(1531.38, -3800.28) * mm});
            skLineSegment(sketch, "E311.top", {"start": v(1520.79, -3789.78) * mm, "end": v(1529.47, -3789.78) * mm});
            skLineSegment(sketch, "E311.left", {"start": v(1518.88, -3800.28) * mm, "end": v(1519.79, -3790.69) * mm});
            skLineSegment(sketch, "E311.right", {"start": v(1531.38, -3800.28) * mm, "end": v(1530.46, -3790.69) * mm});
            skLineSegment(sketch, "E312.top", {"start": v(1520.55, -3948.28) * mm, "end": v(1529.7, -3948.28) * mm});
            skLineSegment(sketch, "E312.left", {"start": v(1518.7, -3959.37) * mm, "end": v(1519.55, -3949.2) * mm});
            skLineSegment(sketch, "E312.right", {"start": v(1531.55, -3959.37) * mm, "end": v(1530.7, -3949.2) * mm});
            skLineSegment(sketch, "E313", {"start": v(1509.63, -3800.28) * mm, "end": v(1503.63, -3816.28) * mm});
            skLineSegment(sketch, "E314", {"start": v(1540.63, -3800.28) * mm, "end": v(1546.63, -3816.28) * mm});
            skLineSegment(sketch, "E315.trimOffspring", {"start": v(1532.55, -3960.28) * mm, "end": v(1540.63, -3960.28) * mm});
            skLineSegment(sketch, "E316", {"start": v(1503.63, -3944.28) * mm, "end": v(1509.63, -3960.28) * mm});
            skLineSegment(sketch, "E317", {"start": v(1546.63, -3944.28) * mm, "end": v(1540.63, -3960.28) * mm});
            skPoint(sketch, "E318.visualSharp", {"position": v(1519.88, -3789.78) * mm});
            skArc(sketch, "E318.filletArc", {"start": v(1520.79, -3789.78) * mm, "mid": v(1520.11, -3790.04) * mm, "end": v(1519.79, -3790.69) * mm});
            skPoint(sketch, "E319.visualSharp", {"position": v(1530.38, -3789.78) * mm});
            skArc(sketch, "E319.filletArc", {"start": v(1530.46, -3790.69) * mm, "mid": v(1530.14, -3790.04) * mm, "end": v(1529.47, -3789.78) * mm});
            skPoint(sketch, "E320.visualSharp", {"position": v(1519.63, -3948.28) * mm});
            skArc(sketch, "E320.filletArc", {"start": v(1520.55, -3948.28) * mm, "mid": v(1519.87, -3948.55) * mm, "end": v(1519.55, -3949.2) * mm});
            skPoint(sketch, "E321.visualSharp", {"position": v(1530.63, -3948.28) * mm});
            skArc(sketch, "E321.filletArc", {"start": v(1530.7, -3949.2) * mm, "mid": v(1530.38, -3948.55) * mm, "end": v(1529.7, -3948.28) * mm});
            skPoint(sketch, "E322.visualSharp", {"position": v(1518.63, -3960.28) * mm});
            skArc(sketch, "E322.filletArc", {"start": v(1517.7, -3960.28) * mm, "mid": v(1518.38, -3960.02) * mm, "end": v(1518.7, -3959.37) * mm});
            skPoint(sketch, "E323.visualSharp", {"position": v(1531.63, -3960.28) * mm});
            skArc(sketch, "E323.filletArc", {"start": v(1531.55, -3959.37) * mm, "mid": v(1531.87, -3960.02) * mm, "end": v(1532.55, -3960.28) * mm});
            skSolve(sketch);
        }
        {
            var Q0;
            Q0=makeQuery(id+"F85.imprint","IMPRINT",FACE,{"disambiguationData":[TD([[makeQuery(id+"F85.imprint","IMPRINT",EDGE,{"derivedFrom":sQuery(id+"F85.wireOp",EDGE,"E310.top")}),1.0]])]});
            var Q1;
            Q1=makeQuery(id+"F85.imprint","IMPRINT",FACE,{"disambiguationData":[TD([[makeQuery(id+"F85.imprint","IMPRINT",EDGE,{"derivedFrom":sQuery(id+"F85.wireOp",EDGE,"E311.bottom")}),1.0]])]});
            extrude(context, id + "F86", {"entities" : qUnion([Q0, Q1]), "depth" : 2380 * mm, "offsetDistance" : 25 * mm});
        }
        {
            var Q0;
            Q0=makeQuery(id+"F86.opExtrude","SWEPT_FACE",FACE,{"disambiguationData":[OSD([sQuery(id+"F85.wireOp",EDGE,"E310.right")])]});
            var sketch = newSketch(context, id + "F87", { "sketchPlane" : qUnion([Q0])});
            skLineSegment(sketch, "E324.bottom", {"start": v(-3785.28, 2280) * mm, "end": v(-3840.28, 2280) * mm});
            skLineSegment(sketch, "E324.top", {"start": v(-3785.28, 2237) * mm, "end": v(-3840.28, 2237) * mm});
            skLineSegment(sketch, "E324.left", {"start": v(-3785.28, 2280) * mm, "end": v(-3785.28, 2237) * mm});
            skLineSegment(sketch, "E324.right", {"start": v(-3840.28, 2280) * mm, "end": v(-3840.28, 2237) * mm});
            skLineSegment(sketch, "E325.bottom", {"start": v(-3920.28, 2280) * mm, "end": v(-3975.28, 2280) * mm});
            skLineSegment(sketch, "E325.top", {"start": v(-3920.28, 2237) * mm, "end": v(-3975.28, 2237) * mm});
            skLineSegment(sketch, "E325.left", {"start": v(-3920.28, 2280) * mm, "end": v(-3920.28, 2237) * mm});
            skLineSegment(sketch, "E325.right", {"start": v(-3975.28, 2280) * mm, "end": v(-3975.28, 2237) * mm});
            skSolve(sketch);
        }
        {
            var Q0;
            {var subQ0=sQuery(id+"F87.wireOp",EDGE,"E324.left");Q0=makeQuery(id+"F87.imprint","IMPRINT",FACE,{"disambiguationData":[TD([[makeQuery(id+"F87.imprint","IMPRINT",EDGE,{"derivedFrom":subQ0}),-1.0]])]});}
            var Q1;
            {var subQ0=sQuery(id+"F87.wireOp",EDGE,"E324.right");Q1=makeQuery(id+"F87.imprint","IMPRINT",FACE,{"disambiguationData":[TD([[makeQuery(id+"F87.imprint","IMPRINT",EDGE,{"derivedFrom":subQ0}),1.0]])]});}
            var Q2;
            {var subQ0=sQuery(id+"F87.wireOp",EDGE,"E325.left");Q2=makeQuery(id+"F87.imprint","IMPRINT",FACE,{"disambiguationData":[TD([[makeQuery(id+"F87.imprint","IMPRINT",EDGE,{"derivedFrom":subQ0}),-1.0]])]});}
            var Q3;
            {var subQ0=sQuery(id+"F87.wireOp",EDGE,"E325.right");Q3=makeQuery(id+"F87.imprint","IMPRINT",FACE,{"disambiguationData":[TD([[makeQuery(id+"F87.imprint","IMPRINT",EDGE,{"derivedFrom":subQ0}),1.0]])]});}
            extrude(context, id + "F88", {"entities" : qUnion([Q0, Q1, Q2, Q3]), "operationType" : NewBodyOperationType.REMOVE, "oppositeDirection" : true, "depth" : 55 * mm, "offsetDistance" : 25 * mm});
        }
        {
            var Q0;
            {var subQ8=sQuery(id+"F34.wireOp",EDGE,"E43.0");Q0=makeQuery(id+"F34.imprint","IMPRINT",FACE,{"disambiguationData":[TD([[makeQuery(id+"F34.imprint","IMPRINT",EDGE,{"derivedFrom":subQ8}),1.0]])]});}
            var sketch = newSketch(context, id + "F89", { "sketchPlane" : qUnion([Q0])});
            skLineSegment(sketch, "E326.bottom", {"start": v(1303.18, -4366.94) * mm, "end": v(1334.18, -4366.94) * mm});
            skLineSegment(sketch, "E326.top", {"start": v(1303.18, -4526.94) * mm, "end": v(1311.26, -4526.94) * mm});
            skLineSegment(sketch, "E326.left", {"start": v(1297.18, -4382.94) * mm, "end": v(1297.18, -4510.94) * mm});
            skLineSegment(sketch, "E326.right", {"start": v(1340.18, -4382.94) * mm, "end": v(1340.18, -4510.94) * mm});
            skLineSegment(sketch, "E327.bottom", {"start": v(1312.43, -4366.94) * mm, "end": v(1324.93, -4366.94) * mm});
            skLineSegment(sketch, "E327.top", {"start": v(1314.34, -4356.44) * mm, "end": v(1323.02, -4356.44) * mm});
            skLineSegment(sketch, "E327.left", {"start": v(1312.43, -4366.94) * mm, "end": v(1313.34, -4357.34) * mm});
            skLineSegment(sketch, "E327.right", {"start": v(1324.93, -4366.94) * mm, "end": v(1324.02, -4357.34) * mm});
            skLineSegment(sketch, "E328.top", {"start": v(1314.1, -4514.94) * mm, "end": v(1323.26, -4514.94) * mm});
            skLineSegment(sketch, "E328.left", {"start": v(1312.26, -4526.02) * mm, "end": v(1313.1, -4515.85) * mm});
            skLineSegment(sketch, "E328.right", {"start": v(1325.1, -4526.02) * mm, "end": v(1324.26, -4515.85) * mm});
            skLineSegment(sketch, "E329", {"start": v(1303.18, -4366.94) * mm, "end": v(1297.18, -4382.94) * mm});
            skLineSegment(sketch, "E330", {"start": v(1334.18, -4366.94) * mm, "end": v(1340.18, -4382.94) * mm});
            skLineSegment(sketch, "E331.trimOffspring", {"start": v(1326.1, -4526.94) * mm, "end": v(1334.18, -4526.94) * mm});
            skLineSegment(sketch, "E332", {"start": v(1297.18, -4510.94) * mm, "end": v(1303.18, -4526.94) * mm});
            skLineSegment(sketch, "E333", {"start": v(1340.18, -4510.94) * mm, "end": v(1334.18, -4526.94) * mm});
            skPoint(sketch, "E334.visualSharp", {"position": v(1313.43, -4356.44) * mm});
            skArc(sketch, "E334.filletArc", {"start": v(1314.34, -4356.44) * mm, "mid": v(1313.67, -4356.7) * mm, "end": v(1313.34, -4357.34) * mm});
            skPoint(sketch, "E335.visualSharp", {"position": v(1323.93, -4356.44) * mm});
            skArc(sketch, "E335.filletArc", {"start": v(1324.02, -4357.34) * mm, "mid": v(1323.7, -4356.7) * mm, "end": v(1323.02, -4356.44) * mm});
            skPoint(sketch, "E336.visualSharp", {"position": v(1313.18, -4514.94) * mm});
            skArc(sketch, "E336.filletArc", {"start": v(1314.1, -4514.94) * mm, "mid": v(1313.42, -4515.2) * mm, "end": v(1313.1, -4515.85) * mm});
            skPoint(sketch, "E337.visualSharp", {"position": v(1324.18, -4514.94) * mm});
            skArc(sketch, "E337.filletArc", {"start": v(1324.26, -4515.85) * mm, "mid": v(1323.94, -4515.2) * mm, "end": v(1323.26, -4514.94) * mm});
            skPoint(sketch, "E338.visualSharp", {"position": v(1312.18, -4526.94) * mm});
            skArc(sketch, "E338.filletArc", {"start": v(1311.26, -4526.94) * mm, "mid": v(1311.94, -4526.67) * mm, "end": v(1312.26, -4526.02) * mm});
            skPoint(sketch, "E339.visualSharp", {"position": v(1325.18, -4526.94) * mm});
            skArc(sketch, "E339.filletArc", {"start": v(1325.1, -4526.02) * mm, "mid": v(1325.42, -4526.67) * mm, "end": v(1326.1, -4526.94) * mm});
            skSolve(sketch);
        }
        {
            var Q0;
            Q0=makeQuery(id+"F89.imprint","IMPRINT",FACE,{"disambiguationData":[TD([[makeQuery(id+"F89.imprint","IMPRINT",EDGE,{"derivedFrom":sQuery(id+"F89.wireOp",EDGE,"E326.top")}),1.0]])]});
            var Q1;
            Q1=makeQuery(id+"F89.imprint","IMPRINT",FACE,{"disambiguationData":[TD([[makeQuery(id+"F89.imprint","IMPRINT",EDGE,{"derivedFrom":sQuery(id+"F89.wireOp",EDGE,"E327.bottom")}),1.0]])]});
            extrude(context, id + "F90", {"entities" : qUnion([Q0, Q1]), "depth" : 2200 * mm, "offsetDistance" : 25 * mm});
        }
        {
            var Q0;
            Q0=makeQuery(id+"F5.opExtrude","SWEPT_FACE",FACE,{"disambiguationData":[OSD([sQuery(id+"F4.wireOp",EDGE,"E2.left")])]});
            var sketch = newSketch(context, id + "F91", { "sketchPlane" : qUnion([Q0])});
            skLineSegment(sketch, "E340.bottom", {"start": v(-154.83, 2914) * mm, "end": v(-371.08, 2914) * mm});
            skLineSegment(sketch, "E340.top", {"start": v(-154.83, 2885.5) * mm, "end": v(-371.08, 2885.5) * mm});
            skLineSegment(sketch, "E340.left", {"start": v(-154.83, 2914) * mm, "end": v(-154.83, 2885.5) * mm});
            skLineSegment(sketch, "E340.right", {"start": v(-371.08, 2914) * mm, "end": v(-371.08, 2885.5) * mm});
            skLineSegment(sketch, "E341.bottom", {"start": v(-268.88, 1479.5) * mm, "end": v(-154.83, 1479.5) * mm});
            skLineSegment(sketch, "E341.top", {"start": v(-268.88, 1434.5) * mm, "end": v(-154.83, 1434.5) * mm});
            skLineSegment(sketch, "E341.left", {"start": v(-268.88, 1479.5) * mm, "end": v(-268.88, 1434.5) * mm});
            skLineSegment(sketch, "E341.right", {"start": v(-154.83, 1479.5) * mm, "end": v(-154.83, 1434.5) * mm});
            skLineSegment(sketch, "E342.bottom", {"start": v(-154.83, 0) * mm, "end": v(-284.42, 0) * mm});
            skLineSegment(sketch, "E342.top", {"start": v(-154.83, 28.5) * mm, "end": v(-284.42, 28.5) * mm});
            skLineSegment(sketch, "E342.left", {"start": v(-154.83, 0) * mm, "end": v(-154.83, 28.5) * mm});
            skLineSegment(sketch, "E342.right", {"start": v(-284.42, 0) * mm, "end": v(-284.42, 28.5) * mm});
            skSolve(sketch);
        }
        {
            var Q0;
            {var subQ4=sQuery(id+"F91.wireOp",EDGE,"E340.left");Q0=makeQuery(id+"F91.imprint","IMPRINT",FACE,{"disambiguationData":[TD([[makeQuery(id+"F91.imprint","IMPRINT",EDGE,{"derivedFrom":subQ4}),-1.0]])]});}
            var Q1;
            {var subQ0=sQuery(id+"F91.wireOp",EDGE,"E341.right");Q1=makeQuery(id+"F91.imprint","IMPRINT",FACE,{"disambiguationData":[TD([[makeQuery(id+"F91.imprint","IMPRINT",EDGE,{"derivedFrom":subQ0}),-1.0]])]});}
            var Q2;
            {var subQ4=sQuery(id+"F91.wireOp",EDGE,"E342.left");Q2=makeQuery(id+"F91.imprint","IMPRINT",FACE,{"disambiguationData":[TD([[makeQuery(id+"F91.imprint","IMPRINT",EDGE,{"derivedFrom":subQ4}),1.0]])]});}
            extrude(context, id + "F92", {"entities" : qUnion([Q0, Q1, Q2]), "operationType" : NewBodyOperationType.REMOVE, "oppositeDirection" : true, "depth" : 55 * mm, "offsetDistance" : 25 * mm});
        }
        {
            var Q0;
            Q0=makeQuery(id+"F1.opExtrude","SWEPT_FACE",FACE,{"disambiguationData":[OSD([sQuery(id+"F0.wireOp",EDGE,"E0.left")])]});
            var sketch = newSketch(context, id + "F93", { "sketchPlane" : qUnion([Q0])});
            skLineSegment(sketch, "E343.bottom", {"start": v(-208.66, 5210) * mm, "end": v(-48.66, 5210) * mm});
            skLineSegment(sketch, "E343.top", {"start": v(-208.66, 5165) * mm, "end": v(-48.66, 5165) * mm});
            skLineSegment(sketch, "E343.left", {"start": v(-208.66, 5210) * mm, "end": v(-208.66, 5165) * mm});
            skLineSegment(sketch, "E343.right", {"start": v(-48.66, 5210) * mm, "end": v(-48.66, 5165) * mm});
            skLineSegment(sketch, "E344.bottom", {"start": v(-208.66, 90) * mm, "end": v(-48.66, 90) * mm});
            skLineSegment(sketch, "E344.top", {"start": v(-208.66, 45) * mm, "end": v(-48.66, 45) * mm});
            skLineSegment(sketch, "E344.left", {"start": v(-208.66, 90) * mm, "end": v(-208.66, 45) * mm});
            skLineSegment(sketch, "E344.right", {"start": v(-48.66, 90) * mm, "end": v(-48.66, 45) * mm});
            skSolve(sketch);
        }
        {
            var Q0;
            Q0=makeQuery(id+"F93.imprint","IMPRINT",FACE,{"disambiguationData":[TD([[makeQuery(id+"F93.imprint","IMPRINT",EDGE,{"derivedFrom":sQuery(id+"F93.wireOp",EDGE,"E343.bottom")}),-1.0]])]});
            var Q1;
            Q1=makeQuery(id+"F93.imprint","IMPRINT",FACE,{"disambiguationData":[TD([[makeQuery(id+"F93.imprint","IMPRINT",EDGE,{"derivedFrom":sQuery(id+"F93.wireOp",EDGE,"E344.bottom")}),-1.0]])]});
            extrude(context, id + "F94", {"entities" : qUnion([Q0, Q1]), "operationType" : NewBodyOperationType.REMOVE, "oppositeDirection" : true, "depth" : 55 * mm, "offsetDistance" : 25 * mm});
        }
        {
            var Q0;
            {var subQ8=sQuery(id+"F34.wireOp",EDGE,"E43.0");Q0=makeQuery(id+"F34.imprint","IMPRINT",FACE,{"disambiguationData":[TD([[makeQuery(id+"F34.imprint","IMPRINT",EDGE,{"derivedFrom":subQ8}),1.0]])]});}
            var sketch = newSketch(context, id + "F95", { "sketchPlane" : qUnion([Q0])});
            skLineSegment(sketch, "E345.bottom", {"start": v(-5458, -6197.23) * mm, "end": v(-5078, -6197.23) * mm});
            skLineSegment(sketch, "E345.top", {"start": v(-5458, -6547.23) * mm, "end": v(-5078, -6547.23) * mm});
            skLineSegment(sketch, "E345.left", {"start": v(-5458, -6197.23) * mm, "end": v(-5458, -6547.23) * mm});
            skLineSegment(sketch, "E345.right", {"start": v(-5078, -6197.23) * mm, "end": v(-5078, -6547.23) * mm});
            skSolve(sketch);
        }
        {
            var Q0;
            Q0=makeQuery(id+"F95.imprint","IMPRINT",FACE,{"disambiguationData":[TD([[makeQuery(id+"F95.imprint","IMPRINT",EDGE,{"derivedFrom":sQuery(id+"F95.wireOp",EDGE,"E345.bottom")}),-1.0]])]});
            extrude(context, id + "F96", {"entities" : qUnion([Q0]), "depth" : 160 * mm, "offsetDistance" : 25 * mm});
        }
        {
            var Q0;
            Q0=makeQuery(id+"F96.opExtrude","CAP_FACE",FACE,{"disambiguationData":[OSD([sQuery(id+"F95.wireOp",EDGE,"E345.bottom"),sQuery(id+"F95.wireOp",EDGE,"E345.top"),sQuery(id+"F95.wireOp",EDGE,"E345.left"),sQuery(id+"F95.wireOp",EDGE,"E345.right")])],"isStart":false});
            var sketch = newSketch(context, id + "F97", { "sketchPlane" : qUnion([Q0])});
            skLineSegment(sketch, "E346.bottom", {"start": v(-5458, -6322.23) * mm, "end": v(-5078, -6322.23) * mm});
            skLineSegment(sketch, "E346.top", {"start": v(-5458, -6422.23) * mm, "end": v(-5078, -6422.23) * mm});
            skLineSegment(sketch, "E346.left", {"start": v(-5458, -6322.23) * mm, "end": v(-5458, -6422.23) * mm});
            skLineSegment(sketch, "E346.right", {"start": v(-5078, -6322.23) * mm, "end": v(-5078, -6422.23) * mm});
            skLineSegment(sketch, "E347.bottom", {"start": v(-5318, -6197.23) * mm, "end": v(-5218, -6197.23) * mm});
            skLineSegment(sketch, "E347.top", {"start": v(-5318, -6250.09) * mm, "end": v(-5218, -6250.09) * mm});
            skLineSegment(sketch, "E347.left", {"start": v(-5318, -6197.23) * mm, "end": v(-5318, -6250.09) * mm});
            skLineSegment(sketch, "E347.right", {"start": v(-5218, -6197.23) * mm, "end": v(-5218, -6250.09) * mm});
            skLineSegment(sketch, "E348.bottom", {"start": v(-5318, -6547.23) * mm, "end": v(-5218, -6547.23) * mm});
            skLineSegment(sketch, "E348.top", {"start": v(-5318, -6487.23) * mm, "end": v(-5218, -6487.23) * mm});
            skLineSegment(sketch, "E348.left", {"start": v(-5318, -6547.23) * mm, "end": v(-5318, -6487.23) * mm});
            skLineSegment(sketch, "E348.right", {"start": v(-5218, -6547.23) * mm, "end": v(-5218, -6487.23) * mm});
            skSolve(sketch);
        }
        {
            var Q0;
            Q0=makeQuery(id+"F97.imprint","IMPRINT",FACE,{"disambiguationData":[TD([[makeQuery(id+"F97.imprint","IMPRINT",EDGE,{"derivedFrom":sQuery(id+"F97.wireOp",EDGE,"E347.bottom")}),-1.0]])]});
            var Q1;
            Q1=makeQuery(id+"F97.imprint","IMPRINT",FACE,{"disambiguationData":[TD([[makeQuery(id+"F97.imprint","IMPRINT",EDGE,{"derivedFrom":sQuery(id+"F97.wireOp",EDGE,"E346.bottom")}),-1.0]])]});
            var Q2;
            Q2=makeQuery(id+"F97.imprint","IMPRINT",FACE,{"disambiguationData":[TD([[makeQuery(id+"F97.imprint","IMPRINT",EDGE,{"derivedFrom":sQuery(id+"F97.wireOp",EDGE,"E348.bottom")}),1.0]])]});
            extrude(context, id + "F98", {"entities" : qUnion([Q0, Q1, Q2]), "operationType" : NewBodyOperationType.REMOVE, "oppositeDirection" : true, "depth" : 40 * mm, "offsetDistance" : 25 * mm});
        }
    });
